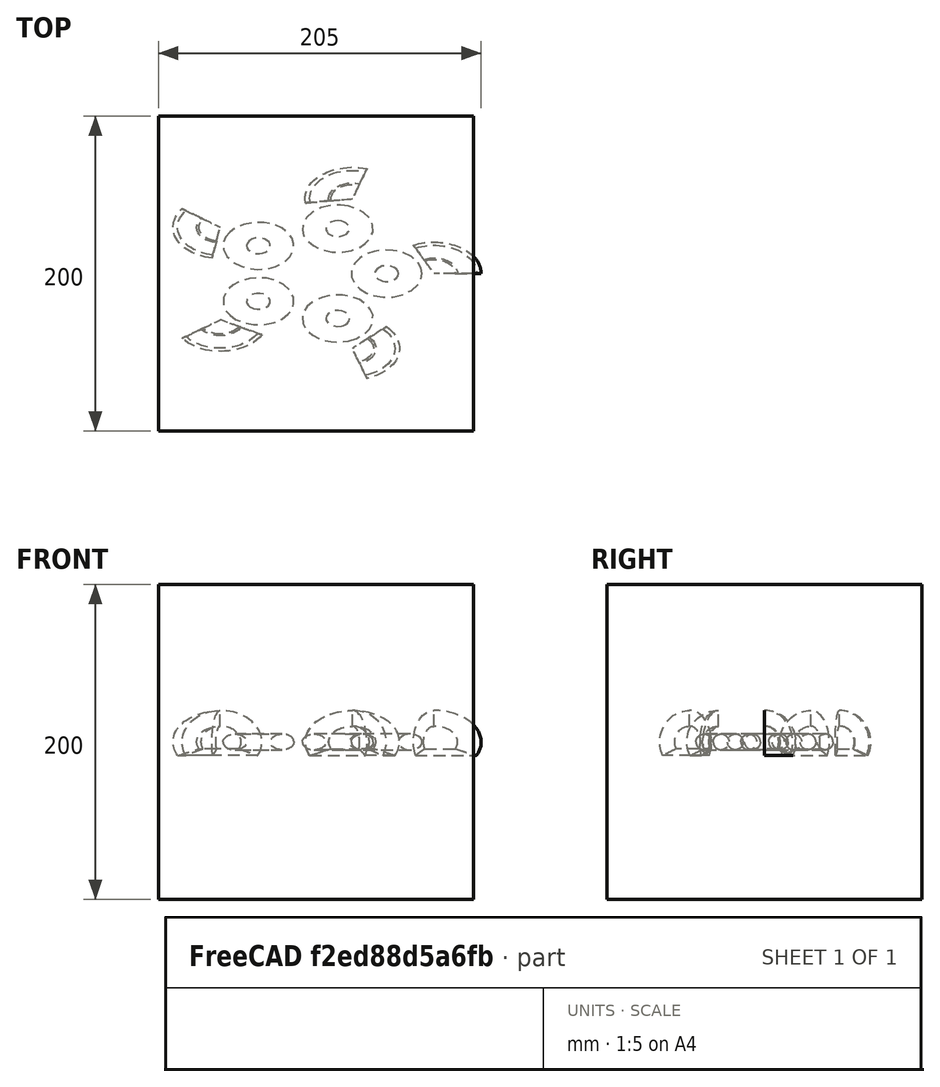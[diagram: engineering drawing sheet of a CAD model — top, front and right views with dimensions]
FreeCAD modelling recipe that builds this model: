
FCSTD DOCUMENT  (FreeCAD 0.19RUnknown)
Label: arrayTest-7_scaled
License: All rights reserved
LicenseURL: http://en.wikipedia.org/wiki/All_rights_reserved
objects: App::DocumentObjectGroupPython×1248, Part::FeaturePython×5, App::Part×2, Part::MultiFuse×1
note: 6 computed .brp shape members not serialized (recipe doc carries the construction recipe); baked Part::Feature solids carry a one-line shape summary decoded from their .brp

FEATURE [App::DocumentObjectGroupPython] HALFPI  # scripted group (container) (typed FeaturePython)
  name = HALFPI
  value = pi/2.
FEATURE [App::DocumentObjectGroupPython] PI  # scripted group (container) (typed FeaturePython)
  name = PI
  value = 1.*pi
FEATURE [App::DocumentObjectGroupPython] TWOPI  # scripted group (container) (typed FeaturePython)
  name = TWOPI
  value = 2.*pi
FEATURE [App::DocumentObjectGroupPython] Constants  # scripted group (container) (typed FeaturePython)
  Group = -> [HALFPI,PI,TWOPI]
FEATURE [App::DocumentObjectGroupPython] Variables  # scripted group (container) (typed FeaturePython)
FEATURE [App::DocumentObjectGroupPython] Quantities  # scripted group (container) (typed FeaturePython)
FEATURE [App::DocumentObjectGroupPython] Isotopes  # scripted group (container) (typed FeaturePython)
FEATURE [App::DocumentObjectGroupPython] Elements  # scripted group (container) (typed FeaturePython)
FEATURE [App::DocumentObjectGroupPython] G4Isotopes  # scripted group (container) (typed FeaturePython)
FEATURE [App::DocumentObjectGroupPython] H_element  # scripted group (container) (typed FeaturePython)
  Z = 1
  atom_value = 1.008
  formula = H
  name = H_element
FEATURE [App::DocumentObjectGroupPython] He_element  # scripted group (container) (typed FeaturePython)
  Z = 2
  atom_value = 4.0026
  formula = He
  name = He_element
FEATURE [App::DocumentObjectGroupPython] Li_element  # scripted group (container) (typed FeaturePython)
  Z = 3
  atom_value = 6.94
  formula = Li
  name = Li_element
FEATURE [App::DocumentObjectGroupPython] Be_element  # scripted group (container) (typed FeaturePython)
  Z = 4
  atom_value = 9.01218
  formula = Be
  name = Be_element
FEATURE [App::DocumentObjectGroupPython] B_element  # scripted group (container) (typed FeaturePython)
  Z = 5
  atom_value = 10.81
  formula = B
  name = B_element
FEATURE [App::DocumentObjectGroupPython] C_element  # scripted group (container) (typed FeaturePython)
  Z = 6
  atom_value = 12.011
  formula = C
  name = C_element
FEATURE [App::DocumentObjectGroupPython] N_element  # scripted group (container) (typed FeaturePython)
  Z = 7
  atom_value = 14.007
  formula = N
  name = N_element
FEATURE [App::DocumentObjectGroupPython] O_element  # scripted group (container) (typed FeaturePython)
  Z = 8
  atom_value = 15.999
  formula = O
  name = O_element
FEATURE [App::DocumentObjectGroupPython] F_element  # scripted group (container) (typed FeaturePython)
  Z = 9
  atom_value = 18.9984
  formula = F
  name = F_element
FEATURE [App::DocumentObjectGroupPython] Ne_element  # scripted group (container) (typed FeaturePython)
  Z = 10
  atom_value = 20.1797
  formula = Ne
  name = Ne_element
FEATURE [App::DocumentObjectGroupPython] Na_element  # scripted group (container) (typed FeaturePython)
  Z = 11
  atom_value = 22.9898
  formula = Na
  name = Na_element
FEATURE [App::DocumentObjectGroupPython] Mg_element  # scripted group (container) (typed FeaturePython)
  Z = 12
  atom_value = 24.305
  formula = Mg
  name = Mg_element
FEATURE [App::DocumentObjectGroupPython] Al_element  # scripted group (container) (typed FeaturePython)
  Z = 13
  atom_value = 26.9815
  formula = Al
  name = Al_element
FEATURE [App::DocumentObjectGroupPython] Si_element  # scripted group (container) (typed FeaturePython)
  Z = 14
  atom_value = 28.085
  formula = Si
  name = Si_element
FEATURE [App::DocumentObjectGroupPython] P_element  # scripted group (container) (typed FeaturePython)
  Z = 15
  atom_value = 30.9738
  formula = P
  name = P_element
FEATURE [App::DocumentObjectGroupPython] S_element  # scripted group (container) (typed FeaturePython)
  Z = 16
  atom_value = 32.06
  formula = S
  name = S_element
FEATURE [App::DocumentObjectGroupPython] Cl_element  # scripted group (container) (typed FeaturePython)
  Z = 17
  atom_value = 35.45
  formula = Cl
  name = Cl_element
FEATURE [App::DocumentObjectGroupPython] Ar_element  # scripted group (container) (typed FeaturePython)
  Z = 18
  atom_value = 39.95
  formula = Ar
  name = Ar_element
FEATURE [App::DocumentObjectGroupPython] K_element  # scripted group (container) (typed FeaturePython)
  Z = 19
  atom_value = 39.0983
  formula = K
  name = K_element
FEATURE [App::DocumentObjectGroupPython] Ca_element  # scripted group (container) (typed FeaturePython)
  Z = 20
  atom_value = 40.078
  formula = Ca
  name = Ca_element
FEATURE [App::DocumentObjectGroupPython] Sc_element  # scripted group (container) (typed FeaturePython)
  Z = 21
  atom_value = 44.9559
  formula = Sc
  name = Sc_element
FEATURE [App::DocumentObjectGroupPython] Ti_element  # scripted group (container) (typed FeaturePython)
  Z = 22
  atom_value = 47.867
  formula = Ti
  name = Ti_element
FEATURE [App::DocumentObjectGroupPython] V_element  # scripted group (container) (typed FeaturePython)
  Z = 23
  atom_value = 50.9415
  formula = V
  name = V_element
FEATURE [App::DocumentObjectGroupPython] Cr_element  # scripted group (container) (typed FeaturePython)
  Z = 24
  atom_value = 51.9961
  formula = Cr
  name = Cr_element
FEATURE [App::DocumentObjectGroupPython] Mn_element  # scripted group (container) (typed FeaturePython)
  Z = 25
  atom_value = 54.938
  formula = Mn
  name = Mn_element
FEATURE [App::DocumentObjectGroupPython] Fe_element  # scripted group (container) (typed FeaturePython)
  Z = 26
  atom_value = 55.845
  formula = Fe
  name = Fe_element
FEATURE [App::DocumentObjectGroupPython] Co_element  # scripted group (container) (typed FeaturePython)
  Z = 27
  atom_value = 58.9332
  formula = Co
  name = Co_element
FEATURE [App::DocumentObjectGroupPython] Ni_element  # scripted group (container) (typed FeaturePython)
  Z = 28
  atom_value = 58.6934
  formula = Ni
  name = Ni_element
FEATURE [App::DocumentObjectGroupPython] Cu_element  # scripted group (container) (typed FeaturePython)
  Z = 29
  atom_value = 63.546
  formula = Cu
  name = Cu_element
FEATURE [App::DocumentObjectGroupPython] Zn_element  # scripted group (container) (typed FeaturePython)
  Z = 30
  atom_value = 65.38
  formula = Zn
  name = Zn_element
FEATURE [App::DocumentObjectGroupPython] Ga_element  # scripted group (container) (typed FeaturePython)
  Z = 31
  atom_value = 69.723
  formula = Ga
  name = Ga_element
FEATURE [App::DocumentObjectGroupPython] Ge_element  # scripted group (container) (typed FeaturePython)
  Z = 32
  atom_value = 72.63
  formula = Ge
  name = Ge_element
FEATURE [App::DocumentObjectGroupPython] As_element  # scripted group (container) (typed FeaturePython)
  Z = 33
  atom_value = 74.9216
  formula = As
  name = As_element
FEATURE [App::DocumentObjectGroupPython] Se_element  # scripted group (container) (typed FeaturePython)
  Z = 34
  atom_value = 78.971
  formula = Se
  name = Se_element
FEATURE [App::DocumentObjectGroupPython] Br_element  # scripted group (container) (typed FeaturePython)
  Z = 35
  atom_value = 79.904
  formula = Br
  name = Br_element
FEATURE [App::DocumentObjectGroupPython] Kr_element  # scripted group (container) (typed FeaturePython)
  Z = 36
  atom_value = 83.798
  formula = Kr
  name = Kr_element
FEATURE [App::DocumentObjectGroupPython] Rb_element  # scripted group (container) (typed FeaturePython)
  Z = 37
  atom_value = 85.4678
  formula = Rb
  name = Rb_element
FEATURE [App::DocumentObjectGroupPython] Sr_element  # scripted group (container) (typed FeaturePython)
  Z = 38
  atom_value = 87.62
  formula = Sr
  name = Sr_element
FEATURE [App::DocumentObjectGroupPython] Y_element  # scripted group (container) (typed FeaturePython)
  Z = 39
  atom_value = 88.9058
  formula = Y
  name = Y_element
FEATURE [App::DocumentObjectGroupPython] Zr_element  # scripted group (container) (typed FeaturePython)
  Z = 40
  atom_value = 91.224
  formula = Zr
  name = Zr_element
FEATURE [App::DocumentObjectGroupPython] Nb_element  # scripted group (container) (typed FeaturePython)
  Z = 41
  atom_value = 92.9064
  formula = Nb
  name = Nb_element
FEATURE [App::DocumentObjectGroupPython] Mo_element  # scripted group (container) (typed FeaturePython)
  Z = 42
  atom_value = 95.95
  formula = Mo
  name = Mo_element
FEATURE [App::DocumentObjectGroupPython] Tc_element  # scripted group (container) (typed FeaturePython)
  Z = 43
  atom_value = 97
  formula = Tc
  name = Tc_element
FEATURE [App::DocumentObjectGroupPython] Ru_element  # scripted group (container) (typed FeaturePython)
  Z = 44
  atom_value = 101.07
  formula = Ru
  name = Ru_element
FEATURE [App::DocumentObjectGroupPython] Rh_element  # scripted group (container) (typed FeaturePython)
  Z = 45
  atom_value = 102.905
  formula = Rh
  name = Rh_element
FEATURE [App::DocumentObjectGroupPython] Pd_element  # scripted group (container) (typed FeaturePython)
  Z = 46
  atom_value = 106.42
  formula = Pd
  name = Pd_element
FEATURE [App::DocumentObjectGroupPython] Ag_element  # scripted group (container) (typed FeaturePython)
  Z = 47
  atom_value = 107.868
  formula = Ag
  name = Ag_element
FEATURE [App::DocumentObjectGroupPython] Cd_element  # scripted group (container) (typed FeaturePython)
  Z = 48
  atom_value = 112.414
  formula = Cd
  name = Cd_element
FEATURE [App::DocumentObjectGroupPython] In_element  # scripted group (container) (typed FeaturePython)
  Z = 49
  atom_value = 114.818
  formula = In
  name = In_element
FEATURE [App::DocumentObjectGroupPython] Sn_element  # scripted group (container) (typed FeaturePython)
  Z = 50
  atom_value = 118.71
  formula = Sn
  name = Sn_element
FEATURE [App::DocumentObjectGroupPython] Sb_element  # scripted group (container) (typed FeaturePython)
  Z = 51
  atom_value = 121.76
  formula = Sb
  name = Sb_element
FEATURE [App::DocumentObjectGroupPython] Te_element  # scripted group (container) (typed FeaturePython)
  Z = 52
  atom_value = 127.6
  formula = Te
  name = Te_element
FEATURE [App::DocumentObjectGroupPython] I_element  # scripted group (container) (typed FeaturePython)
  Z = 53
  atom_value = 126.904
  formula = I
  name = I_element
FEATURE [App::DocumentObjectGroupPython] Xe_element  # scripted group (container) (typed FeaturePython)
  Z = 54
  atom_value = 131.293
  formula = Xe
  name = Xe_element
FEATURE [App::DocumentObjectGroupPython] Cs_element  # scripted group (container) (typed FeaturePython)
  Z = 55
  atom_value = 132.905
  formula = Cs
  name = Cs_element
FEATURE [App::DocumentObjectGroupPython] Ba_element  # scripted group (container) (typed FeaturePython)
  Z = 56
  atom_value = 137.327
  formula = Ba
  name = Ba_element
FEATURE [App::DocumentObjectGroupPython] La_element  # scripted group (container) (typed FeaturePython)
  Z = 57
  atom_value = 138.905
  formula = La
  name = La_element
FEATURE [App::DocumentObjectGroupPython] Ce_element  # scripted group (container) (typed FeaturePython)
  Z = 58
  atom_value = 140.116
  formula = Ce
  name = Ce_element
FEATURE [App::DocumentObjectGroupPython] Pr_element  # scripted group (container) (typed FeaturePython)
  Z = 59
  atom_value = 140.908
  formula = Pr
  name = Pr_element
FEATURE [App::DocumentObjectGroupPython] Nd_element  # scripted group (container) (typed FeaturePython)
  Z = 60
  atom_value = 144.242
  formula = Nd
  name = Nd_element
FEATURE [App::DocumentObjectGroupPython] Pm_element  # scripted group (container) (typed FeaturePython)
  Z = 61
  atom_value = 145
  formula = Pm
  name = Pm_element
FEATURE [App::DocumentObjectGroupPython] Sm_element  # scripted group (container) (typed FeaturePython)
  Z = 62
  atom_value = 150.36
  formula = Sm
  name = Sm_element
FEATURE [App::DocumentObjectGroupPython] Eu_element  # scripted group (container) (typed FeaturePython)
  Z = 63
  atom_value = 151.964
  formula = Eu
  name = Eu_element
FEATURE [App::DocumentObjectGroupPython] Gd_element  # scripted group (container) (typed FeaturePython)
  Z = 64
  atom_value = 157.25
  formula = Gd
  name = Gd_element
FEATURE [App::DocumentObjectGroupPython] Tb_element  # scripted group (container) (typed FeaturePython)
  Z = 65
  atom_value = 158.925
  formula = Tb
  name = Tb_element
FEATURE [App::DocumentObjectGroupPython] Dy_element  # scripted group (container) (typed FeaturePython)
  Z = 66
  atom_value = 162.5
  formula = Dy
  name = Dy_element
FEATURE [App::DocumentObjectGroupPython] Ho_element  # scripted group (container) (typed FeaturePython)
  Z = 67
  atom_value = 164.93
  formula = Ho
  name = Ho_element
FEATURE [App::DocumentObjectGroupPython] Er_element  # scripted group (container) (typed FeaturePython)
  Z = 68
  atom_value = 167.259
  formula = Er
  name = Er_element
FEATURE [App::DocumentObjectGroupPython] Tm_element  # scripted group (container) (typed FeaturePython)
  Z = 69
  atom_value = 168.934
  formula = Tm
  name = Tm_element
FEATURE [App::DocumentObjectGroupPython] Yb_element  # scripted group (container) (typed FeaturePython)
  Z = 70
  atom_value = 173.045
  formula = Yb
  name = Yb_element
FEATURE [App::DocumentObjectGroupPython] Lu_element  # scripted group (container) (typed FeaturePython)
  Z = 71
  atom_value = 174.967
  formula = Lu
  name = Lu_element
FEATURE [App::DocumentObjectGroupPython] Hf_element  # scripted group (container) (typed FeaturePython)
  Z = 72
  atom_value = 178.49
  formula = Hf
  name = Hf_element
FEATURE [App::DocumentObjectGroupPython] Ta_element  # scripted group (container) (typed FeaturePython)
  Z = 73
  atom_value = 180.948
  formula = Ta
  name = Ta_element
FEATURE [App::DocumentObjectGroupPython] W_element  # scripted group (container) (typed FeaturePython)
  Z = 74
  atom_value = 183.84
  formula = W
  name = W_element
FEATURE [App::DocumentObjectGroupPython] Re_element  # scripted group (container) (typed FeaturePython)
  Z = 75
  atom_value = 186.207
  formula = Re
  name = Re_element
FEATURE [App::DocumentObjectGroupPython] Os_element  # scripted group (container) (typed FeaturePython)
  Z = 76
  atom_value = 190.23
  formula = Os
  name = Os_element
FEATURE [App::DocumentObjectGroupPython] Ir_element  # scripted group (container) (typed FeaturePython)
  Z = 77
  atom_value = 192.217
  formula = Ir
  name = Ir_element
FEATURE [App::DocumentObjectGroupPython] Pt_element  # scripted group (container) (typed FeaturePython)
  Z = 78
  atom_value = 195.084
  formula = Pt
  name = Pt_element
FEATURE [App::DocumentObjectGroupPython] Au_element  # scripted group (container) (typed FeaturePython)
  Z = 79
  atom_value = 196.967
  formula = Au
  name = Au_element
FEATURE [App::DocumentObjectGroupPython] Hg_element  # scripted group (container) (typed FeaturePython)
  Z = 80
  atom_value = 200.592
  formula = Hg
  name = Hg_element
FEATURE [App::DocumentObjectGroupPython] Tl_element  # scripted group (container) (typed FeaturePython)
  Z = 81
  atom_value = 204.38
  formula = Tl
  name = Tl_element
FEATURE [App::DocumentObjectGroupPython] Pb_element  # scripted group (container) (typed FeaturePython)
  Z = 82
  atom_value = 207.2
  formula = Pb
  name = Pb_element
FEATURE [App::DocumentObjectGroupPython] Bi_element  # scripted group (container) (typed FeaturePython)
  Z = 83
  atom_value = 208.98
  formula = Bi
  name = Bi_element
FEATURE [App::DocumentObjectGroupPython] Po_element  # scripted group (container) (typed FeaturePython)
  Z = 84
  atom_value = 209
  formula = Po
  name = Po_element
FEATURE [App::DocumentObjectGroupPython] At_element  # scripted group (container) (typed FeaturePython)
  Z = 85
  atom_value = 210
  formula = At
  name = At_element
FEATURE [App::DocumentObjectGroupPython] Rn_element  # scripted group (container) (typed FeaturePython)
  Z = 86
  atom_value = 222
  formula = Rn
  name = Rn_element
FEATURE [App::DocumentObjectGroupPython] Fr_element  # scripted group (container) (typed FeaturePython)
  Z = 87
  atom_value = 223
  formula = Fr
  name = Fr_element
FEATURE [App::DocumentObjectGroupPython] Ra_element  # scripted group (container) (typed FeaturePython)
  Z = 88
  atom_value = 226
  formula = Ra
  name = Ra_element
FEATURE [App::DocumentObjectGroupPython] Ac_element  # scripted group (container) (typed FeaturePython)
  Z = 89
  atom_value = 227
  formula = Ac
  name = Ac_element
FEATURE [App::DocumentObjectGroupPython] Th_element  # scripted group (container) (typed FeaturePython)
  Z = 90
  atom_value = 232.038
  formula = Th
  name = Th_element
FEATURE [App::DocumentObjectGroupPython] Pa_element  # scripted group (container) (typed FeaturePython)
  Z = 91
  atom_value = 231.036
  formula = Pa
  name = Pa_element
FEATURE [App::DocumentObjectGroupPython] U_element  # scripted group (container) (typed FeaturePython)
  Z = 92
  atom_value = 238.029
  formula = U
  name = U_element
FEATURE [App::DocumentObjectGroupPython] Np_element  # scripted group (container) (typed FeaturePython)
  Z = 93
  atom_value = 237
  formula = Np
  name = Np_element
FEATURE [App::DocumentObjectGroupPython] Pu_element  # scripted group (container) (typed FeaturePython)
  Z = 94
  atom_value = 244
  formula = Pu
  name = Pu_element
FEATURE [App::DocumentObjectGroupPython] Am_element  # scripted group (container) (typed FeaturePython)
  Z = 95
  atom_value = 243
  formula = Am
  name = Am_element
FEATURE [App::DocumentObjectGroupPython] Cm_element  # scripted group (container) (typed FeaturePython)
  Z = 96
  atom_value = 247
  formula = Cm
  name = Cm_element
FEATURE [App::DocumentObjectGroupPython] Bk_element  # scripted group (container) (typed FeaturePython)
  Z = 97
  atom_value = 247
  formula = Bk
  name = Bk_element
FEATURE [App::DocumentObjectGroupPython] Cf_element  # scripted group (container) (typed FeaturePython)
  Z = 98
  atom_value = 251
  formula = Cf
  name = Cf_element
FEATURE [App::DocumentObjectGroupPython] G4Elements  # scripted group (container) (typed FeaturePython)
  Group = -> [H_element,He_element,Li_element,Be_element,B_element,C_element,N_element,O_element,F_element,Ne_element,Na_element,Mg_element,Al_element,Si_element,P_element,S_element,Cl_element,Ar_element,K_element,Ca_element,Sc_element,Ti_element,V_element,Cr_element,Mn_element,Fe_element,Co_element,Ni_element,Cu_element,Zn_element,Ga_element,Ge_element,As_element,Se_element,Br_element,Kr_element,Rb_element,+61 more]
FEATURE [App::DocumentObjectGroupPython] H_element001  label="H_element : 0.101"  # scripted group (container) (typed FeaturePython)
  n = 0.101327
FEATURE [App::DocumentObjectGroupPython] C_element001  label="C_element : 0.775"  # scripted group (container) (typed FeaturePython)
  n = 0.7755
FEATURE [App::DocumentObjectGroupPython] N_element001  label="N_element : 0.035"  # scripted group (container) (typed FeaturePython)
  n = 0.035057
FEATURE [App::DocumentObjectGroupPython] O_element001  label="O_element : 0.052"  # scripted group (container) (typed FeaturePython)
  n = 0.0523159
FEATURE [App::DocumentObjectGroupPython] F_element001  label="F_element : 0.017"  # scripted group (container) (typed FeaturePython)
  n = 0.017422
FEATURE [App::DocumentObjectGroupPython] Ca_element001  label="Ca_element : 0.018"  # scripted group (container) (typed FeaturePython)
  n = 0.018378
FEATURE [App::DocumentObjectGroupPython] G4_A_150_TISSUE  label="G4_A-150_TISSUE"  # scripted group (container) (typed FeaturePython)
  Dunit = g/cm3
  Dvalue = 1.127
  Group = -> [H_element001,C_element001,N_element001,O_element001,F_element001,Ca_element001]
  conduct = 2
  density = 1
  expand = 3
  formula = G4_A-150_TISSUE
  name = G4_A-150_TISSUE
  specific = 4
FEATURE [App::DocumentObjectGroupPython] C_element002  label="C_element : 3"  # scripted group (container) (typed FeaturePython)
  n = 3
  ref = C_element
FEATURE [App::DocumentObjectGroupPython] H_element002  label="H_element : 6"  # scripted group (container) (typed FeaturePython)
  n = 6
  ref = H_element
FEATURE [App::DocumentObjectGroupPython] O_element002  label="O_element : 1"  # scripted group (container) (typed FeaturePython)
  n = 1
  ref = O_element
FEATURE [App::DocumentObjectGroupPython] G4_ACETONE  # scripted group (container) (typed FeaturePython)
  Dunit = g/cm3
  Dvalue = 0.7899
  Group = -> [C_element002,H_element002,O_element002]
  conduct = 2
  density = 1
  expand = 3
  formula = G4_ACETONE
  name = G4_ACETONE
  specific = 4
FEATURE [App::DocumentObjectGroupPython] C_element003  label="C_element : 2"  # scripted group (container) (typed FeaturePython)
  n = 2
  ref = C_element
FEATURE [App::DocumentObjectGroupPython] H_element003  label="H_element : 2"  # scripted group (container) (typed FeaturePython)
  n = 2
  ref = H_element
FEATURE [App::DocumentObjectGroupPython] G4_ACETYLENE  # scripted group (container) (typed FeaturePython)
  Dunit = g/cm3
  Dvalue = 0.0010967
  Group = -> [C_element003,H_element003]
  conduct = 2
  density = 1
  expand = 3
  formula = G4_ACETYLENE
  name = G4_ACETYLENE
  specific = 4
FEATURE [App::DocumentObjectGroupPython] C_element004  label="C_element : 5"  # scripted group (container) (typed FeaturePython)
  n = 5
  ref = C_element
FEATURE [App::DocumentObjectGroupPython] H_element004  label="H_element : 5"  # scripted group (container) (typed FeaturePython)
  n = 5
  ref = H_element
FEATURE [App::DocumentObjectGroupPython] N_element002  label="N_element : 5"  # scripted group (container) (typed FeaturePython)
  n = 5
  ref = N_element
FEATURE [App::DocumentObjectGroupPython] G4_ADENINE  # scripted group (container) (typed FeaturePython)
  Dunit = g/cm3
  Dvalue = 1.6
  Group = -> [C_element004,H_element004,N_element002]
  conduct = 2
  density = 1
  expand = 3
  formula = G4_ADENINE
  name = G4_ADENINE
  specific = 4
FEATURE [App::DocumentObjectGroupPython] H_element005  label="H_element : 0.114"  # scripted group (container) (typed FeaturePython)
  n = 0.114
FEATURE [App::DocumentObjectGroupPython] C_element005  label="C_element : 0.598"  # scripted group (container) (typed FeaturePython)
  n = 0.598
FEATURE [App::DocumentObjectGroupPython] N_element003  label="N_element : 0.007"  # scripted group (container) (typed FeaturePython)
  n = 0.007
FEATURE [App::DocumentObjectGroupPython] O_element003  label="O_element : 0.278"  # scripted group (container) (typed FeaturePython)
  n = 0.278
FEATURE [App::DocumentObjectGroupPython] Na_element001  label="Na_element : 0.001"  # scripted group (container) (typed FeaturePython)
  n = 0.001
FEATURE [App::DocumentObjectGroupPython] S_element001  label="S_element : 0.001"  # scripted group (container) (typed FeaturePython)
  n = 0.001
FEATURE [App::DocumentObjectGroupPython] Cl_element001  label="Cl_element : 0.001"  # scripted group (container) (typed FeaturePython)
  n = 0.001
FEATURE [App::DocumentObjectGroupPython] G4_ADIPOSE_TISSUE_ICRP  # scripted group (container) (typed FeaturePython)
  Dunit = g/cm3
  Dvalue = 0.95
  Group = -> [H_element005,C_element005,N_element003,O_element003,Na_element001,S_element001,Cl_element001]
  conduct = 2
  density = 1
  expand = 3
  formula = G4_ADIPOSE_TISSUE_ICRP
  name = G4_ADIPOSE_TISSUE_ICRP
  specific = 4
FEATURE [App::DocumentObjectGroupPython] C_element006  label="C_element : 0.000"  # scripted group (container) (typed FeaturePython)
  n = 0.000124
FEATURE [App::DocumentObjectGroupPython] N_element004  label="N_element : 0.755"  # scripted group (container) (typed FeaturePython)
  n = 0.755268
FEATURE [App::DocumentObjectGroupPython] O_element004  label="O_element : 0.232"  # scripted group (container) (typed FeaturePython)
  n = 0.231781
FEATURE [App::DocumentObjectGroupPython] Ar_element001  label="Ar_element : 0.013"  # scripted group (container) (typed FeaturePython)
  n = 0.012827
FEATURE [App::DocumentObjectGroupPython] G4_AIR  # scripted group (container) (typed FeaturePython)
  Dunit = g/cm3
  Dvalue = 0.00120479
  Group = -> [C_element006,N_element004,O_element004,Ar_element001]
  conduct = 2
  density = 1
  expand = 3
  formula = G4_AIR
  name = G4_AIR
  specific = 4
FEATURE [App::DocumentObjectGroupPython] C_element007  label="C_element : 006"  # scripted group (container) (typed FeaturePython)
  n = 3
  ref = C_element
FEATURE [App::DocumentObjectGroupPython] H_element006  label="H_element : 7"  # scripted group (container) (typed FeaturePython)
  n = 7
  ref = H_element
FEATURE [App::DocumentObjectGroupPython] N_element005  label="N_element : 1"  # scripted group (container) (typed FeaturePython)
  n = 1
  ref = N_element
FEATURE [App::DocumentObjectGroupPython] O_element005  label="O_element : 2"  # scripted group (container) (typed FeaturePython)
  n = 2
  ref = O_element
FEATURE [App::DocumentObjectGroupPython] G4_ALANINE  # scripted group (container) (typed FeaturePython)
  Dunit = g/cm3
  Dvalue = 1.42
  Group = -> [C_element007,H_element006,N_element005,O_element005]
  conduct = 2
  density = 1
  expand = 3
  formula = G4_ALANINE
  name = G4_ALANINE
  specific = 4
FEATURE [App::DocumentObjectGroupPython] Al_element001  label="Al_element : 2"  # scripted group (container) (typed FeaturePython)
  n = 2
  ref = Al_element
FEATURE [App::DocumentObjectGroupPython] O_element006  label="O_element : 3"  # scripted group (container) (typed FeaturePython)
  n = 3
  ref = O_element
FEATURE [App::DocumentObjectGroupPython] G4_ALUMINUM_OXIDE  # scripted group (container) (typed FeaturePython)
  Dunit = g/cm3
  Dvalue = 3.97
  Group = -> [Al_element001,O_element006]
  conduct = 2
  density = 1
  expand = 3
  formula = G4_ALUMINUM_OXIDE
  name = G4_ALUMINUM_OXIDE
  specific = 4
FEATURE [App::DocumentObjectGroupPython] H_element007  label="H_element : 0.106"  # scripted group (container) (typed FeaturePython)
  n = 0.10593
FEATURE [App::DocumentObjectGroupPython] C_element008  label="C_element : 0.789"  # scripted group (container) (typed FeaturePython)
  n = 0.788974
FEATURE [App::DocumentObjectGroupPython] O_element007  label="O_element : 0.105"  # scripted group (container) (typed FeaturePython)
  n = 0.105096
FEATURE [App::DocumentObjectGroupPython] G4_AMBER  # scripted group (container) (typed FeaturePython)
  Dunit = g/cm3
  Dvalue = 1.1
  Group = -> [H_element007,C_element008,O_element007]
  conduct = 2
  density = 1
  expand = 3
  formula = G4_AMBER
  name = G4_AMBER
  specific = 4
FEATURE [App::DocumentObjectGroupPython] N_element006  label="N_element : 006"  # scripted group (container) (typed FeaturePython)
  n = 1
  ref = N_element
FEATURE [App::DocumentObjectGroupPython] H_element008  label="H_element : 3"  # scripted group (container) (typed FeaturePython)
  n = 3
  ref = H_element
FEATURE [App::DocumentObjectGroupPython] G4_AMMONIA  # scripted group (container) (typed FeaturePython)
  Dunit = g/cm3
  Dvalue = 0.000826019
  Group = -> [N_element006,H_element008]
  conduct = 2
  density = 1
  expand = 3
  formula = G4_AMMONIA
  name = G4_AMMONIA
  specific = 4
FEATURE [App::DocumentObjectGroupPython] C_element009  label="C_element : 6"  # scripted group (container) (typed FeaturePython)
  n = 6
  ref = C_element
FEATURE [App::DocumentObjectGroupPython] H_element009  label="H_element : 008"  # scripted group (container) (typed FeaturePython)
  n = 7
  ref = H_element
FEATURE [App::DocumentObjectGroupPython] N_element007  label="N_element : 007"  # scripted group (container) (typed FeaturePython)
  n = 1
  ref = N_element
FEATURE [App::DocumentObjectGroupPython] G4_ANILINE  # scripted group (container) (typed FeaturePython)
  Dunit = g/cm3
  Dvalue = 1.0235
  Group = -> [C_element009,H_element009,N_element007]
  conduct = 2
  density = 1
  expand = 3
  formula = G4_ANILINE
  name = G4_ANILINE
  specific = 4
FEATURE [App::DocumentObjectGroupPython] C_element010  label="C_element : 14"  # scripted group (container) (typed FeaturePython)
  n = 14
  ref = C_element
FEATURE [App::DocumentObjectGroupPython] H_element010  label="H_element : 10"  # scripted group (container) (typed FeaturePython)
  n = 10
  ref = H_element
FEATURE [App::DocumentObjectGroupPython] G4_ANTHRACENE  # scripted group (container) (typed FeaturePython)
  Dunit = g/cm3
  Dvalue = 1.283
  Group = -> [C_element010,H_element010]
  conduct = 2
  density = 1
  expand = 3
  formula = G4_ANTHRACENE
  name = G4_ANTHRACENE
  specific = 4
FEATURE [App::DocumentObjectGroupPython] H_element011  label="H_element : 0.065"  # scripted group (container) (typed FeaturePython)
  n = 0.0654709
FEATURE [App::DocumentObjectGroupPython] C_element011  label="C_element : 0.537"  # scripted group (container) (typed FeaturePython)
  n = 0.536944
FEATURE [App::DocumentObjectGroupPython] N_element008  label="N_element : 0.021"  # scripted group (container) (typed FeaturePython)
  n = 0.0215
FEATURE [App::DocumentObjectGroupPython] O_element008  label="O_element : 0.032"  # scripted group (container) (typed FeaturePython)
  n = 0.032085
FEATURE [App::DocumentObjectGroupPython] F_element002  label="F_element : 0.167"  # scripted group (container) (typed FeaturePython)
  n = 0.167411
FEATURE [App::DocumentObjectGroupPython] Ca_element002  label="Ca_element : 0.177"  # scripted group (container) (typed FeaturePython)
  n = 0.176589
FEATURE [App::DocumentObjectGroupPython] G4_B_100_BONE  label="G4_B-100_BONE"  # scripted group (container) (typed FeaturePython)
  Dunit = g/cm3
  Dvalue = 1.45
  Group = -> [H_element011,C_element011,N_element008,O_element008,F_element002,Ca_element002]
  conduct = 2
  density = 1
  expand = 3
  formula = G4_B-100_BONE
  name = G4_B-100_BONE
  specific = 4
FEATURE [App::DocumentObjectGroupPython] H_element012  label="H_element : 0.057"  # scripted group (container) (typed FeaturePython)
  n = 0.057441
FEATURE [App::DocumentObjectGroupPython] C_element012  label="C_element : 0.790"  # scripted group (container) (typed FeaturePython)
  n = 0.774591
FEATURE [App::DocumentObjectGroupPython] O_element009  label="O_element : 0.168"  # scripted group (container) (typed FeaturePython)
  n = 0.167968
FEATURE [App::DocumentObjectGroupPython] G4_BAKELITE  # scripted group (container) (typed FeaturePython)
  Dunit = g/cm3
  Dvalue = 1.25
  Group = -> [H_element012,C_element012,O_element009]
  conduct = 2
  density = 1
  expand = 3
  formula = G4_BAKELITE
  name = G4_BAKELITE
  specific = 4
FEATURE [App::DocumentObjectGroupPython] Ba_element001  label="Ba_element : 1"  # scripted group (container) (typed FeaturePython)
  n = 1
  ref = Ba_element
FEATURE [App::DocumentObjectGroupPython] F_element003  label="F_element : 2"  # scripted group (container) (typed FeaturePython)
  n = 2
  ref = F_element
FEATURE [App::DocumentObjectGroupPython] G4_BARIUM_FLUORIDE  # scripted group (container) (typed FeaturePython)
  Dunit = g/cm3
  Dvalue = 4.89
  Group = -> [Ba_element001,F_element003]
  conduct = 2
  density = 1
  expand = 3
  formula = G4_BARIUM_FLUORIDE
  name = G4_BARIUM_FLUORIDE
  specific = 4
FEATURE [App::DocumentObjectGroupPython] Ba_element002  label="Ba_element : 002"  # scripted group (container) (typed FeaturePython)
  n = 1
  ref = Ba_element
FEATURE [App::DocumentObjectGroupPython] S_element002  label="S_element : 1"  # scripted group (container) (typed FeaturePython)
  n = 1
  ref = S_element
FEATURE [App::DocumentObjectGroupPython] O_element010  label="O_element : 4"  # scripted group (container) (typed FeaturePython)
  n = 4
  ref = O_element
FEATURE [App::DocumentObjectGroupPython] G4_BARIUM_SULFATE  # scripted group (container) (typed FeaturePython)
  Dunit = g/cm3
  Dvalue = 4.5
  Group = -> [Ba_element002,S_element002,O_element010]
  conduct = 2
  density = 1
  expand = 3
  formula = G4_BARIUM_SULFATE
  name = G4_BARIUM_SULFATE
  specific = 4
FEATURE [App::DocumentObjectGroupPython] C_element013  label="C_element : 007"  # scripted group (container) (typed FeaturePython)
  n = 6
  ref = C_element
FEATURE [App::DocumentObjectGroupPython] H_element013  label="H_element : 009"  # scripted group (container) (typed FeaturePython)
  n = 6
  ref = H_element
FEATURE [App::DocumentObjectGroupPython] G4_BENZENE  # scripted group (container) (typed FeaturePython)
  Dunit = g/cm3
  Dvalue = 0.87865
  Group = -> [C_element013,H_element013]
  conduct = 2
  density = 1
  expand = 3
  formula = G4_BENZENE
  name = G4_BENZENE
  specific = 4
FEATURE [App::DocumentObjectGroupPython] Be_element001  label="Be_element : 1"  # scripted group (container) (typed FeaturePython)
  n = 1
  ref = Be_element
FEATURE [App::DocumentObjectGroupPython] O_element011  label="O_element : 005"  # scripted group (container) (typed FeaturePython)
  n = 1
  ref = O_element
FEATURE [App::DocumentObjectGroupPython] G4_BERYLLIUM_OXIDE  # scripted group (container) (typed FeaturePython)
  Dunit = g/cm3
  Dvalue = 3.01
  Group = -> [Be_element001,O_element011]
  conduct = 2
  density = 1
  expand = 3
  formula = G4_BERYLLIUM_OXIDE
  name = G4_BERYLLIUM_OXIDE
  specific = 4
FEATURE [App::DocumentObjectGroupPython] Bi_element001  label="Bi_element : 4"  # scripted group (container) (typed FeaturePython)
  n = 4
  ref = Bi_element
FEATURE [App::DocumentObjectGroupPython] Ge_element001  label="Ge_element : 3"  # scripted group (container) (typed FeaturePython)
  n = 3
  ref = Ge_element
FEATURE [App::DocumentObjectGroupPython] O_element012  label="O_element : 12"  # scripted group (container) (typed FeaturePython)
  n = 12
  ref = O_element
FEATURE [App::DocumentObjectGroupPython] G4_BGO  # scripted group (container) (typed FeaturePython)
  Dunit = g/cm3
  Dvalue = 7.13
  Group = -> [Bi_element001,Ge_element001,O_element012]
  conduct = 2
  density = 1
  expand = 3
  formula = G4_BGO
  name = G4_BGO
  specific = 4
FEATURE [App::DocumentObjectGroupPython] H_element014  label="H_element : 0.102"  # scripted group (container) (typed FeaturePython)
  n = 0.102
FEATURE [App::DocumentObjectGroupPython] C_element014  label="C_element : 0.110"  # scripted group (container) (typed FeaturePython)
  n = 0.11
FEATURE [App::DocumentObjectGroupPython] N_element009  label="N_element : 0.033"  # scripted group (container) (typed FeaturePython)
  n = 0.033
FEATURE [App::DocumentObjectGroupPython] O_element013  label="O_element : 0.745"  # scripted group (container) (typed FeaturePython)
  n = 0.745
FEATURE [App::DocumentObjectGroupPython] Na_element002  label="Na_element : 0.002"  # scripted group (container) (typed FeaturePython)
  n = 0.001
FEATURE [App::DocumentObjectGroupPython] P_element001  label="P_element : 0.001"  # scripted group (container) (typed FeaturePython)
  n = 0.001
FEATURE [App::DocumentObjectGroupPython] S_element003  label="S_element : 0.002"  # scripted group (container) (typed FeaturePython)
  n = 0.002
FEATURE [App::DocumentObjectGroupPython] Cl_element002  label="Cl_element : 0.003"  # scripted group (container) (typed FeaturePython)
  n = 0.003
FEATURE [App::DocumentObjectGroupPython] K_element001  label="K_element : 0.002"  # scripted group (container) (typed FeaturePython)
  n = 0.002
FEATURE [App::DocumentObjectGroupPython] Fe_element001  label="Fe_element : 0.001"  # scripted group (container) (typed FeaturePython)
  n = 0.001
FEATURE [App::DocumentObjectGroupPython] G4_BLOOD_ICRP  # scripted group (container) (typed FeaturePython)
  Dunit = g/cm3
  Dvalue = 1.06
  Group = -> [H_element014,C_element014,N_element009,O_element013,Na_element002,P_element001,S_element003,Cl_element002,K_element001,Fe_element001]
  conduct = 2
  density = 1
  expand = 3
  formula = G4_BLOOD_ICRP
  name = G4_BLOOD_ICRP
  specific = 4
FEATURE [App::DocumentObjectGroupPython] H_element015  label="H_element : 0.064"  # scripted group (container) (typed FeaturePython)
  n = 0.064
FEATURE [App::DocumentObjectGroupPython] C_element015  label="C_element : 0.278"  # scripted group (container) (typed FeaturePython)
  n = 0.278
FEATURE [App::DocumentObjectGroupPython] N_element010  label="N_element : 0.027"  # scripted group (container) (typed FeaturePython)
  n = 0.027
FEATURE [App::DocumentObjectGroupPython] O_element014  label="O_element : 0.410"  # scripted group (container) (typed FeaturePython)
  n = 0.41
FEATURE [App::DocumentObjectGroupPython] Mg_element001  label="Mg_element : 0.002"  # scripted group (container) (typed FeaturePython)
  n = 0.002
FEATURE [App::DocumentObjectGroupPython] P_element002  label="P_element : 0.070"  # scripted group (container) (typed FeaturePython)
  n = 0.07
FEATURE [App::DocumentObjectGroupPython] S_element004  label="S_element : 0.003"  # scripted group (container) (typed FeaturePython)
  n = 0.002
FEATURE [App::DocumentObjectGroupPython] Ca_element003  label="Ca_element : 0.147"  # scripted group (container) (typed FeaturePython)
  n = 0.147
FEATURE [App::DocumentObjectGroupPython] G4_BONE_COMPACT_ICRU  # scripted group (container) (typed FeaturePython)
  Dunit = g/cm3
  Dvalue = 1.85
  Group = -> [H_element015,C_element015,N_element010,O_element014,Mg_element001,P_element002,S_element004,Ca_element003]
  conduct = 2
  density = 1
  expand = 3
  formula = G4_BONE_COMPACT_ICRU
  name = G4_BONE_COMPACT_ICRU
  specific = 4
FEATURE [App::DocumentObjectGroupPython] H_element016  label="H_element : 0.034"  # scripted group (container) (typed FeaturePython)
  n = 0.034
FEATURE [App::DocumentObjectGroupPython] C_element016  label="C_element : 0.155"  # scripted group (container) (typed FeaturePython)
  n = 0.155
FEATURE [App::DocumentObjectGroupPython] N_element011  label="N_element : 0.042"  # scripted group (container) (typed FeaturePython)
  n = 0.042
FEATURE [App::DocumentObjectGroupPython] O_element015  label="O_element : 0.435"  # scripted group (container) (typed FeaturePython)
  n = 0.435
FEATURE [App::DocumentObjectGroupPython] Na_element003  label="Na_element : 0.003"  # scripted group (container) (typed FeaturePython)
  n = 0.001
FEATURE [App::DocumentObjectGroupPython] Mg_element002  label="Mg_element : 0.003"  # scripted group (container) (typed FeaturePython)
  n = 0.002
FEATURE [App::DocumentObjectGroupPython] P_element003  label="P_element : 0.103"  # scripted group (container) (typed FeaturePython)
  n = 0.103
FEATURE [App::DocumentObjectGroupPython] S_element005  label="S_element : 0.004"  # scripted group (container) (typed FeaturePython)
  n = 0.003
FEATURE [App::DocumentObjectGroupPython] Ca_element004  label="Ca_element : 0.225"  # scripted group (container) (typed FeaturePython)
  n = 0.225
FEATURE [App::DocumentObjectGroupPython] G4_BONE_CORTICAL_ICRP  # scripted group (container) (typed FeaturePython)
  Dunit = g/cm3
  Dvalue = 1.92
  Group = -> [H_element016,C_element016,N_element011,O_element015,Na_element003,Mg_element002,P_element003,S_element005,Ca_element004]
  conduct = 2
  density = 1
  expand = 3
  formula = G4_BONE_CORTICAL_ICRP
  name = G4_BONE_CORTICAL_ICRP
  specific = 4
FEATURE [App::DocumentObjectGroupPython] B_element001  label="B_element : 4"  # scripted group (container) (typed FeaturePython)
  n = 4
  ref = B_element
FEATURE [App::DocumentObjectGroupPython] C_element017  label="C_element : 1"  # scripted group (container) (typed FeaturePython)
  n = 1
  ref = C_element
FEATURE [App::DocumentObjectGroupPython] G4_BORON_CARBIDE  # scripted group (container) (typed FeaturePython)
  Dunit = g/cm3
  Dvalue = 2.52
  Group = -> [B_element001,C_element017]
  conduct = 2
  density = 1
  expand = 3
  formula = G4_BORON_CARBIDE
  name = G4_BORON_CARBIDE
  specific = 4
FEATURE [App::DocumentObjectGroupPython] B_element002  label="B_element : 2"  # scripted group (container) (typed FeaturePython)
  n = 2
  ref = B_element
FEATURE [App::DocumentObjectGroupPython] O_element016  label="O_element : 006"  # scripted group (container) (typed FeaturePython)
  n = 3
  ref = O_element
FEATURE [App::DocumentObjectGroupPython] G4_BORON_OXIDE  # scripted group (container) (typed FeaturePython)
  Dunit = g/cm3
  Dvalue = 1.812
  Group = -> [B_element002,O_element016]
  conduct = 2
  density = 1
  expand = 3
  formula = G4_BORON_OXIDE
  name = G4_BORON_OXIDE
  specific = 4
FEATURE [App::DocumentObjectGroupPython] H_element017  label="H_element : 0.107"  # scripted group (container) (typed FeaturePython)
  n = 0.107
FEATURE [App::DocumentObjectGroupPython] C_element018  label="C_element : 0.145"  # scripted group (container) (typed FeaturePython)
  n = 0.145
FEATURE [App::DocumentObjectGroupPython] N_element012  label="N_element : 0.022"  # scripted group (container) (typed FeaturePython)
  n = 0.022
FEATURE [App::DocumentObjectGroupPython] O_element017  label="O_element : 0.712"  # scripted group (container) (typed FeaturePython)
  n = 0.712
FEATURE [App::DocumentObjectGroupPython] Na_element004  label="Na_element : 0.004"  # scripted group (container) (typed FeaturePython)
  n = 0.002
FEATURE [App::DocumentObjectGroupPython] P_element004  label="P_element : 0.004"  # scripted group (container) (typed FeaturePython)
  n = 0.004
FEATURE [App::DocumentObjectGroupPython] S_element006  label="S_element : 0.005"  # scripted group (container) (typed FeaturePython)
  n = 0.002
FEATURE [App::DocumentObjectGroupPython] Cl_element003  label="Cl_element : 0.004"  # scripted group (container) (typed FeaturePython)
  n = 0.003
FEATURE [App::DocumentObjectGroupPython] K_element002  label="K_element : 0.003"  # scripted group (container) (typed FeaturePython)
  n = 0.003
FEATURE [App::DocumentObjectGroupPython] G4_BRAIN_ICRP  # scripted group (container) (typed FeaturePython)
  Dunit = g/cm3
  Dvalue = 1.04
  Group = -> [H_element017,C_element018,N_element012,O_element017,Na_element004,P_element004,S_element006,Cl_element003,K_element002]
  conduct = 2
  density = 1
  expand = 3
  formula = G4_BRAIN_ICRP
  name = G4_BRAIN_ICRP
  specific = 4
FEATURE [App::DocumentObjectGroupPython] C_element019  label="C_element : 4"  # scripted group (container) (typed FeaturePython)
  n = 4
  ref = C_element
FEATURE [App::DocumentObjectGroupPython] H_element018  label="H_element : 010"  # scripted group (container) (typed FeaturePython)
  n = 10
  ref = H_element
FEATURE [App::DocumentObjectGroupPython] G4_BUTANE  # scripted group (container) (typed FeaturePython)
  Dunit = g/cm3
  Dvalue = 0.00249343
  Group = -> [C_element019,H_element018]
  conduct = 2
  density = 1
  expand = 3
  formula = G4_BUTANE
  name = G4_BUTANE
  specific = 4
FEATURE [App::DocumentObjectGroupPython] C_element020  label="C_element : 008"  # scripted group (container) (typed FeaturePython)
  n = 4
  ref = C_element
FEATURE [App::DocumentObjectGroupPython] H_element019  label="H_element : 011"  # scripted group (container) (typed FeaturePython)
  n = 10
  ref = H_element
FEATURE [App::DocumentObjectGroupPython] O_element018  label="O_element : 007"  # scripted group (container) (typed FeaturePython)
  n = 1
  ref = O_element
FEATURE [App::DocumentObjectGroupPython] G4_N_BUTYL_ALCOHOL  label="G4_N-BUTYL_ALCOHOL"  # scripted group (container) (typed FeaturePython)
  Dunit = g/cm3
  Dvalue = 0.8098
  Group = -> [C_element020,H_element019,O_element018]
  conduct = 2
  density = 1
  expand = 3
  formula = G4_N-BUTYL_ALCOHOL
  name = G4_N-BUTYL_ALCOHOL
  specific = 4
FEATURE [App::DocumentObjectGroupPython] H_element020  label="H_element : 0.025"  # scripted group (container) (typed FeaturePython)
  n = 0.02468
FEATURE [App::DocumentObjectGroupPython] C_element021  label="C_element : 0.502"  # scripted group (container) (typed FeaturePython)
  n = 0.501611
FEATURE [App::DocumentObjectGroupPython] O_element019  label="O_element : 0.005"  # scripted group (container) (typed FeaturePython)
  n = 0.004527
FEATURE [App::DocumentObjectGroupPython] F_element004  label="F_element : 0.465"  # scripted group (container) (typed FeaturePython)
  n = 0.465209
FEATURE [App::DocumentObjectGroupPython] Si_element001  label="Si_element : 0.004"  # scripted group (container) (typed FeaturePython)
  n = 0.003973
FEATURE [App::DocumentObjectGroupPython] G4_C_552  label="G4_C-552"  # scripted group (container) (typed FeaturePython)
  Dunit = g/cm3
  Dvalue = 1.76
  Group = -> [H_element020,C_element021,O_element019,F_element004,Si_element001]
  conduct = 2
  density = 1
  expand = 3
  formula = G4_C-552
  name = G4_C-552
  specific = 4
FEATURE [App::DocumentObjectGroupPython] Cd_element001  label="Cd_element : 1"  # scripted group (container) (typed FeaturePython)
  n = 1
  ref = Cd_element
FEATURE [App::DocumentObjectGroupPython] Te_element001  label="Te_element : 1"  # scripted group (container) (typed FeaturePython)
  n = 1
  ref = Te_element
FEATURE [App::DocumentObjectGroupPython] G4_CADMIUM_TELLURIDE  # scripted group (container) (typed FeaturePython)
  Dunit = g/cm3
  Dvalue = 6.2
  Group = -> [Cd_element001,Te_element001]
  conduct = 2
  density = 1
  expand = 3
  formula = G4_CADMIUM_TELLURIDE
  name = G4_CADMIUM_TELLURIDE
  specific = 4
FEATURE [App::DocumentObjectGroupPython] Cd_element002  label="Cd_element : 002"  # scripted group (container) (typed FeaturePython)
  n = 1
  ref = Cd_element
FEATURE [App::DocumentObjectGroupPython] W_element001  label="W_element : 1"  # scripted group (container) (typed FeaturePython)
  n = 1
  ref = W_element
FEATURE [App::DocumentObjectGroupPython] O_element020  label="O_element : 008"  # scripted group (container) (typed FeaturePython)
  n = 4
  ref = O_element
FEATURE [App::DocumentObjectGroupPython] G4_CADMIUM_TUNGSTATE  # scripted group (container) (typed FeaturePython)
  Dunit = g/cm3
  Dvalue = 7.9
  Group = -> [Cd_element002,W_element001,O_element020]
  conduct = 2
  density = 1
  expand = 3
  formula = G4_CADMIUM_TUNGSTATE
  name = G4_CADMIUM_TUNGSTATE
  specific = 4
FEATURE [App::DocumentObjectGroupPython] Ca_element005  label="Ca_element : 1"  # scripted group (container) (typed FeaturePython)
  n = 1
  ref = Ca_element
FEATURE [App::DocumentObjectGroupPython] C_element022  label="C_element : 009"  # scripted group (container) (typed FeaturePython)
  n = 1
  ref = C_element
FEATURE [App::DocumentObjectGroupPython] O_element021  label="O_element : 009"  # scripted group (container) (typed FeaturePython)
  n = 3
  ref = O_element
FEATURE [App::DocumentObjectGroupPython] G4_CALCIUM_CARBONATE  # scripted group (container) (typed FeaturePython)
  Dunit = g/cm3
  Dvalue = 2.8
  Group = -> [Ca_element005,C_element022,O_element021]
  conduct = 2
  density = 1
  expand = 3
  formula = G4_CALCIUM_CARBONATE
  name = G4_CALCIUM_CARBONATE
  specific = 4
FEATURE [App::DocumentObjectGroupPython] Ca_element006  label="Ca_element : 002"  # scripted group (container) (typed FeaturePython)
  n = 1
  ref = Ca_element
FEATURE [App::DocumentObjectGroupPython] F_element005  label="F_element : 003"  # scripted group (container) (typed FeaturePython)
  n = 2
  ref = F_element
FEATURE [App::DocumentObjectGroupPython] G4_CALCIUM_FLUORIDE  # scripted group (container) (typed FeaturePython)
  Dunit = g/cm3
  Dvalue = 3.18
  Group = -> [Ca_element006,F_element005]
  conduct = 2
  density = 1
  expand = 3
  formula = G4_CALCIUM_FLUORIDE
  name = G4_CALCIUM_FLUORIDE
  specific = 4
FEATURE [App::DocumentObjectGroupPython] Ca_element007  label="Ca_element : 003"  # scripted group (container) (typed FeaturePython)
  n = 1
  ref = Ca_element
FEATURE [App::DocumentObjectGroupPython] O_element022  label="O_element : 010"  # scripted group (container) (typed FeaturePython)
  n = 1
  ref = O_element
FEATURE [App::DocumentObjectGroupPython] G4_CALCIUM_OXIDE  # scripted group (container) (typed FeaturePython)
  Dunit = g/cm3
  Dvalue = 3.3
  Group = -> [Ca_element007,O_element022]
  conduct = 2
  density = 1
  expand = 3
  formula = G4_CALCIUM_OXIDE
  name = G4_CALCIUM_OXIDE
  specific = 4
FEATURE [App::DocumentObjectGroupPython] Ca_element008  label="Ca_element : 004"  # scripted group (container) (typed FeaturePython)
  n = 1
  ref = Ca_element
FEATURE [App::DocumentObjectGroupPython] S_element007  label="S_element : 002"  # scripted group (container) (typed FeaturePython)
  n = 1
  ref = S_element
FEATURE [App::DocumentObjectGroupPython] O_element023  label="O_element : 011"  # scripted group (container) (typed FeaturePython)
  n = 4
  ref = O_element
FEATURE [App::DocumentObjectGroupPython] G4_CALCIUM_SULFATE  # scripted group (container) (typed FeaturePython)
  Dunit = g/cm3
  Dvalue = 2.96
  Group = -> [Ca_element008,S_element007,O_element023]
  conduct = 2
  density = 1
  expand = 3
  formula = G4_CALCIUM_SULFATE
  name = G4_CALCIUM_SULFATE
  specific = 4
FEATURE [App::DocumentObjectGroupPython] Ca_element009  label="Ca_element : 005"  # scripted group (container) (typed FeaturePython)
  n = 1
  ref = Ca_element
FEATURE [App::DocumentObjectGroupPython] W_element002  label="W_element : 002"  # scripted group (container) (typed FeaturePython)
  n = 1
  ref = W_element
FEATURE [App::DocumentObjectGroupPython] O_element024  label="O_element : 012"  # scripted group (container) (typed FeaturePython)
  n = 4
  ref = O_element
FEATURE [App::DocumentObjectGroupPython] G4_CALCIUM_TUNGSTATE  # scripted group (container) (typed FeaturePython)
  Dunit = g/cm3
  Dvalue = 6.062
  Group = -> [Ca_element009,W_element002,O_element024]
  conduct = 2
  density = 1
  expand = 3
  formula = G4_CALCIUM_TUNGSTATE
  name = G4_CALCIUM_TUNGSTATE
  specific = 4
FEATURE [App::DocumentObjectGroupPython] C_element023  label="C_element : 010"  # scripted group (container) (typed FeaturePython)
  n = 1
  ref = C_element
FEATURE [App::DocumentObjectGroupPython] O_element025  label="O_element : 013"  # scripted group (container) (typed FeaturePython)
  n = 2
  ref = O_element
FEATURE [App::DocumentObjectGroupPython] G4_CARBON_DIOXIDE  # scripted group (container) (typed FeaturePython)
  Dunit = g/cm3
  Dvalue = 0.00184212
  Group = -> [C_element023,O_element025]
  conduct = 2
  density = 1
  expand = 3
  formula = G4_CARBON_DIOXIDE
  name = G4_CARBON_DIOXIDE
  specific = 4
FEATURE [App::DocumentObjectGroupPython] C_element024  label="C_element : 011"  # scripted group (container) (typed FeaturePython)
  n = 1
  ref = C_element
FEATURE [App::DocumentObjectGroupPython] Cl_element004  label="Cl_element : 4"  # scripted group (container) (typed FeaturePython)
  n = 4
  ref = Cl_element
FEATURE [App::DocumentObjectGroupPython] G4_CARBON_TETRACHLORIDE  # scripted group (container) (typed FeaturePython)
  Dunit = g/cm3
  Dvalue = 1.594
  Group = -> [C_element024,Cl_element004]
  conduct = 2
  density = 1
  expand = 3
  formula = G4_CARBON_TETRACHLORIDE
  name = G4_CARBON_TETRACHLORIDE
  specific = 4
FEATURE [App::DocumentObjectGroupPython] C_element025  label="C_element : 012"  # scripted group (container) (typed FeaturePython)
  n = 6
  ref = C_element
FEATURE [App::DocumentObjectGroupPython] H_element021  label="H_element : 012"  # scripted group (container) (typed FeaturePython)
  n = 10
  ref = H_element
FEATURE [App::DocumentObjectGroupPython] O_element026  label="O_element : 5"  # scripted group (container) (typed FeaturePython)
  n = 5
  ref = O_element
FEATURE [App::DocumentObjectGroupPython] G4_CELLULOSE_CELLOPHANE  # scripted group (container) (typed FeaturePython)
  Dunit = g/cm3
  Dvalue = 1.42
  Group = -> [C_element025,H_element021,O_element026]
  conduct = 2
  density = 1
  expand = 3
  formula = G4_CELLULOSE_CELLOPHANE
  name = G4_CELLULOSE_CELLOPHANE
  specific = 4
FEATURE [App::DocumentObjectGroupPython] H_element022  label="H_element : 0.067"  # scripted group (container) (typed FeaturePython)
  n = 0.067125
FEATURE [App::DocumentObjectGroupPython] C_element026  label="C_element : 0.545"  # scripted group (container) (typed FeaturePython)
  n = 0.545403
FEATURE [App::DocumentObjectGroupPython] O_element027  label="O_element : 0.387"  # scripted group (container) (typed FeaturePython)
  n = 0.387472
FEATURE [App::DocumentObjectGroupPython] G4_CELLULOSE_BUTYRATE  # scripted group (container) (typed FeaturePython)
  Dunit = g/cm3
  Dvalue = 1.2
  Group = -> [H_element022,C_element026,O_element027]
  conduct = 2
  density = 1
  expand = 3
  formula = G4_CELLULOSE_BUTYRATE
  name = G4_CELLULOSE_BUTYRATE
  specific = 4
FEATURE [App::DocumentObjectGroupPython] H_element023  label="H_element : 0.029"  # scripted group (container) (typed FeaturePython)
  n = 0.029216
FEATURE [App::DocumentObjectGroupPython] C_element027  label="C_element : 0.271"  # scripted group (container) (typed FeaturePython)
  n = 0.271296
FEATURE [App::DocumentObjectGroupPython] N_element013  label="N_element : 0.121"  # scripted group (container) (typed FeaturePython)
  n = 0.121276
FEATURE [App::DocumentObjectGroupPython] O_element028  label="O_element : 0.578"  # scripted group (container) (typed FeaturePython)
  n = 0.578212
FEATURE [App::DocumentObjectGroupPython] G4_CELLULOSE_NITRATE  # scripted group (container) (typed FeaturePython)
  Dunit = g/cm3
  Dvalue = 1.49
  Group = -> [H_element023,C_element027,N_element013,O_element028]
  conduct = 2
  density = 1
  expand = 3
  formula = G4_CELLULOSE_NITRATE
  name = G4_CELLULOSE_NITRATE
  specific = 4
FEATURE [App::DocumentObjectGroupPython] H_element024  label="H_element : 0.108"  # scripted group (container) (typed FeaturePython)
  n = 0.107596
FEATURE [App::DocumentObjectGroupPython] N_element014  label="N_element : 0.001"  # scripted group (container) (typed FeaturePython)
  n = 0.0008
FEATURE [App::DocumentObjectGroupPython] O_element029  label="O_element : 0.875"  # scripted group (container) (typed FeaturePython)
  n = 0.874976
FEATURE [App::DocumentObjectGroupPython] S_element008  label="S_element : 0.015"  # scripted group (container) (typed FeaturePython)
  n = 0.014627
FEATURE [App::DocumentObjectGroupPython] Ce_element001  label="Ce_element : 0.002"  # scripted group (container) (typed FeaturePython)
  n = 0.002001
FEATURE [App::DocumentObjectGroupPython] G4_CERIC_SULFATE  # scripted group (container) (typed FeaturePython)
  Dunit = g/cm3
  Dvalue = 1.03
  Group = -> [H_element024,N_element014,O_element029,S_element008,Ce_element001]
  conduct = 2
  density = 1
  expand = 3
  formula = G4_CERIC_SULFATE
  name = G4_CERIC_SULFATE
  specific = 4
FEATURE [App::DocumentObjectGroupPython] Cs_element001  label="Cs_element : 1"  # scripted group (container) (typed FeaturePython)
  n = 1
  ref = Cs_element
FEATURE [App::DocumentObjectGroupPython] F_element006  label="F_element : 1"  # scripted group (container) (typed FeaturePython)
  n = 1
  ref = F_element
FEATURE [App::DocumentObjectGroupPython] G4_CESIUM_FLUORIDE  # scripted group (container) (typed FeaturePython)
  Dunit = g/cm3
  Dvalue = 4.115
  Group = -> [Cs_element001,F_element006]
  conduct = 2
  density = 1
  expand = 3
  formula = G4_CESIUM_FLUORIDE
  name = G4_CESIUM_FLUORIDE
  specific = 4
FEATURE [App::DocumentObjectGroupPython] Cs_element002  label="Cs_element : 002"  # scripted group (container) (typed FeaturePython)
  n = 1
  ref = Cs_element
FEATURE [App::DocumentObjectGroupPython] I_element001  label="I_element : 1"  # scripted group (container) (typed FeaturePython)
  n = 1
  ref = I_element
FEATURE [App::DocumentObjectGroupPython] G4_CESIUM_IODIDE  # scripted group (container) (typed FeaturePython)
  Dunit = g/cm3
  Dvalue = 4.51
  Group = -> [Cs_element002,I_element001]
  conduct = 2
  density = 1
  expand = 3
  formula = G4_CESIUM_IODIDE
  name = G4_CESIUM_IODIDE
  specific = 4
FEATURE [App::DocumentObjectGroupPython] C_element028  label="C_element : 013"  # scripted group (container) (typed FeaturePython)
  n = 6
  ref = C_element
FEATURE [App::DocumentObjectGroupPython] H_element025  label="H_element : 013"  # scripted group (container) (typed FeaturePython)
  n = 5
  ref = H_element
FEATURE [App::DocumentObjectGroupPython] Cl_element005  label="Cl_element : 1"  # scripted group (container) (typed FeaturePython)
  n = 1
  ref = Cl_element
FEATURE [App::DocumentObjectGroupPython] G4_CHLOROBENZENE  # scripted group (container) (typed FeaturePython)
  Dunit = g/cm3
  Dvalue = 1.1058
  Group = -> [C_element028,H_element025,Cl_element005]
  conduct = 2
  density = 1
  expand = 3
  formula = G4_CHLOROBENZENE
  name = G4_CHLOROBENZENE
  specific = 4
FEATURE [App::DocumentObjectGroupPython] C_element029  label="C_element : 014"  # scripted group (container) (typed FeaturePython)
  n = 1
  ref = C_element
FEATURE [App::DocumentObjectGroupPython] H_element026  label="H_element : 1"  # scripted group (container) (typed FeaturePython)
  n = 1
  ref = H_element
FEATURE [App::DocumentObjectGroupPython] Cl_element006  label="Cl_element : 3"  # scripted group (container) (typed FeaturePython)
  n = 3
  ref = Cl_element
FEATURE [App::DocumentObjectGroupPython] G4_CHLOROFORM  # scripted group (container) (typed FeaturePython)
  Dunit = g/cm3
  Dvalue = 1.4832
  Group = -> [C_element029,H_element026,Cl_element006]
  conduct = 2
  density = 1
  expand = 3
  formula = G4_CHLOROFORM
  name = G4_CHLOROFORM
  specific = 4
FEATURE [App::DocumentObjectGroupPython] H_element027  label="H_element : 0.010"  # scripted group (container) (typed FeaturePython)
  n = 0.01
FEATURE [App::DocumentObjectGroupPython] C_element030  label="C_element : 0.001"  # scripted group (container) (typed FeaturePython)
  n = 0.001
FEATURE [App::DocumentObjectGroupPython] O_element030  label="O_element : 0.529"  # scripted group (container) (typed FeaturePython)
  n = 0.529107
FEATURE [App::DocumentObjectGroupPython] Na_element005  label="Na_element : 0.016"  # scripted group (container) (typed FeaturePython)
  n = 0.016
FEATURE [App::DocumentObjectGroupPython] Mg_element003  label="Mg_element : 0.004"  # scripted group (container) (typed FeaturePython)
  n = 0.002
FEATURE [App::DocumentObjectGroupPython] Al_element002  label="Al_element : 0.034"  # scripted group (container) (typed FeaturePython)
  n = 0.033872
FEATURE [App::DocumentObjectGroupPython] Si_element002  label="Si_element : 0.337"  # scripted group (container) (typed FeaturePython)
  n = 0.337021
FEATURE [App::DocumentObjectGroupPython] K_element003  label="K_element : 0.013"  # scripted group (container) (typed FeaturePython)
  n = 0.013
FEATURE [App::DocumentObjectGroupPython] Ca_element010  label="Ca_element : 0.044"  # scripted group (container) (typed FeaturePython)
  n = 0.044
FEATURE [App::DocumentObjectGroupPython] Fe_element002  label="Fe_element : 0.014"  # scripted group (container) (typed FeaturePython)
  n = 0.014
FEATURE [App::DocumentObjectGroupPython] G4_CONCRETE  # scripted group (container) (typed FeaturePython)
  Dunit = g/cm3
  Dvalue = 2.3
  Group = -> [H_element027,C_element030,O_element030,Na_element005,Mg_element003,Al_element002,Si_element002,K_element003,Ca_element010,Fe_element002]
  conduct = 2
  density = 1
  expand = 3
  formula = G4_CONCRETE
  name = G4_CONCRETE
  specific = 4
FEATURE [App::DocumentObjectGroupPython] C_element031  label="C_element : 015"  # scripted group (container) (typed FeaturePython)
  n = 6
  ref = C_element
FEATURE [App::DocumentObjectGroupPython] H_element028  label="H_element : 12"  # scripted group (container) (typed FeaturePython)
  n = 12
  ref = H_element
FEATURE [App::DocumentObjectGroupPython] G4_CYCLOHEXANE  # scripted group (container) (typed FeaturePython)
  Dunit = g/cm3
  Dvalue = 0.779
  Group = -> [C_element031,H_element028]
  conduct = 2
  density = 1
  expand = 3
  formula = G4_CYCLOHEXANE
  name = G4_CYCLOHEXANE
  specific = 4
FEATURE [App::DocumentObjectGroupPython] C_element032  label="C_element : 016"  # scripted group (container) (typed FeaturePython)
  n = 6
  ref = C_element
FEATURE [App::DocumentObjectGroupPython] H_element029  label="H_element : 4"  # scripted group (container) (typed FeaturePython)
  n = 4
  ref = H_element
FEATURE [App::DocumentObjectGroupPython] Cl_element007  label="Cl_element : 2"  # scripted group (container) (typed FeaturePython)
  n = 2
  ref = Cl_element
FEATURE [App::DocumentObjectGroupPython] G4_1_2_DICHLOROBENZENE  label="G4_1.2-DICHLOROBENZENE"  # scripted group (container) (typed FeaturePython)
  Dunit = g/cm3
  Dvalue = 1.3048
  Group = -> [C_element032,H_element029,Cl_element007]
  conduct = 2
  density = 1
  expand = 3
  formula = G4_1.2-DICHLOROBENZENE
  name = G4_1.2-DICHLOROBENZENE
  specific = 4
FEATURE [App::DocumentObjectGroupPython] C_element033  label="C_element : 017"  # scripted group (container) (typed FeaturePython)
  n = 4
  ref = C_element
FEATURE [App::DocumentObjectGroupPython] H_element030  label="H_element : 8"  # scripted group (container) (typed FeaturePython)
  n = 8
  ref = H_element
FEATURE [App::DocumentObjectGroupPython] O_element031  label="O_element : 014"  # scripted group (container) (typed FeaturePython)
  n = 1
  ref = O_element
FEATURE [App::DocumentObjectGroupPython] Cl_element008  label="Cl_element : 005"  # scripted group (container) (typed FeaturePython)
  n = 2
  ref = Cl_element
FEATURE [App::DocumentObjectGroupPython] G4_DICHLORODIETHYL_ETHER  # scripted group (container) (typed FeaturePython)
  Dunit = g/cm3
  Dvalue = 1.2199
  Group = -> [C_element033,H_element030,O_element031,Cl_element008]
  conduct = 2
  density = 1
  expand = 3
  formula = G4_DICHLORODIETHYL_ETHER
  name = G4_DICHLORODIETHYL_ETHER
  specific = 4
FEATURE [App::DocumentObjectGroupPython] C_element034  label="C_element : 018"  # scripted group (container) (typed FeaturePython)
  n = 2
  ref = C_element
FEATURE [App::DocumentObjectGroupPython] H_element031  label="H_element : 014"  # scripted group (container) (typed FeaturePython)
  n = 4
  ref = H_element
FEATURE [App::DocumentObjectGroupPython] Cl_element009  label="Cl_element : 006"  # scripted group (container) (typed FeaturePython)
  n = 2
  ref = Cl_element
FEATURE [App::DocumentObjectGroupPython] G4_1_2_DICHLOROETHANE  label="G4_1.2-DICHLOROETHANE"  # scripted group (container) (typed FeaturePython)
  Dunit = g/cm3
  Dvalue = 1.2351
  Group = -> [C_element034,H_element031,Cl_element009]
  conduct = 2
  density = 1
  expand = 3
  formula = G4_1.2-DICHLOROETHANE
  name = G4_1.2-DICHLOROETHANE
  specific = 4
FEATURE [App::DocumentObjectGroupPython] C_element035  label="C_element : 019"  # scripted group (container) (typed FeaturePython)
  n = 4
  ref = C_element
FEATURE [App::DocumentObjectGroupPython] H_element032  label="H_element : 015"  # scripted group (container) (typed FeaturePython)
  n = 10
  ref = H_element
FEATURE [App::DocumentObjectGroupPython] O_element032  label="O_element : 015"  # scripted group (container) (typed FeaturePython)
  n = 1
  ref = O_element
FEATURE [App::DocumentObjectGroupPython] G4_DIETHYL_ETHER  # scripted group (container) (typed FeaturePython)
  Dunit = g/cm3
  Dvalue = 0.71378
  Group = -> [C_element035,H_element032,O_element032]
  conduct = 2
  density = 1
  expand = 3
  formula = G4_DIETHYL_ETHER
  name = G4_DIETHYL_ETHER
  specific = 4
FEATURE [App::DocumentObjectGroupPython] C_element036  label="C_element : 020"  # scripted group (container) (typed FeaturePython)
  n = 3
  ref = C_element
FEATURE [App::DocumentObjectGroupPython] H_element033  label="H_element : 016"  # scripted group (container) (typed FeaturePython)
  n = 7
  ref = H_element
FEATURE [App::DocumentObjectGroupPython] N_element015  label="N_element : 008"  # scripted group (container) (typed FeaturePython)
  n = 1
  ref = N_element
FEATURE [App::DocumentObjectGroupPython] O_element033  label="O_element : 016"  # scripted group (container) (typed FeaturePython)
  n = 1
  ref = O_element
FEATURE [App::DocumentObjectGroupPython] G4_N_N_DIMETHYL_FORMAMIDE  label="G4_N.N-DIMETHYL_FORMAMIDE"  # scripted group (container) (typed FeaturePython)
  Dunit = g/cm3
  Dvalue = 0.9487
  Group = -> [C_element036,H_element033,N_element015,O_element033]
  conduct = 2
  density = 1
  expand = 3
  formula = G4_N.N-DIMETHYL_FORMAMIDE
  name = G4_N.N-DIMETHYL_FORMAMIDE
  specific = 4
FEATURE [App::DocumentObjectGroupPython] C_element037  label="C_element : 021"  # scripted group (container) (typed FeaturePython)
  n = 2
  ref = C_element
FEATURE [App::DocumentObjectGroupPython] H_element034  label="H_element : 017"  # scripted group (container) (typed FeaturePython)
  n = 6
  ref = H_element
FEATURE [App::DocumentObjectGroupPython] O_element034  label="O_element : 017"  # scripted group (container) (typed FeaturePython)
  n = 1
  ref = O_element
FEATURE [App::DocumentObjectGroupPython] S_element009  label="S_element : 003"  # scripted group (container) (typed FeaturePython)
  n = 1
  ref = S_element
FEATURE [App::DocumentObjectGroupPython] G4_DIMETHYL_SULFOXIDE  # scripted group (container) (typed FeaturePython)
  Dunit = g/cm3
  Dvalue = 1.1014
  Group = -> [C_element037,H_element034,O_element034,S_element009]
  conduct = 2
  density = 1
  expand = 3
  formula = G4_DIMETHYL_SULFOXIDE
  name = G4_DIMETHYL_SULFOXIDE
  specific = 4
FEATURE [App::DocumentObjectGroupPython] C_element038  label="C_element : 022"  # scripted group (container) (typed FeaturePython)
  n = 2
  ref = C_element
FEATURE [App::DocumentObjectGroupPython] H_element035  label="H_element : 018"  # scripted group (container) (typed FeaturePython)
  n = 6
  ref = H_element
FEATURE [App::DocumentObjectGroupPython] G4_ETHANE  # scripted group (container) (typed FeaturePython)
  Dunit = g/cm3
  Dvalue = 0.00125324
  Group = -> [C_element038,H_element035]
  conduct = 2
  density = 1
  expand = 3
  formula = G4_ETHANE
  name = G4_ETHANE
  specific = 4
FEATURE [App::DocumentObjectGroupPython] C_element039  label="C_element : 023"  # scripted group (container) (typed FeaturePython)
  n = 2
  ref = C_element
FEATURE [App::DocumentObjectGroupPython] H_element036  label="H_element : 019"  # scripted group (container) (typed FeaturePython)
  n = 6
  ref = H_element
FEATURE [App::DocumentObjectGroupPython] O_element035  label="O_element : 018"  # scripted group (container) (typed FeaturePython)
  n = 1
  ref = O_element
FEATURE [App::DocumentObjectGroupPython] G4_ETHYL_ALCOHOL  # scripted group (container) (typed FeaturePython)
  Dunit = g/cm3
  Dvalue = 0.7893
  Group = -> [C_element039,H_element036,O_element035]
  conduct = 2
  density = 1
  expand = 3
  formula = G4_ETHYL_ALCOHOL
  name = G4_ETHYL_ALCOHOL
  specific = 4
FEATURE [App::DocumentObjectGroupPython] H_element037  label="H_element : 0.090"  # scripted group (container) (typed FeaturePython)
  n = 0.090027
FEATURE [App::DocumentObjectGroupPython] C_element040  label="C_element : 0.585"  # scripted group (container) (typed FeaturePython)
  n = 0.585182
FEATURE [App::DocumentObjectGroupPython] O_element036  label="O_element : 0.325"  # scripted group (container) (typed FeaturePython)
  n = 0.324791
FEATURE [App::DocumentObjectGroupPython] G4_ETHYL_CELLULOSE  # scripted group (container) (typed FeaturePython)
  Dunit = g/cm3
  Dvalue = 1.13
  Group = -> [H_element037,C_element040,O_element036]
  conduct = 2
  density = 1
  expand = 3
  formula = G4_ETHYL_CELLULOSE
  name = G4_ETHYL_CELLULOSE
  specific = 4
FEATURE [App::DocumentObjectGroupPython] C_element041  label="C_element : 024"  # scripted group (container) (typed FeaturePython)
  n = 2
  ref = C_element
FEATURE [App::DocumentObjectGroupPython] H_element038  label="H_element : 020"  # scripted group (container) (typed FeaturePython)
  n = 4
  ref = H_element
FEATURE [App::DocumentObjectGroupPython] G4_ETHYLENE  # scripted group (container) (typed FeaturePython)
  Dunit = g/cm3
  Dvalue = 0.00117497
  Group = -> [C_element041,H_element038]
  conduct = 2
  density = 1
  expand = 3
  formula = G4_ETHYLENE
  name = G4_ETHYLENE
  specific = 4
FEATURE [App::DocumentObjectGroupPython] H_element039  label="H_element : 0.096"  # scripted group (container) (typed FeaturePython)
  n = 0.096
FEATURE [App::DocumentObjectGroupPython] C_element042  label="C_element : 0.195"  # scripted group (container) (typed FeaturePython)
  n = 0.195
FEATURE [App::DocumentObjectGroupPython] N_element016  label="N_element : 0.057"  # scripted group (container) (typed FeaturePython)
  n = 0.057
FEATURE [App::DocumentObjectGroupPython] O_element037  label="O_element : 0.646"  # scripted group (container) (typed FeaturePython)
  n = 0.646
FEATURE [App::DocumentObjectGroupPython] Na_element006  label="Na_element : 0.017"  # scripted group (container) (typed FeaturePython)
  n = 0.001
FEATURE [App::DocumentObjectGroupPython] P_element005  label="P_element : 0.104"  # scripted group (container) (typed FeaturePython)
  n = 0.001
FEATURE [App::DocumentObjectGroupPython] S_element010  label="S_element : 0.016"  # scripted group (container) (typed FeaturePython)
  n = 0.003
FEATURE [App::DocumentObjectGroupPython] Cl_element010  label="Cl_element : 0.005"  # scripted group (container) (typed FeaturePython)
  n = 0.001
FEATURE [App::DocumentObjectGroupPython] G4_EYE_LENS_ICRP  # scripted group (container) (typed FeaturePython)
  Dunit = g/cm3
  Dvalue = 1.07
  Group = -> [H_element039,C_element042,N_element016,O_element037,Na_element006,P_element005,S_element010,Cl_element010]
  conduct = 2
  density = 1
  expand = 3
  formula = G4_EYE_LENS_ICRP
  name = G4_EYE_LENS_ICRP
  specific = 4
FEATURE [App::DocumentObjectGroupPython] Fe_element003  label="Fe_element : 2"  # scripted group (container) (typed FeaturePython)
  n = 2
  ref = Fe_element
FEATURE [App::DocumentObjectGroupPython] O_element038  label="O_element : 019"  # scripted group (container) (typed FeaturePython)
  n = 3
  ref = O_element
FEATURE [App::DocumentObjectGroupPython] G4_FERRIC_OXIDE  # scripted group (container) (typed FeaturePython)
  Dunit = g/cm3
  Dvalue = 5.2
  Group = -> [Fe_element003,O_element038]
  conduct = 2
  density = 1
  expand = 3
  formula = G4_FERRIC_OXIDE
  name = G4_FERRIC_OXIDE
  specific = 4
FEATURE [App::DocumentObjectGroupPython] Fe_element004  label="Fe_element : 1"  # scripted group (container) (typed FeaturePython)
  n = 1
  ref = Fe_element
FEATURE [App::DocumentObjectGroupPython] B_element003  label="B_element : 1"  # scripted group (container) (typed FeaturePython)
  n = 1
  ref = B_element
FEATURE [App::DocumentObjectGroupPython] G4_FERROBORIDE  # scripted group (container) (typed FeaturePython)
  Dunit = g/cm3
  Dvalue = 7.15
  Group = -> [Fe_element004,B_element003]
  conduct = 2
  density = 1
  expand = 3
  formula = G4_FERROBORIDE
  name = G4_FERROBORIDE
  specific = 4
FEATURE [App::DocumentObjectGroupPython] Fe_element005  label="Fe_element : 003"  # scripted group (container) (typed FeaturePython)
  n = 1
  ref = Fe_element
FEATURE [App::DocumentObjectGroupPython] O_element039  label="O_element : 020"  # scripted group (container) (typed FeaturePython)
  n = 1
  ref = O_element
FEATURE [App::DocumentObjectGroupPython] G4_FERROUS_OXIDE  # scripted group (container) (typed FeaturePython)
  Dunit = g/cm3
  Dvalue = 5.7
  Group = -> [Fe_element005,O_element039]
  conduct = 2
  density = 1
  expand = 3
  formula = G4_FERROUS_OXIDE
  name = G4_FERROUS_OXIDE
  specific = 4
FEATURE [App::DocumentObjectGroupPython] H_element040  label="H_element : 0.115"  # scripted group (container) (typed FeaturePython)
  n = 0.108259
FEATURE [App::DocumentObjectGroupPython] N_element017  label="N_element : 0.000"  # scripted group (container) (typed FeaturePython)
  n = 2.7e-05
FEATURE [App::DocumentObjectGroupPython] O_element040  label="O_element : 0.879"  # scripted group (container) (typed FeaturePython)
  n = 0.878636
FEATURE [App::DocumentObjectGroupPython] Na_element007  label="Na_element : 0.000"  # scripted group (container) (typed FeaturePython)
  n = 2.2e-05
FEATURE [App::DocumentObjectGroupPython] S_element011  label="S_element : 0.013"  # scripted group (container) (typed FeaturePython)
  n = 0.012968
FEATURE [App::DocumentObjectGroupPython] Cl_element011  label="Cl_element : 0.000"  # scripted group (container) (typed FeaturePython)
  n = 3.4e-05
FEATURE [App::DocumentObjectGroupPython] Fe_element006  label="Fe_element : 0.000"  # scripted group (container) (typed FeaturePython)
  n = 5.4e-05
FEATURE [App::DocumentObjectGroupPython] G4_FERROUS_SULFATE  # scripted group (container) (typed FeaturePython)
  Dunit = g/cm3
  Dvalue = 1.024
  Group = -> [H_element040,N_element017,O_element040,Na_element007,S_element011,Cl_element011,Fe_element006]
  conduct = 2
  density = 1
  expand = 3
  formula = G4_FERROUS_SULFATE
  name = G4_FERROUS_SULFATE
  specific = 4
FEATURE [App::DocumentObjectGroupPython] C_element043  label="C_element : 0.099"  # scripted group (container) (typed FeaturePython)
  n = 0.099335
FEATURE [App::DocumentObjectGroupPython] F_element007  label="F_element : 0.314"  # scripted group (container) (typed FeaturePython)
  n = 0.314247
FEATURE [App::DocumentObjectGroupPython] Cl_element012  label="Cl_element : 0.586"  # scripted group (container) (typed FeaturePython)
  n = 0.586418
FEATURE [App::DocumentObjectGroupPython] G4_FREON_12  label="G4_FREON-12"  # scripted group (container) (typed FeaturePython)
  Dunit = g/cm3
  Dvalue = 1.12
  Group = -> [C_element043,F_element007,Cl_element012]
  conduct = 2
  density = 1
  expand = 3
  formula = G4_FREON-12
  name = G4_FREON-12
  specific = 4
FEATURE [App::DocumentObjectGroupPython] C_element044  label="C_element : 0.057"  # scripted group (container) (typed FeaturePython)
  n = 0.057245
FEATURE [App::DocumentObjectGroupPython] F_element008  label="F_element : 0.181"  # scripted group (container) (typed FeaturePython)
  n = 0.181096
FEATURE [App::DocumentObjectGroupPython] Br_element001  label="Br_element : 0.762"  # scripted group (container) (typed FeaturePython)
  n = 0.761659
FEATURE [App::DocumentObjectGroupPython] G4_FREON_12B2  label="G4_FREON-12B2"  # scripted group (container) (typed FeaturePython)
  Dunit = g/cm3
  Dvalue = 1.8
  Group = -> [C_element044,F_element008,Br_element001]
  conduct = 2
  density = 1
  expand = 3
  formula = G4_FREON-12B2
  name = G4_FREON-12B2
  specific = 4
FEATURE [App::DocumentObjectGroupPython] C_element045  label="C_element : 0.115"  # scripted group (container) (typed FeaturePython)
  n = 0.114983
FEATURE [App::DocumentObjectGroupPython] F_element009  label="F_element : 0.546"  # scripted group (container) (typed FeaturePython)
  n = 0.545621
FEATURE [App::DocumentObjectGroupPython] Cl_element013  label="Cl_element : 0.339"  # scripted group (container) (typed FeaturePython)
  n = 0.339396
FEATURE [App::DocumentObjectGroupPython] G4_FREON_13  label="G4_FREON-13"  # scripted group (container) (typed FeaturePython)
  Dunit = g/cm3
  Dvalue = 0.95
  Group = -> [C_element045,F_element009,Cl_element013]
  conduct = 2
  density = 1
  expand = 3
  formula = G4_FREON-13
  name = G4_FREON-13
  specific = 4
FEATURE [App::DocumentObjectGroupPython] C_element046  label="C_element : 025"  # scripted group (container) (typed FeaturePython)
  n = 1
  ref = C_element
FEATURE [App::DocumentObjectGroupPython] F_element010  label="F_element : 3"  # scripted group (container) (typed FeaturePython)
  n = 3
  ref = F_element
FEATURE [App::DocumentObjectGroupPython] Br_element002  label="Br_element : 1"  # scripted group (container) (typed FeaturePython)
  n = 1
  ref = Br_element
FEATURE [App::DocumentObjectGroupPython] G4_FREON_13B1  label="G4_FREON-13B1"  # scripted group (container) (typed FeaturePython)
  Dunit = g/cm3
  Dvalue = 1.5
  Group = -> [C_element046,F_element010,Br_element002]
  conduct = 2
  density = 1
  expand = 3
  formula = G4_FREON-13B1
  name = G4_FREON-13B1
  specific = 4
FEATURE [App::DocumentObjectGroupPython] C_element047  label="C_element : 0.061"  # scripted group (container) (typed FeaturePython)
  n = 0.061309
FEATURE [App::DocumentObjectGroupPython] F_element011  label="F_element : 0.291"  # scripted group (container) (typed FeaturePython)
  n = 0.290924
FEATURE [App::DocumentObjectGroupPython] I_element002  label="I_element : 0.648"  # scripted group (container) (typed FeaturePython)
  n = 0.647767
FEATURE [App::DocumentObjectGroupPython] G4_FREON_13I1  label="G4_FREON-13I1"  # scripted group (container) (typed FeaturePython)
  Dunit = g/cm3
  Dvalue = 1.8
  Group = -> [C_element047,F_element011,I_element002]
  conduct = 2
  density = 1
  expand = 3
  formula = G4_FREON-13I1
  name = G4_FREON-13I1
  specific = 4
FEATURE [App::DocumentObjectGroupPython] Gd_element001  label="Gd_element : 2"  # scripted group (container) (typed FeaturePython)
  n = 2
  ref = Gd_element
FEATURE [App::DocumentObjectGroupPython] O_element041  label="O_element : 021"  # scripted group (container) (typed FeaturePython)
  n = 2
  ref = O_element
FEATURE [App::DocumentObjectGroupPython] S_element012  label="S_element : 004"  # scripted group (container) (typed FeaturePython)
  n = 1
  ref = S_element
FEATURE [App::DocumentObjectGroupPython] G4_GADOLINIUM_OXYSULFIDE  # scripted group (container) (typed FeaturePython)
  Dunit = g/cm3
  Dvalue = 7.44
  Group = -> [Gd_element001,O_element041,S_element012]
  conduct = 2
  density = 1
  expand = 3
  formula = G4_GADOLINIUM_OXYSULFIDE
  name = G4_GADOLINIUM_OXYSULFIDE
  specific = 4
FEATURE [App::DocumentObjectGroupPython] Ga_element001  label="Ga_element : 1"  # scripted group (container) (typed FeaturePython)
  n = 1
  ref = Ga_element
FEATURE [App::DocumentObjectGroupPython] As_element001  label="As_element : 1"  # scripted group (container) (typed FeaturePython)
  n = 1
  ref = As_element
FEATURE [App::DocumentObjectGroupPython] G4_GALLIUM_ARSENIDE  # scripted group (container) (typed FeaturePython)
  Dunit = g/cm3
  Dvalue = 5.31
  Group = -> [Ga_element001,As_element001]
  conduct = 2
  density = 1
  expand = 3
  formula = G4_GALLIUM_ARSENIDE
  name = G4_GALLIUM_ARSENIDE
  specific = 4
FEATURE [App::DocumentObjectGroupPython] H_element041  label="H_element : 0.081"  # scripted group (container) (typed FeaturePython)
  n = 0.08118
FEATURE [App::DocumentObjectGroupPython] C_element048  label="C_element : 0.416"  # scripted group (container) (typed FeaturePython)
  n = 0.41606
FEATURE [App::DocumentObjectGroupPython] N_element018  label="N_element : 0.111"  # scripted group (container) (typed FeaturePython)
  n = 0.11124
FEATURE [App::DocumentObjectGroupPython] O_element042  label="O_element : 0.381"  # scripted group (container) (typed FeaturePython)
  n = 0.38064
FEATURE [App::DocumentObjectGroupPython] S_element013  label="S_element : 0.011"  # scripted group (container) (typed FeaturePython)
  n = 0.01088
FEATURE [App::DocumentObjectGroupPython] G4_GEL_PHOTO_EMULSION  # scripted group (container) (typed FeaturePython)
  Dunit = g/cm3
  Dvalue = 1.2914
  Group = -> [H_element041,C_element048,N_element018,O_element042,S_element013]
  conduct = 2
  density = 1
  expand = 3
  formula = G4_GEL_PHOTO_EMULSION
  name = G4_GEL_PHOTO_EMULSION
  specific = 4
FEATURE [App::DocumentObjectGroupPython] B_element004  label="B_element : 0.040"  # scripted group (container) (typed FeaturePython)
  n = 0.0400639
FEATURE [App::DocumentObjectGroupPython] O_element043  label="O_element : 0.540"  # scripted group (container) (typed FeaturePython)
  n = 0.539561
FEATURE [App::DocumentObjectGroupPython] Na_element008  label="Na_element : 0.028"  # scripted group (container) (typed FeaturePython)
  n = 0.0281909
FEATURE [App::DocumentObjectGroupPython] Al_element003  label="Al_element : 0.012"  # scripted group (container) (typed FeaturePython)
  n = 0.011644
FEATURE [App::DocumentObjectGroupPython] Si_element003  label="Si_element : 0.377"  # scripted group (container) (typed FeaturePython)
  n = 0.377219
FEATURE [App::DocumentObjectGroupPython] K_element004  label="K_element : 0.014"  # scripted group (container) (typed FeaturePython)
  n = 0.00332099
FEATURE [App::DocumentObjectGroupPython] G4_Pyrex_Glass  # scripted group (container) (typed FeaturePython)
  Dunit = g/cm3
  Dvalue = 2.23
  Group = -> [B_element004,O_element043,Na_element008,Al_element003,Si_element003,K_element004]
  conduct = 2
  density = 1
  expand = 3
  formula = G4_Pyrex_Glass
  name = G4_Pyrex_Glass
  specific = 4
FEATURE [App::DocumentObjectGroupPython] O_element044  label="O_element : 0.156"  # scripted group (container) (typed FeaturePython)
  n = 0.156453
FEATURE [App::DocumentObjectGroupPython] Si_element004  label="Si_element : 0.081"  # scripted group (container) (typed FeaturePython)
  n = 0.080866
FEATURE [App::DocumentObjectGroupPython] Ti_element001  label="Ti_element : 0.008"  # scripted group (container) (typed FeaturePython)
  n = 0.008092
FEATURE [App::DocumentObjectGroupPython] As_element002  label="As_element : 0.003"  # scripted group (container) (typed FeaturePython)
  n = 0.002651
FEATURE [App::DocumentObjectGroupPython] Pb_element001  label="Pb_element : 0.752"  # scripted group (container) (typed FeaturePython)
  n = 0.751938
FEATURE [App::DocumentObjectGroupPython] G4_GLASS_LEAD  # scripted group (container) (typed FeaturePython)
  Dunit = g/cm3
  Dvalue = 6.22
  Group = -> [O_element044,Si_element004,Ti_element001,As_element002,Pb_element001]
  conduct = 2
  density = 1
  expand = 3
  formula = G4_GLASS_LEAD
  name = G4_GLASS_LEAD
  specific = 4
FEATURE [App::DocumentObjectGroupPython] O_element045  label="O_element : 0.460"  # scripted group (container) (typed FeaturePython)
  n = 0.4598
FEATURE [App::DocumentObjectGroupPython] Na_element009  label="Na_element : 0.096"  # scripted group (container) (typed FeaturePython)
  n = 0.0964411
FEATURE [App::DocumentObjectGroupPython] Si_element005  label="Si_element : 0.378"  # scripted group (container) (typed FeaturePython)
  n = 0.336553
FEATURE [App::DocumentObjectGroupPython] Ca_element011  label="Ca_element : 0.107"  # scripted group (container) (typed FeaturePython)
  n = 0.107205
FEATURE [App::DocumentObjectGroupPython] G4_GLASS_PLATE  # scripted group (container) (typed FeaturePython)
  Dunit = g/cm3
  Dvalue = 2.4
  Group = -> [O_element045,Na_element009,Si_element005,Ca_element011]
  conduct = 2
  density = 1
  expand = 3
  formula = G4_GLASS_PLATE
  name = G4_GLASS_PLATE
  specific = 4
FEATURE [App::DocumentObjectGroupPython] C_element049  label="C_element : 026"  # scripted group (container) (typed FeaturePython)
  n = 5
  ref = C_element
FEATURE [App::DocumentObjectGroupPython] H_element042  label="H_element : 021"  # scripted group (container) (typed FeaturePython)
  n = 10
  ref = H_element
FEATURE [App::DocumentObjectGroupPython] N_element019  label="N_element : 2"  # scripted group (container) (typed FeaturePython)
  n = 2
  ref = N_element
FEATURE [App::DocumentObjectGroupPython] O_element046  label="O_element : 022"  # scripted group (container) (typed FeaturePython)
  n = 3
  ref = O_element
FEATURE [App::DocumentObjectGroupPython] G4_GLUTAMINE  # scripted group (container) (typed FeaturePython)
  Dunit = g/cm3
  Dvalue = 1.46
  Group = -> [C_element049,H_element042,N_element019,O_element046]
  conduct = 2
  density = 1
  expand = 3
  formula = G4_GLUTAMINE
  name = G4_GLUTAMINE
  specific = 4
FEATURE [App::DocumentObjectGroupPython] C_element050  label="C_element : 027"  # scripted group (container) (typed FeaturePython)
  n = 3
  ref = C_element
FEATURE [App::DocumentObjectGroupPython] H_element043  label="H_element : 022"  # scripted group (container) (typed FeaturePython)
  n = 8
  ref = H_element
FEATURE [App::DocumentObjectGroupPython] O_element047  label="O_element : 023"  # scripted group (container) (typed FeaturePython)
  n = 3
  ref = O_element
FEATURE [App::DocumentObjectGroupPython] G4_GLYCEROL  # scripted group (container) (typed FeaturePython)
  Dunit = g/cm3
  Dvalue = 1.2613
  Group = -> [C_element050,H_element043,O_element047]
  conduct = 2
  density = 1
  expand = 3
  formula = G4_GLYCEROL
  name = G4_GLYCEROL
  specific = 4
FEATURE [App::DocumentObjectGroupPython] C_element051  label="C_element : 028"  # scripted group (container) (typed FeaturePython)
  n = 5
  ref = C_element
FEATURE [App::DocumentObjectGroupPython] H_element044  label="H_element : 023"  # scripted group (container) (typed FeaturePython)
  n = 5
  ref = H_element
FEATURE [App::DocumentObjectGroupPython] N_element020  label="N_element : 009"  # scripted group (container) (typed FeaturePython)
  n = 5
  ref = N_element
FEATURE [App::DocumentObjectGroupPython] O_element048  label="O_element : 024"  # scripted group (container) (typed FeaturePython)
  n = 1
  ref = O_element
FEATURE [App::DocumentObjectGroupPython] G4_GUANINE  # scripted group (container) (typed FeaturePython)
  Dunit = g/cm3
  Dvalue = 2.2
  Group = -> [C_element051,H_element044,N_element020,O_element048]
  conduct = 2
  density = 1
  expand = 3
  formula = G4_GUANINE
  name = G4_GUANINE
  specific = 4
FEATURE [App::DocumentObjectGroupPython] Ca_element012  label="Ca_element : 006"  # scripted group (container) (typed FeaturePython)
  n = 1
  ref = Ca_element
FEATURE [App::DocumentObjectGroupPython] S_element014  label="S_element : 005"  # scripted group (container) (typed FeaturePython)
  n = 1
  ref = S_element
FEATURE [App::DocumentObjectGroupPython] O_element049  label="O_element : 6"  # scripted group (container) (typed FeaturePython)
  n = 6
  ref = O_element
FEATURE [App::DocumentObjectGroupPython] H_element045  label="H_element : 024"  # scripted group (container) (typed FeaturePython)
  n = 4
  ref = H_element
FEATURE [App::DocumentObjectGroupPython] G4_GYPSUM  # scripted group (container) (typed FeaturePython)
  Dunit = g/cm3
  Dvalue = 2.32
  Group = -> [Ca_element012,S_element014,O_element049,H_element045]
  conduct = 2
  density = 1
  expand = 3
  formula = G4_GYPSUM
  name = G4_GYPSUM
  specific = 4
FEATURE [App::DocumentObjectGroupPython] C_element052  label="C_element : 7"  # scripted group (container) (typed FeaturePython)
  n = 7
  ref = C_element
FEATURE [App::DocumentObjectGroupPython] H_element046  label="H_element : 16"  # scripted group (container) (typed FeaturePython)
  n = 16
  ref = H_element
FEATURE [App::DocumentObjectGroupPython] G4_N_HEPTANE  label="G4_N-HEPTANE"  # scripted group (container) (typed FeaturePython)
  Dunit = g/cm3
  Dvalue = 0.68376
  Group = -> [C_element052,H_element046]
  conduct = 2
  density = 1
  expand = 3
  formula = G4_N-HEPTANE
  name = G4_N-HEPTANE
  specific = 4
FEATURE [App::DocumentObjectGroupPython] C_element053  label="C_element : 029"  # scripted group (container) (typed FeaturePython)
  n = 6
  ref = C_element
FEATURE [App::DocumentObjectGroupPython] H_element047  label="H_element : 14"  # scripted group (container) (typed FeaturePython)
  n = 14
  ref = H_element
FEATURE [App::DocumentObjectGroupPython] G4_N_HEXANE  label="G4_N-HEXANE"  # scripted group (container) (typed FeaturePython)
  Dunit = g/cm3
  Dvalue = 0.6603
  Group = -> [C_element053,H_element047]
  conduct = 2
  density = 1
  expand = 3
  formula = G4_N-HEXANE
  name = G4_N-HEXANE
  specific = 4
FEATURE [App::DocumentObjectGroupPython] C_element054  label="C_element : 22"  # scripted group (container) (typed FeaturePython)
  n = 22
  ref = C_element
FEATURE [App::DocumentObjectGroupPython] H_element048  label="H_element : 025"  # scripted group (container) (typed FeaturePython)
  n = 10
  ref = H_element
FEATURE [App::DocumentObjectGroupPython] N_element021  label="N_element : 010"  # scripted group (container) (typed FeaturePython)
  n = 2
  ref = N_element
FEATURE [App::DocumentObjectGroupPython] O_element050  label="O_element : 025"  # scripted group (container) (typed FeaturePython)
  n = 5
  ref = O_element
FEATURE [App::DocumentObjectGroupPython] G4_KAPTON  # scripted group (container) (typed FeaturePython)
  Dunit = g/cm3
  Dvalue = 1.42
  Group = -> [C_element054,H_element048,N_element021,O_element050]
  conduct = 2
  density = 1
  expand = 3
  formula = G4_KAPTON
  name = G4_KAPTON
  specific = 4
FEATURE [App::DocumentObjectGroupPython] La_element001  label="La_element : 1"  # scripted group (container) (typed FeaturePython)
  n = 1
  ref = La_element
FEATURE [App::DocumentObjectGroupPython] Br_element003  label="Br_element : 002"  # scripted group (container) (typed FeaturePython)
  n = 1
  ref = Br_element
FEATURE [App::DocumentObjectGroupPython] O_element051  label="O_element : 026"  # scripted group (container) (typed FeaturePython)
  n = 1
  ref = O_element
FEATURE [App::DocumentObjectGroupPython] G4_LANTHANUM_OXYBROMIDE  # scripted group (container) (typed FeaturePython)
  Dunit = g/cm3
  Dvalue = 6.28
  Group = -> [La_element001,Br_element003,O_element051]
  conduct = 2
  density = 1
  expand = 3
  formula = G4_LANTHANUM_OXYBROMIDE
  name = G4_LANTHANUM_OXYBROMIDE
  specific = 4
FEATURE [App::DocumentObjectGroupPython] La_element002  label="La_element : 2"  # scripted group (container) (typed FeaturePython)
  n = 2
  ref = La_element
FEATURE [App::DocumentObjectGroupPython] O_element052  label="O_element : 027"  # scripted group (container) (typed FeaturePython)
  n = 2
  ref = O_element
FEATURE [App::DocumentObjectGroupPython] S_element015  label="S_element : 006"  # scripted group (container) (typed FeaturePython)
  n = 1
  ref = S_element
FEATURE [App::DocumentObjectGroupPython] G4_LANTHANUM_OXYSULFIDE  # scripted group (container) (typed FeaturePython)
  Dunit = g/cm3
  Dvalue = 5.86
  Group = -> [La_element002,O_element052,S_element015]
  conduct = 2
  density = 1
  expand = 3
  formula = G4_LANTHANUM_OXYSULFIDE
  name = G4_LANTHANUM_OXYSULFIDE
  specific = 4
FEATURE [App::DocumentObjectGroupPython] O_element053  label="O_element : 0.072"  # scripted group (container) (typed FeaturePython)
  n = 0.071682
FEATURE [App::DocumentObjectGroupPython] Pb_element002  label="Pb_element : 0.928"  # scripted group (container) (typed FeaturePython)
  n = 0.928318
FEATURE [App::DocumentObjectGroupPython] G4_LEAD_OXIDE  # scripted group (container) (typed FeaturePython)
  Dunit = g/cm3
  Dvalue = 9.53
  Group = -> [O_element053,Pb_element002]
  conduct = 2
  density = 1
  expand = 3
  formula = G4_LEAD_OXIDE
  name = G4_LEAD_OXIDE
  specific = 4
FEATURE [App::DocumentObjectGroupPython] Li_element001  label="Li_element : 1"  # scripted group (container) (typed FeaturePython)
  n = 1
  ref = Li_element
FEATURE [App::DocumentObjectGroupPython] N_element022  label="N_element : 011"  # scripted group (container) (typed FeaturePython)
  n = 1
  ref = N_element
FEATURE [App::DocumentObjectGroupPython] H_element049  label="H_element : 026"  # scripted group (container) (typed FeaturePython)
  n = 2
  ref = H_element
FEATURE [App::DocumentObjectGroupPython] G4_LITHIUM_AMIDE  # scripted group (container) (typed FeaturePython)
  Dunit = g/cm3
  Dvalue = 1.178
  Group = -> [Li_element001,N_element022,H_element049]
  conduct = 2
  density = 1
  expand = 3
  formula = G4_LITHIUM_AMIDE
  name = G4_LITHIUM_AMIDE
  specific = 4
FEATURE [App::DocumentObjectGroupPython] Li_element002  label="Li_element : 2"  # scripted group (container) (typed FeaturePython)
  n = 2
  ref = Li_element
FEATURE [App::DocumentObjectGroupPython] C_element055  label="C_element : 030"  # scripted group (container) (typed FeaturePython)
  n = 1
  ref = C_element
FEATURE [App::DocumentObjectGroupPython] O_element054  label="O_element : 028"  # scripted group (container) (typed FeaturePython)
  n = 3
  ref = O_element
FEATURE [App::DocumentObjectGroupPython] G4_LITHIUM_CARBONATE  # scripted group (container) (typed FeaturePython)
  Dunit = g/cm3
  Dvalue = 2.11
  Group = -> [Li_element002,C_element055,O_element054]
  conduct = 2
  density = 1
  expand = 3
  formula = G4_LITHIUM_CARBONATE
  name = G4_LITHIUM_CARBONATE
  specific = 4
FEATURE [App::DocumentObjectGroupPython] Li_element003  label="Li_element : 003"  # scripted group (container) (typed FeaturePython)
  n = 1
  ref = Li_element
FEATURE [App::DocumentObjectGroupPython] F_element012  label="F_element : 004"  # scripted group (container) (typed FeaturePython)
  n = 1
  ref = F_element
FEATURE [App::DocumentObjectGroupPython] G4_LITHIUM_FLUORIDE  # scripted group (container) (typed FeaturePython)
  Dunit = g/cm3
  Dvalue = 2.635
  Group = -> [Li_element003,F_element012]
  conduct = 2
  density = 1
  expand = 3
  formula = G4_LITHIUM_FLUORIDE
  name = G4_LITHIUM_FLUORIDE
  specific = 4
FEATURE [App::DocumentObjectGroupPython] Li_element004  label="Li_element : 004"  # scripted group (container) (typed FeaturePython)
  n = 1
  ref = Li_element
FEATURE [App::DocumentObjectGroupPython] H_element050  label="H_element : 027"  # scripted group (container) (typed FeaturePython)
  n = 1
  ref = H_element
FEATURE [App::DocumentObjectGroupPython] G4_LITHIUM_HYDRIDE  # scripted group (container) (typed FeaturePython)
  Dunit = g/cm3
  Dvalue = 0.82
  Group = -> [Li_element004,H_element050]
  conduct = 2
  density = 1
  expand = 3
  formula = G4_LITHIUM_HYDRIDE
  name = G4_LITHIUM_HYDRIDE
  specific = 4
FEATURE [App::DocumentObjectGroupPython] Li_element005  label="Li_element : 005"  # scripted group (container) (typed FeaturePython)
  n = 1
  ref = Li_element
FEATURE [App::DocumentObjectGroupPython] I_element003  label="I_element : 002"  # scripted group (container) (typed FeaturePython)
  n = 1
  ref = I_element
FEATURE [App::DocumentObjectGroupPython] G4_LITHIUM_IODIDE  # scripted group (container) (typed FeaturePython)
  Dunit = g/cm3
  Dvalue = 3.494
  Group = -> [Li_element005,I_element003]
  conduct = 2
  density = 1
  expand = 3
  formula = G4_LITHIUM_IODIDE
  name = G4_LITHIUM_IODIDE
  specific = 4
FEATURE [App::DocumentObjectGroupPython] Li_element006  label="Li_element : 006"  # scripted group (container) (typed FeaturePython)
  n = 2
  ref = Li_element
FEATURE [App::DocumentObjectGroupPython] O_element055  label="O_element : 029"  # scripted group (container) (typed FeaturePython)
  n = 1
  ref = O_element
FEATURE [App::DocumentObjectGroupPython] G4_LITHIUM_OXIDE  # scripted group (container) (typed FeaturePython)
  Dunit = g/cm3
  Dvalue = 2.013
  Group = -> [Li_element006,O_element055]
  conduct = 2
  density = 1
  expand = 3
  formula = G4_LITHIUM_OXIDE
  name = G4_LITHIUM_OXIDE
  specific = 4
FEATURE [App::DocumentObjectGroupPython] Li_element007  label="Li_element : 007"  # scripted group (container) (typed FeaturePython)
  n = 2
  ref = Li_element
FEATURE [App::DocumentObjectGroupPython] B_element005  label="B_element : 005"  # scripted group (container) (typed FeaturePython)
  n = 4
  ref = B_element
FEATURE [App::DocumentObjectGroupPython] O_element056  label="O_element : 7"  # scripted group (container) (typed FeaturePython)
  n = 7
  ref = O_element
FEATURE [App::DocumentObjectGroupPython] G4_LITHIUM_TETRABORATE  # scripted group (container) (typed FeaturePython)
  Dunit = g/cm3
  Dvalue = 2.44
  Group = -> [Li_element007,B_element005,O_element056]
  conduct = 2
  density = 1
  expand = 3
  formula = G4_LITHIUM_TETRABORATE
  name = G4_LITHIUM_TETRABORATE
  specific = 4
FEATURE [App::DocumentObjectGroupPython] H_element051  label="H_element : 0.105"  # scripted group (container) (typed FeaturePython)
  n = 0.105
FEATURE [App::DocumentObjectGroupPython] C_element056  label="C_element : 0.083"  # scripted group (container) (typed FeaturePython)
  n = 0.083
FEATURE [App::DocumentObjectGroupPython] N_element023  label="N_element : 0.023"  # scripted group (container) (typed FeaturePython)
  n = 0.023
FEATURE [App::DocumentObjectGroupPython] O_element057  label="O_element : 0.779"  # scripted group (container) (typed FeaturePython)
  n = 0.779
FEATURE [App::DocumentObjectGroupPython] Na_element010  label="Na_element : 0.097"  # scripted group (container) (typed FeaturePython)
  n = 0.002
FEATURE [App::DocumentObjectGroupPython] P_element006  label="P_element : 0.105"  # scripted group (container) (typed FeaturePython)
  n = 0.001
FEATURE [App::DocumentObjectGroupPython] S_element016  label="S_element : 0.017"  # scripted group (container) (typed FeaturePython)
  n = 0.002
FEATURE [App::DocumentObjectGroupPython] Cl_element014  label="Cl_element : 0.587"  # scripted group (container) (typed FeaturePython)
  n = 0.003
FEATURE [App::DocumentObjectGroupPython] K_element005  label="K_element : 0.015"  # scripted group (container) (typed FeaturePython)
  n = 0.002
FEATURE [App::DocumentObjectGroupPython] G4_LUNG_ICRP  # scripted group (container) (typed FeaturePython)
  Dunit = g/cm3
  Dvalue = 1.04
  Group = -> [H_element051,C_element056,N_element023,O_element057,Na_element010,P_element006,S_element016,Cl_element014,K_element005]
  conduct = 2
  density = 1
  expand = 3
  formula = G4_LUNG_ICRP
  name = G4_LUNG_ICRP
  specific = 4
FEATURE [App::DocumentObjectGroupPython] H_element052  label="H_element : 0.116"  # scripted group (container) (typed FeaturePython)
  n = 0.114318
FEATURE [App::DocumentObjectGroupPython] C_element057  label="C_element : 0.656"  # scripted group (container) (typed FeaturePython)
  n = 0.655824
FEATURE [App::DocumentObjectGroupPython] O_element058  label="O_element : 0.092"  # scripted group (container) (typed FeaturePython)
  n = 0.0921831
FEATURE [App::DocumentObjectGroupPython] Mg_element004  label="Mg_element : 0.135"  # scripted group (container) (typed FeaturePython)
  n = 0.134792
FEATURE [App::DocumentObjectGroupPython] Ca_element013  label="Ca_element : 0.003"  # scripted group (container) (typed FeaturePython)
  n = 0.002883
FEATURE [App::DocumentObjectGroupPython] G4_M3_WAX  # scripted group (container) (typed FeaturePython)
  Dunit = g/cm3
  Dvalue = 1.05
  Group = -> [H_element052,C_element057,O_element058,Mg_element004,Ca_element013]
  conduct = 2
  density = 1
  expand = 3
  formula = G4_M3_WAX
  name = G4_M3_WAX
  specific = 4
FEATURE [App::DocumentObjectGroupPython] Mg_element005  label="Mg_element : 1"  # scripted group (container) (typed FeaturePython)
  n = 1
  ref = Mg_element
FEATURE [App::DocumentObjectGroupPython] C_element058  label="C_element : 031"  # scripted group (container) (typed FeaturePython)
  n = 1
  ref = C_element
FEATURE [App::DocumentObjectGroupPython] O_element059  label="O_element : 030"  # scripted group (container) (typed FeaturePython)
  n = 3
  ref = O_element
FEATURE [App::DocumentObjectGroupPython] G4_MAGNESIUM_CARBONATE  # scripted group (container) (typed FeaturePython)
  Dunit = g/cm3
  Dvalue = 2.958
  Group = -> [Mg_element005,C_element058,O_element059]
  conduct = 2
  density = 1
  expand = 3
  formula = G4_MAGNESIUM_CARBONATE
  name = G4_MAGNESIUM_CARBONATE
  specific = 4
FEATURE [App::DocumentObjectGroupPython] Mg_element006  label="Mg_element : 002"  # scripted group (container) (typed FeaturePython)
  n = 1
  ref = Mg_element
FEATURE [App::DocumentObjectGroupPython] F_element013  label="F_element : 005"  # scripted group (container) (typed FeaturePython)
  n = 2
  ref = F_element
FEATURE [App::DocumentObjectGroupPython] G4_MAGNESIUM_FLUORIDE  # scripted group (container) (typed FeaturePython)
  Dunit = g/cm3
  Dvalue = 3
  Group = -> [Mg_element006,F_element013]
  conduct = 2
  density = 1
  expand = 3
  formula = G4_MAGNESIUM_FLUORIDE
  name = G4_MAGNESIUM_FLUORIDE
  specific = 4
FEATURE [App::DocumentObjectGroupPython] Mg_element007  label="Mg_element : 003"  # scripted group (container) (typed FeaturePython)
  n = 1
  ref = Mg_element
FEATURE [App::DocumentObjectGroupPython] O_element060  label="O_element : 031"  # scripted group (container) (typed FeaturePython)
  n = 1
  ref = O_element
FEATURE [App::DocumentObjectGroupPython] G4_MAGNESIUM_OXIDE  # scripted group (container) (typed FeaturePython)
  Dunit = g/cm3
  Dvalue = 3.58
  Group = -> [Mg_element007,O_element060]
  conduct = 2
  density = 1
  expand = 3
  formula = G4_MAGNESIUM_OXIDE
  name = G4_MAGNESIUM_OXIDE
  specific = 4
FEATURE [App::DocumentObjectGroupPython] Mg_element008  label="Mg_element : 004"  # scripted group (container) (typed FeaturePython)
  n = 1
  ref = Mg_element
FEATURE [App::DocumentObjectGroupPython] B_element006  label="B_element : 006"  # scripted group (container) (typed FeaturePython)
  n = 4
  ref = B_element
FEATURE [App::DocumentObjectGroupPython] O_element061  label="O_element : 032"  # scripted group (container) (typed FeaturePython)
  n = 7
  ref = O_element
FEATURE [App::DocumentObjectGroupPython] G4_MAGNESIUM_TETRABORATE  # scripted group (container) (typed FeaturePython)
  Dunit = g/cm3
  Dvalue = 2.53
  Group = -> [Mg_element008,B_element006,O_element061]
  conduct = 2
  density = 1
  expand = 3
  formula = G4_MAGNESIUM_TETRABORATE
  name = G4_MAGNESIUM_TETRABORATE
  specific = 4
FEATURE [App::DocumentObjectGroupPython] Hg_element001  label="Hg_element : 1"  # scripted group (container) (typed FeaturePython)
  n = 1
  ref = Hg_element
FEATURE [App::DocumentObjectGroupPython] I_element004  label="I_element : 2"  # scripted group (container) (typed FeaturePython)
  n = 2
  ref = I_element
FEATURE [App::DocumentObjectGroupPython] G4_MERCURIC_IODIDE  # scripted group (container) (typed FeaturePython)
  Dunit = g/cm3
  Dvalue = 6.36
  Group = -> [Hg_element001,I_element004]
  conduct = 2
  density = 1
  expand = 3
  formula = G4_MERCURIC_IODIDE
  name = G4_MERCURIC_IODIDE
  specific = 4
FEATURE [App::DocumentObjectGroupPython] C_element059  label="C_element : 032"  # scripted group (container) (typed FeaturePython)
  n = 1
  ref = C_element
FEATURE [App::DocumentObjectGroupPython] H_element053  label="H_element : 028"  # scripted group (container) (typed FeaturePython)
  n = 4
  ref = H_element
FEATURE [App::DocumentObjectGroupPython] G4_METHANE  # scripted group (container) (typed FeaturePython)
  Dunit = g/cm3
  Dvalue = 0.000667151
  Group = -> [C_element059,H_element053]
  conduct = 2
  density = 1
  expand = 3
  formula = G4_METHANE
  name = G4_METHANE
  specific = 4
FEATURE [App::DocumentObjectGroupPython] C_element060  label="C_element : 033"  # scripted group (container) (typed FeaturePython)
  n = 1
  ref = C_element
FEATURE [App::DocumentObjectGroupPython] H_element054  label="H_element : 029"  # scripted group (container) (typed FeaturePython)
  n = 4
  ref = H_element
FEATURE [App::DocumentObjectGroupPython] O_element062  label="O_element : 033"  # scripted group (container) (typed FeaturePython)
  n = 1
  ref = O_element
FEATURE [App::DocumentObjectGroupPython] G4_METHANOL  # scripted group (container) (typed FeaturePython)
  Dunit = g/cm3
  Dvalue = 0.7914
  Group = -> [C_element060,H_element054,O_element062]
  conduct = 2
  density = 1
  expand = 3
  formula = G4_METHANOL
  name = G4_METHANOL
  specific = 4
FEATURE [App::DocumentObjectGroupPython] H_element055  label="H_element : 0.134"  # scripted group (container) (typed FeaturePython)
  n = 0.13404
FEATURE [App::DocumentObjectGroupPython] C_element061  label="C_element : 0.778"  # scripted group (container) (typed FeaturePython)
  n = 0.77796
FEATURE [App::DocumentObjectGroupPython] O_element063  label="O_element : 0.035"  # scripted group (container) (typed FeaturePython)
  n = 0.03502
FEATURE [App::DocumentObjectGroupPython] Mg_element009  label="Mg_element : 0.039"  # scripted group (container) (typed FeaturePython)
  n = 0.038594
FEATURE [App::DocumentObjectGroupPython] Ti_element002  label="Ti_element : 0.014"  # scripted group (container) (typed FeaturePython)
  n = 0.014386
FEATURE [App::DocumentObjectGroupPython] G4_MIX_D_WAX  # scripted group (container) (typed FeaturePython)
  Dunit = g/cm3
  Dvalue = 0.99
  Group = -> [H_element055,C_element061,O_element063,Mg_element009,Ti_element002]
  conduct = 2
  density = 1
  expand = 3
  formula = G4_MIX_D_WAX
  name = G4_MIX_D_WAX
  specific = 4
FEATURE [App::DocumentObjectGroupPython] H_element056  label="H_element : 0.135"  # scripted group (container) (typed FeaturePython)
  n = 0.081192
FEATURE [App::DocumentObjectGroupPython] C_element062  label="C_element : 0.583"  # scripted group (container) (typed FeaturePython)
  n = 0.583442
FEATURE [App::DocumentObjectGroupPython] N_element024  label="N_element : 0.018"  # scripted group (container) (typed FeaturePython)
  n = 0.017798
FEATURE [App::DocumentObjectGroupPython] O_element064  label="O_element : 0.186"  # scripted group (container) (typed FeaturePython)
  n = 0.186381
FEATURE [App::DocumentObjectGroupPython] Mg_element010  label="Mg_element : 0.130"  # scripted group (container) (typed FeaturePython)
  n = 0.130287
FEATURE [App::DocumentObjectGroupPython] Cl_element015  label="Cl_element : 0.588"  # scripted group (container) (typed FeaturePython)
  n = 0.0009
FEATURE [App::DocumentObjectGroupPython] G4_MS20_TISSUE  # scripted group (container) (typed FeaturePython)
  Dunit = g/cm3
  Dvalue = 1
  Group = -> [H_element056,C_element062,N_element024,O_element064,Mg_element010,Cl_element015]
  conduct = 2
  density = 1
  expand = 3
  formula = G4_MS20_TISSUE
  name = G4_MS20_TISSUE
  specific = 4
FEATURE [App::DocumentObjectGroupPython] H_element057  label="H_element : 0.136"  # scripted group (container) (typed FeaturePython)
  n = 0.102
FEATURE [App::DocumentObjectGroupPython] C_element063  label="C_element : 0.143"  # scripted group (container) (typed FeaturePython)
  n = 0.143
FEATURE [App::DocumentObjectGroupPython] N_element025  label="N_element : 0.034"  # scripted group (container) (typed FeaturePython)
  n = 0.034
FEATURE [App::DocumentObjectGroupPython] O_element065  label="O_element : 0.710"  # scripted group (container) (typed FeaturePython)
  n = 0.71
FEATURE [App::DocumentObjectGroupPython] Na_element011  label="Na_element : 0.098"  # scripted group (container) (typed FeaturePython)
  n = 0.001
FEATURE [App::DocumentObjectGroupPython] P_element007  label="P_element : 0.002"  # scripted group (container) (typed FeaturePython)
  n = 0.002
FEATURE [App::DocumentObjectGroupPython] S_element017  label="S_element : 0.018"  # scripted group (container) (typed FeaturePython)
  n = 0.003
FEATURE [App::DocumentObjectGroupPython] Cl_element016  label="Cl_element : 0.589"  # scripted group (container) (typed FeaturePython)
  n = 0.001
FEATURE [App::DocumentObjectGroupPython] K_element006  label="K_element : 0.004"  # scripted group (container) (typed FeaturePython)
  n = 0.004
FEATURE [App::DocumentObjectGroupPython] G4_MUSCLE_SKELETAL_ICRP  # scripted group (container) (typed FeaturePython)
  Dunit = g/cm3
  Dvalue = 1.05
  Group = -> [H_element057,C_element063,N_element025,O_element065,Na_element011,P_element007,S_element017,Cl_element016,K_element006]
  conduct = 2
  density = 1
  expand = 3
  formula = G4_MUSCLE_SKELETAL_ICRP
  name = G4_MUSCLE_SKELETAL_ICRP
  specific = 4
FEATURE [App::DocumentObjectGroupPython] H_element058  label="H_element : 0.137"  # scripted group (container) (typed FeaturePython)
  n = 0.102102
FEATURE [App::DocumentObjectGroupPython] C_element064  label="C_element : 0.123"  # scripted group (container) (typed FeaturePython)
  n = 0.123123
FEATURE [App::DocumentObjectGroupPython] N_element026  label="N_element : 0.756"  # scripted group (container) (typed FeaturePython)
  n = 0.035035
FEATURE [App::DocumentObjectGroupPython] O_element066  label="O_element : 0.730"  # scripted group (container) (typed FeaturePython)
  n = 0.72973
FEATURE [App::DocumentObjectGroupPython] Na_element012  label="Na_element : 0.099"  # scripted group (container) (typed FeaturePython)
  n = 0.001001
FEATURE [App::DocumentObjectGroupPython] P_element008  label="P_element : 0.106"  # scripted group (container) (typed FeaturePython)
  n = 0.002002
FEATURE [App::DocumentObjectGroupPython] S_element018  label="S_element : 0.019"  # scripted group (container) (typed FeaturePython)
  n = 0.004004
FEATURE [App::DocumentObjectGroupPython] K_element007  label="K_element : 0.016"  # scripted group (container) (typed FeaturePython)
  n = 0.003003
FEATURE [App::DocumentObjectGroupPython] G4_MUSCLE_STRIATED_ICRU  # scripted group (container) (typed FeaturePython)
  Dunit = g/cm3
  Dvalue = 1.04
  Group = -> [H_element058,C_element064,N_element026,O_element066,Na_element012,P_element008,S_element018,K_element007]
  conduct = 2
  density = 1
  expand = 3
  formula = G4_MUSCLE_STRIATED_ICRU
  name = G4_MUSCLE_STRIATED_ICRU
  specific = 4
FEATURE [App::DocumentObjectGroupPython] H_element059  label="H_element : 0.098"  # scripted group (container) (typed FeaturePython)
  n = 0.0982341
FEATURE [App::DocumentObjectGroupPython] C_element065  label="C_element : 0.156"  # scripted group (container) (typed FeaturePython)
  n = 0.156214
FEATURE [App::DocumentObjectGroupPython] N_element027  label="N_element : 0.757"  # scripted group (container) (typed FeaturePython)
  n = 0.035451
FEATURE [App::DocumentObjectGroupPython] O_element067  label="O_element : 0.880"  # scripted group (container) (typed FeaturePython)
  n = 0.710101
FEATURE [App::DocumentObjectGroupPython] G4_MUSCLE_WITH_SUCROSE  # scripted group (container) (typed FeaturePython)
  Dunit = g/cm3
  Dvalue = 1.11
  Group = -> [H_element059,C_element065,N_element027,O_element067]
  conduct = 2
  density = 1
  expand = 3
  formula = G4_MUSCLE_WITH_SUCROSE
  name = G4_MUSCLE_WITH_SUCROSE
  specific = 4
FEATURE [App::DocumentObjectGroupPython] H_element060  label="H_element : 0.138"  # scripted group (container) (typed FeaturePython)
  n = 0.101969
FEATURE [App::DocumentObjectGroupPython] C_element066  label="C_element : 0.120"  # scripted group (container) (typed FeaturePython)
  n = 0.120058
FEATURE [App::DocumentObjectGroupPython] N_element028  label="N_element : 0.758"  # scripted group (container) (typed FeaturePython)
  n = 0.035451
FEATURE [App::DocumentObjectGroupPython] O_element068  label="O_element : 0.743"  # scripted group (container) (typed FeaturePython)
  n = 0.742522
FEATURE [App::DocumentObjectGroupPython] G4_MUSCLE_WITHOUT_SUCROSE  # scripted group (container) (typed FeaturePython)
  Dunit = g/cm3
  Dvalue = 1.07
  Group = -> [H_element060,C_element066,N_element028,O_element068]
  conduct = 2
  density = 1
  expand = 3
  formula = G4_MUSCLE_WITHOUT_SUCROSE
  name = G4_MUSCLE_WITHOUT_SUCROSE
  specific = 4
FEATURE [App::DocumentObjectGroupPython] C_element067  label="C_element : 10"  # scripted group (container) (typed FeaturePython)
  n = 10
  ref = C_element
FEATURE [App::DocumentObjectGroupPython] H_element061  label="H_element : 030"  # scripted group (container) (typed FeaturePython)
  n = 8
  ref = H_element
FEATURE [App::DocumentObjectGroupPython] G4_NAPHTHALENE  # scripted group (container) (typed FeaturePython)
  Dunit = g/cm3
  Dvalue = 1.145
  Group = -> [C_element067,H_element061]
  conduct = 2
  density = 1
  expand = 3
  formula = G4_NAPHTHALENE
  name = G4_NAPHTHALENE
  specific = 4
FEATURE [App::DocumentObjectGroupPython] C_element068  label="C_element : 034"  # scripted group (container) (typed FeaturePython)
  n = 6
  ref = C_element
FEATURE [App::DocumentObjectGroupPython] H_element062  label="H_element : 031"  # scripted group (container) (typed FeaturePython)
  n = 5
  ref = H_element
FEATURE [App::DocumentObjectGroupPython] N_element029  label="N_element : 012"  # scripted group (container) (typed FeaturePython)
  n = 1
  ref = N_element
FEATURE [App::DocumentObjectGroupPython] O_element069  label="O_element : 034"  # scripted group (container) (typed FeaturePython)
  n = 2
  ref = O_element
FEATURE [App::DocumentObjectGroupPython] G4_NITROBENZENE  # scripted group (container) (typed FeaturePython)
  Dunit = g/cm3
  Dvalue = 1.19867
  Group = -> [C_element068,H_element062,N_element029,O_element069]
  conduct = 2
  density = 1
  expand = 3
  formula = G4_NITROBENZENE
  name = G4_NITROBENZENE
  specific = 4
FEATURE [App::DocumentObjectGroupPython] N_element030  label="N_element : 013"  # scripted group (container) (typed FeaturePython)
  n = 2
  ref = N_element
FEATURE [App::DocumentObjectGroupPython] O_element070  label="O_element : 035"  # scripted group (container) (typed FeaturePython)
  n = 1
  ref = O_element
FEATURE [App::DocumentObjectGroupPython] G4_NITROUS_OXIDE  # scripted group (container) (typed FeaturePython)
  Dunit = g/cm3
  Dvalue = 0.00183094
  Group = -> [N_element030,O_element070]
  conduct = 2
  density = 1
  expand = 3
  formula = G4_NITROUS_OXIDE
  name = G4_NITROUS_OXIDE
  specific = 4
FEATURE [App::DocumentObjectGroupPython] H_element063  label="H_element : 0.104"  # scripted group (container) (typed FeaturePython)
  n = 0.103509
FEATURE [App::DocumentObjectGroupPython] C_element069  label="C_element : 0.648"  # scripted group (container) (typed FeaturePython)
  n = 0.648416
FEATURE [App::DocumentObjectGroupPython] N_element031  label="N_element : 0.100"  # scripted group (container) (typed FeaturePython)
  n = 0.0995361
FEATURE [App::DocumentObjectGroupPython] O_element071  label="O_element : 0.149"  # scripted group (container) (typed FeaturePython)
  n = 0.148539
FEATURE [App::DocumentObjectGroupPython] G4_NYLON_8062  label="G4_NYLON-8062"  # scripted group (container) (typed FeaturePython)
  Dunit = g/cm3
  Dvalue = 1.08
  Group = -> [H_element063,C_element069,N_element031,O_element071]
  conduct = 2
  density = 1
  expand = 3
  formula = G4_NYLON-8062
  name = G4_NYLON-8062
  specific = 4
FEATURE [App::DocumentObjectGroupPython] C_element070  label="C_element : 035"  # scripted group (container) (typed FeaturePython)
  n = 6
  ref = C_element
FEATURE [App::DocumentObjectGroupPython] H_element064  label="H_element : 11"  # scripted group (container) (typed FeaturePython)
  n = 11
  ref = H_element
FEATURE [App::DocumentObjectGroupPython] N_element032  label="N_element : 014"  # scripted group (container) (typed FeaturePython)
  n = 1
  ref = N_element
FEATURE [App::DocumentObjectGroupPython] O_element072  label="O_element : 036"  # scripted group (container) (typed FeaturePython)
  n = 1
  ref = O_element
FEATURE [App::DocumentObjectGroupPython] G4_NYLON_6_6  label="G4_NYLON-6-6"  # scripted group (container) (typed FeaturePython)
  Dunit = g/cm3
  Dvalue = 1.14
  Group = -> [C_element070,H_element064,N_element032,O_element072]
  conduct = 2
  density = 1
  expand = 3
  formula = G4_NYLON-6-6
  name = G4_NYLON-6-6
  specific = 4
FEATURE [App::DocumentObjectGroupPython] H_element065  label="H_element : 0.139"  # scripted group (container) (typed FeaturePython)
  n = 0.107062
FEATURE [App::DocumentObjectGroupPython] C_element071  label="C_element : 0.680"  # scripted group (container) (typed FeaturePython)
  n = 0.680449
FEATURE [App::DocumentObjectGroupPython] N_element033  label="N_element : 0.099"  # scripted group (container) (typed FeaturePython)
  n = 0.099189
FEATURE [App::DocumentObjectGroupPython] O_element073  label="O_element : 0.113"  # scripted group (container) (typed FeaturePython)
  n = 0.1133
FEATURE [App::DocumentObjectGroupPython] G4_NYLON_6_10  label="G4_NYLON-6-10"  # scripted group (container) (typed FeaturePython)
  Dunit = g/cm3
  Dvalue = 1.14
  Group = -> [H_element065,C_element071,N_element033,O_element073]
  conduct = 2
  density = 1
  expand = 3
  formula = G4_NYLON-6-10
  name = G4_NYLON-6-10
  specific = 4
FEATURE [App::DocumentObjectGroupPython] H_element066  label="H_element : 0.140"  # scripted group (container) (typed FeaturePython)
  n = 0.115476
FEATURE [App::DocumentObjectGroupPython] C_element072  label="C_element : 0.721"  # scripted group (container) (typed FeaturePython)
  n = 0.720818
FEATURE [App::DocumentObjectGroupPython] N_element034  label="N_element : 0.076"  # scripted group (container) (typed FeaturePython)
  n = 0.0764169
FEATURE [App::DocumentObjectGroupPython] O_element074  label="O_element : 0.087"  # scripted group (container) (typed FeaturePython)
  n = 0.0872889
FEATURE [App::DocumentObjectGroupPython] G4_NYLON_11_RILSAN  label="G4_NYLON-11_RILSAN"  # scripted group (container) (typed FeaturePython)
  Dunit = g/cm3
  Dvalue = 1.425
  Group = -> [H_element066,C_element072,N_element034,O_element074]
  conduct = 2
  density = 1
  expand = 3
  formula = G4_NYLON-11_RILSAN
  name = G4_NYLON-11_RILSAN
  specific = 4
FEATURE [App::DocumentObjectGroupPython] C_element073  label="C_element : 8"  # scripted group (container) (typed FeaturePython)
  n = 8
  ref = C_element
FEATURE [App::DocumentObjectGroupPython] H_element067  label="H_element : 18"  # scripted group (container) (typed FeaturePython)
  n = 18
  ref = H_element
FEATURE [App::DocumentObjectGroupPython] G4_OCTANE  # scripted group (container) (typed FeaturePython)
  Dunit = g/cm3
  Dvalue = 0.7026
  Group = -> [C_element073,H_element067]
  conduct = 2
  density = 1
  expand = 3
  formula = G4_OCTANE
  name = G4_OCTANE
  specific = 4
FEATURE [App::DocumentObjectGroupPython] C_element074  label="C_element : 25"  # scripted group (container) (typed FeaturePython)
  n = 25
  ref = C_element
FEATURE [App::DocumentObjectGroupPython] H_element068  label="H_element : 52"  # scripted group (container) (typed FeaturePython)
  n = 52
  ref = H_element
FEATURE [App::DocumentObjectGroupPython] G4_PARAFFIN  # scripted group (container) (typed FeaturePython)
  Dunit = g/cm3
  Dvalue = 0.93
  Group = -> [C_element074,H_element068]
  conduct = 2
  density = 1
  expand = 3
  formula = G4_PARAFFIN
  name = G4_PARAFFIN
  specific = 4
FEATURE [App::DocumentObjectGroupPython] C_element075  label="C_element : 036"  # scripted group (container) (typed FeaturePython)
  n = 5
  ref = C_element
FEATURE [App::DocumentObjectGroupPython] H_element069  label="H_element : 032"  # scripted group (container) (typed FeaturePython)
  n = 12
  ref = H_element
FEATURE [App::DocumentObjectGroupPython] G4_N_PENTANE  label="G4_N-PENTANE"  # scripted group (container) (typed FeaturePython)
  Dunit = g/cm3
  Dvalue = 0.6262
  Group = -> [C_element075,H_element069]
  conduct = 2
  density = 1
  expand = 3
  formula = G4_N-PENTANE
  name = G4_N-PENTANE
  specific = 4
FEATURE [App::DocumentObjectGroupPython] H_element070  label="H_element : 0.014"  # scripted group (container) (typed FeaturePython)
  n = 0.0141
FEATURE [App::DocumentObjectGroupPython] C_element076  label="C_element : 0.072"  # scripted group (container) (typed FeaturePython)
  n = 0.072261
FEATURE [App::DocumentObjectGroupPython] N_element035  label="N_element : 0.019"  # scripted group (container) (typed FeaturePython)
  n = 0.01932
FEATURE [App::DocumentObjectGroupPython] O_element075  label="O_element : 0.066"  # scripted group (container) (typed FeaturePython)
  n = 0.066101
FEATURE [App::DocumentObjectGroupPython] S_element019  label="S_element : 0.020"  # scripted group (container) (typed FeaturePython)
  n = 0.00189
FEATURE [App::DocumentObjectGroupPython] Br_element004  label="Br_element : 0.349"  # scripted group (container) (typed FeaturePython)
  n = 0.349103
FEATURE [App::DocumentObjectGroupPython] Ag_element001  label="Ag_element : 0.474"  # scripted group (container) (typed FeaturePython)
  n = 0.474105
FEATURE [App::DocumentObjectGroupPython] I_element005  label="I_element : 0.003"  # scripted group (container) (typed FeaturePython)
  n = 0.00312
FEATURE [App::DocumentObjectGroupPython] G4_PHOTO_EMULSION  # scripted group (container) (typed FeaturePython)
  Dunit = g/cm3
  Dvalue = 3.815
  Group = -> [H_element070,C_element076,N_element035,O_element075,S_element019,Br_element004,Ag_element001,I_element005]
  conduct = 2
  density = 1
  expand = 3
  formula = G4_PHOTO_EMULSION
  name = G4_PHOTO_EMULSION
  specific = 4
FEATURE [App::DocumentObjectGroupPython] C_element077  label="C_element : 9"  # scripted group (container) (typed FeaturePython)
  n = 9
  ref = C_element
FEATURE [App::DocumentObjectGroupPython] H_element071  label="H_element : 033"  # scripted group (container) (typed FeaturePython)
  n = 10
  ref = H_element
FEATURE [App::DocumentObjectGroupPython] G4_PLASTIC_SC_VINYLTOLUENE  # scripted group (container) (typed FeaturePython)
  Dunit = g/cm3
  Dvalue = 1.032
  Group = -> [C_element077,H_element071]
  conduct = 2
  density = 1
  expand = 3
  formula = G4_PLASTIC_SC_VINYLTOLUENE
  name = G4_PLASTIC_SC_VINYLTOLUENE
  specific = 4
FEATURE [App::DocumentObjectGroupPython] Pu_element001  label="Pu_element : 1"  # scripted group (container) (typed FeaturePython)
  n = 1
  ref = Pu_element
FEATURE [App::DocumentObjectGroupPython] O_element076  label="O_element : 037"  # scripted group (container) (typed FeaturePython)
  n = 2
  ref = O_element
FEATURE [App::DocumentObjectGroupPython] G4_PLUTONIUM_DIOXIDE  # scripted group (container) (typed FeaturePython)
  Dunit = g/cm3
  Dvalue = 11.46
  Group = -> [Pu_element001,O_element076]
  conduct = 2
  density = 1
  expand = 3
  formula = G4_PLUTONIUM_DIOXIDE
  name = G4_PLUTONIUM_DIOXIDE
  specific = 4
FEATURE [App::DocumentObjectGroupPython] C_element078  label="C_element : 037"  # scripted group (container) (typed FeaturePython)
  n = 3
  ref = C_element
FEATURE [App::DocumentObjectGroupPython] H_element072  label="H_element : 034"  # scripted group (container) (typed FeaturePython)
  n = 3
  ref = H_element
FEATURE [App::DocumentObjectGroupPython] N_element036  label="N_element : 015"  # scripted group (container) (typed FeaturePython)
  n = 1
  ref = N_element
FEATURE [App::DocumentObjectGroupPython] G4_POLYACRYLONITRILE  # scripted group (container) (typed FeaturePython)
  Dunit = g/cm3
  Dvalue = 1.17
  Group = -> [C_element078,H_element072,N_element036]
  conduct = 2
  density = 1
  expand = 3
  formula = G4_POLYACRYLONITRILE
  name = G4_POLYACRYLONITRILE
  specific = 4
FEATURE [App::DocumentObjectGroupPython] C_element079  label="C_element : 16"  # scripted group (container) (typed FeaturePython)
  n = 16
  ref = C_element
FEATURE [App::DocumentObjectGroupPython] H_element073  label="H_element : 035"  # scripted group (container) (typed FeaturePython)
  n = 14
  ref = H_element
FEATURE [App::DocumentObjectGroupPython] O_element077  label="O_element : 038"  # scripted group (container) (typed FeaturePython)
  n = 3
  ref = O_element
FEATURE [App::DocumentObjectGroupPython] G4_POLYCARBONATE  # scripted group (container) (typed FeaturePython)
  Dunit = g/cm3
  Dvalue = 1.2
  Group = -> [C_element079,H_element073,O_element077]
  conduct = 2
  density = 1
  expand = 3
  formula = G4_POLYCARBONATE
  name = G4_POLYCARBONATE
  specific = 4
FEATURE [App::DocumentObjectGroupPython] C_element080  label="C_element : 038"  # scripted group (container) (typed FeaturePython)
  n = 8
  ref = C_element
FEATURE [App::DocumentObjectGroupPython] H_element074  label="H_element : 036"  # scripted group (container) (typed FeaturePython)
  n = 7
  ref = H_element
FEATURE [App::DocumentObjectGroupPython] Cl_element017  label="Cl_element : 007"  # scripted group (container) (typed FeaturePython)
  n = 1
  ref = Cl_element
FEATURE [App::DocumentObjectGroupPython] G4_POLYCHLOROSTYRENE  # scripted group (container) (typed FeaturePython)
  Dunit = g/cm3
  Dvalue = 1.3
  Group = -> [C_element080,H_element074,Cl_element017]
  conduct = 2
  density = 1
  expand = 3
  formula = G4_POLYCHLOROSTYRENE
  name = G4_POLYCHLOROSTYRENE
  specific = 4
FEATURE [App::DocumentObjectGroupPython] C_element081  label="C_element : 039"  # scripted group (container) (typed FeaturePython)
  n = 1
  ref = C_element
FEATURE [App::DocumentObjectGroupPython] H_element075  label="H_element : 037"  # scripted group (container) (typed FeaturePython)
  n = 2
  ref = H_element
FEATURE [App::DocumentObjectGroupPython] G4_POLYETHYLENE  # scripted group (container) (typed FeaturePython)
  Dunit = g/cm3
  Dvalue = 0.94
  Group = -> [C_element081,H_element075]
  conduct = 2
  density = 1
  expand = 3
  formula = G4_POLYETHYLENE
  name = G4_POLYETHYLENE
  specific = 4
FEATURE [App::DocumentObjectGroupPython] C_element082  label="C_element : 040"  # scripted group (container) (typed FeaturePython)
  n = 10
  ref = C_element
FEATURE [App::DocumentObjectGroupPython] H_element076  label="H_element : 038"  # scripted group (container) (typed FeaturePython)
  n = 8
  ref = H_element
FEATURE [App::DocumentObjectGroupPython] O_element078  label="O_element : 039"  # scripted group (container) (typed FeaturePython)
  n = 4
  ref = O_element
FEATURE [App::DocumentObjectGroupPython] G4_MYLAR  # scripted group (container) (typed FeaturePython)
  Dunit = g/cm3
  Dvalue = 1.4
  Group = -> [C_element082,H_element076,O_element078]
  conduct = 2
  density = 1
  expand = 3
  formula = G4_MYLAR
  name = G4_MYLAR
  specific = 4
FEATURE [App::DocumentObjectGroupPython] C_element083  label="C_element : 041"  # scripted group (container) (typed FeaturePython)
  n = 5
  ref = C_element
FEATURE [App::DocumentObjectGroupPython] H_element077  label="H_element : 039"  # scripted group (container) (typed FeaturePython)
  n = 8
  ref = H_element
FEATURE [App::DocumentObjectGroupPython] O_element079  label="O_element : 040"  # scripted group (container) (typed FeaturePython)
  n = 2
  ref = O_element
FEATURE [App::DocumentObjectGroupPython] G4_PLEXIGLASS  # scripted group (container) (typed FeaturePython)
  Dunit = g/cm3
  Dvalue = 1.19
  Group = -> [C_element083,H_element077,O_element079]
  conduct = 2
  density = 1
  expand = 3
  formula = G4_PLEXIGLASS
  name = G4_PLEXIGLASS
  specific = 4
FEATURE [App::DocumentObjectGroupPython] C_element084  label="C_element : 042"  # scripted group (container) (typed FeaturePython)
  n = 1
  ref = C_element
FEATURE [App::DocumentObjectGroupPython] H_element078  label="H_element : 040"  # scripted group (container) (typed FeaturePython)
  n = 2
  ref = H_element
FEATURE [App::DocumentObjectGroupPython] O_element080  label="O_element : 041"  # scripted group (container) (typed FeaturePython)
  n = 1
  ref = O_element
FEATURE [App::DocumentObjectGroupPython] G4_POLYOXYMETHYLENE  # scripted group (container) (typed FeaturePython)
  Dunit = g/cm3
  Dvalue = 1.425
  Group = -> [C_element084,H_element078,O_element080]
  conduct = 2
  density = 1
  expand = 3
  formula = G4_POLYOXYMETHYLENE
  name = G4_POLYOXYMETHYLENE
  specific = 4
FEATURE [App::DocumentObjectGroupPython] C_element085  label="C_element : 043"  # scripted group (container) (typed FeaturePython)
  n = 2
  ref = C_element
FEATURE [App::DocumentObjectGroupPython] H_element079  label="H_element : 041"  # scripted group (container) (typed FeaturePython)
  n = 4
  ref = H_element
FEATURE [App::DocumentObjectGroupPython] G4_POLYPROPYLENE  # scripted group (container) (typed FeaturePython)
  Dunit = g/cm3
  Dvalue = 0.9
  Group = -> [C_element085,H_element079]
  conduct = 2
  density = 1
  expand = 3
  formula = G4_POLYPROPYLENE
  name = G4_POLYPROPYLENE
  specific = 4
FEATURE [App::DocumentObjectGroupPython] C_element086  label="C_element : 044"  # scripted group (container) (typed FeaturePython)
  n = 8
  ref = C_element
FEATURE [App::DocumentObjectGroupPython] H_element080  label="H_element : 042"  # scripted group (container) (typed FeaturePython)
  n = 8
  ref = H_element
FEATURE [App::DocumentObjectGroupPython] G4_POLYSTYRENE  # scripted group (container) (typed FeaturePython)
  Dunit = g/cm3
  Dvalue = 1.06
  Group = -> [C_element086,H_element080]
  conduct = 2
  density = 1
  expand = 3
  formula = G4_POLYSTYRENE
  name = G4_POLYSTYRENE
  specific = 4
FEATURE [App::DocumentObjectGroupPython] C_element087  label="C_element : 045"  # scripted group (container) (typed FeaturePython)
  n = 2
  ref = C_element
FEATURE [App::DocumentObjectGroupPython] F_element014  label="F_element : 4"  # scripted group (container) (typed FeaturePython)
  n = 4
  ref = F_element
FEATURE [App::DocumentObjectGroupPython] G4_TEFLON  # scripted group (container) (typed FeaturePython)
  Dunit = g/cm3
  Dvalue = 2.2
  Group = -> [C_element087,F_element014]
  conduct = 2
  density = 1
  expand = 3
  formula = G4_TEFLON
  name = G4_TEFLON
  specific = 4
FEATURE [App::DocumentObjectGroupPython] C_element088  label="C_element : 046"  # scripted group (container) (typed FeaturePython)
  n = 2
  ref = C_element
FEATURE [App::DocumentObjectGroupPython] F_element015  label="F_element : 006"  # scripted group (container) (typed FeaturePython)
  n = 3
  ref = F_element
FEATURE [App::DocumentObjectGroupPython] Cl_element018  label="Cl_element : 008"  # scripted group (container) (typed FeaturePython)
  n = 1
  ref = Cl_element
FEATURE [App::DocumentObjectGroupPython] G4_POLYTRIFLUOROCHLOROETHYLENE  # scripted group (container) (typed FeaturePython)
  Dunit = g/cm3
  Dvalue = 2.1
  Group = -> [C_element088,F_element015,Cl_element018]
  conduct = 2
  density = 1
  expand = 3
  formula = G4_POLYTRIFLUOROCHLOROETHYLENE
  name = G4_POLYTRIFLUOROCHLOROETHYLENE
  specific = 4
FEATURE [App::DocumentObjectGroupPython] C_element089  label="C_element : 047"  # scripted group (container) (typed FeaturePython)
  n = 4
  ref = C_element
FEATURE [App::DocumentObjectGroupPython] H_element081  label="H_element : 043"  # scripted group (container) (typed FeaturePython)
  n = 6
  ref = H_element
FEATURE [App::DocumentObjectGroupPython] O_element081  label="O_element : 042"  # scripted group (container) (typed FeaturePython)
  n = 2
  ref = O_element
FEATURE [App::DocumentObjectGroupPython] G4_POLYVINYL_ACETATE  # scripted group (container) (typed FeaturePython)
  Dunit = g/cm3
  Dvalue = 1.19
  Group = -> [C_element089,H_element081,O_element081]
  conduct = 2
  density = 1
  expand = 3
  formula = G4_POLYVINYL_ACETATE
  name = G4_POLYVINYL_ACETATE
  specific = 4
FEATURE [App::DocumentObjectGroupPython] C_element090  label="C_element : 048"  # scripted group (container) (typed FeaturePython)
  n = 2
  ref = C_element
FEATURE [App::DocumentObjectGroupPython] H_element082  label="H_element : 044"  # scripted group (container) (typed FeaturePython)
  n = 4
  ref = H_element
FEATURE [App::DocumentObjectGroupPython] O_element082  label="O_element : 043"  # scripted group (container) (typed FeaturePython)
  n = 1
  ref = O_element
FEATURE [App::DocumentObjectGroupPython] G4_POLYVINYL_ALCOHOL  # scripted group (container) (typed FeaturePython)
  Dunit = g/cm3
  Dvalue = 1.3
  Group = -> [C_element090,H_element082,O_element082]
  conduct = 2
  density = 1
  expand = 3
  formula = G4_POLYVINYL_ALCOHOL
  name = G4_POLYVINYL_ALCOHOL
  specific = 4
FEATURE [App::DocumentObjectGroupPython] C_element091  label="C_element : 049"  # scripted group (container) (typed FeaturePython)
  n = 8
  ref = C_element
FEATURE [App::DocumentObjectGroupPython] H_element083  label="H_element : 045"  # scripted group (container) (typed FeaturePython)
  n = 14
  ref = H_element
FEATURE [App::DocumentObjectGroupPython] O_element083  label="O_element : 044"  # scripted group (container) (typed FeaturePython)
  n = 2
  ref = O_element
FEATURE [App::DocumentObjectGroupPython] G4_POLYVINYL_BUTYRAL  # scripted group (container) (typed FeaturePython)
  Dunit = g/cm3
  Dvalue = 1.12
  Group = -> [C_element091,H_element083,O_element083]
  conduct = 2
  density = 1
  expand = 3
  formula = G4_POLYVINYL_BUTYRAL
  name = G4_POLYVINYL_BUTYRAL
  specific = 4
FEATURE [App::DocumentObjectGroupPython] C_element092  label="C_element : 050"  # scripted group (container) (typed FeaturePython)
  n = 2
  ref = C_element
FEATURE [App::DocumentObjectGroupPython] H_element084  label="H_element : 046"  # scripted group (container) (typed FeaturePython)
  n = 3
  ref = H_element
FEATURE [App::DocumentObjectGroupPython] Cl_element019  label="Cl_element : 009"  # scripted group (container) (typed FeaturePython)
  n = 1
  ref = Cl_element
FEATURE [App::DocumentObjectGroupPython] G4_POLYVINYL_CHLORIDE  # scripted group (container) (typed FeaturePython)
  Dunit = g/cm3
  Dvalue = 1.3
  Group = -> [C_element092,H_element084,Cl_element019]
  conduct = 2
  density = 1
  expand = 3
  formula = G4_POLYVINYL_CHLORIDE
  name = G4_POLYVINYL_CHLORIDE
  specific = 4
FEATURE [App::DocumentObjectGroupPython] C_element093  label="C_element : 051"  # scripted group (container) (typed FeaturePython)
  n = 2
  ref = C_element
FEATURE [App::DocumentObjectGroupPython] H_element085  label="H_element : 047"  # scripted group (container) (typed FeaturePython)
  n = 2
  ref = H_element
FEATURE [App::DocumentObjectGroupPython] Cl_element020  label="Cl_element : 010"  # scripted group (container) (typed FeaturePython)
  n = 2
  ref = Cl_element
FEATURE [App::DocumentObjectGroupPython] G4_POLYVINYLIDENE_CHLORIDE  # scripted group (container) (typed FeaturePython)
  Dunit = g/cm3
  Dvalue = 1.7
  Group = -> [C_element093,H_element085,Cl_element020]
  conduct = 2
  density = 1
  expand = 3
  formula = G4_POLYVINYLIDENE_CHLORIDE
  name = G4_POLYVINYLIDENE_CHLORIDE
  specific = 4
FEATURE [App::DocumentObjectGroupPython] C_element094  label="C_element : 052"  # scripted group (container) (typed FeaturePython)
  n = 2
  ref = C_element
FEATURE [App::DocumentObjectGroupPython] H_element086  label="H_element : 048"  # scripted group (container) (typed FeaturePython)
  n = 2
  ref = H_element
FEATURE [App::DocumentObjectGroupPython] F_element016  label="F_element : 007"  # scripted group (container) (typed FeaturePython)
  n = 2
  ref = F_element
FEATURE [App::DocumentObjectGroupPython] G4_POLYVINYLIDENE_FLUORIDE  # scripted group (container) (typed FeaturePython)
  Dunit = g/cm3
  Dvalue = 1.76
  Group = -> [C_element094,H_element086,F_element016]
  conduct = 2
  density = 1
  expand = 3
  formula = G4_POLYVINYLIDENE_FLUORIDE
  name = G4_POLYVINYLIDENE_FLUORIDE
  specific = 4
FEATURE [App::DocumentObjectGroupPython] C_element095  label="C_element : 053"  # scripted group (container) (typed FeaturePython)
  n = 6
  ref = C_element
FEATURE [App::DocumentObjectGroupPython] H_element087  label="H_element : 9"  # scripted group (container) (typed FeaturePython)
  n = 9
  ref = H_element
FEATURE [App::DocumentObjectGroupPython] N_element037  label="N_element : 016"  # scripted group (container) (typed FeaturePython)
  n = 1
  ref = N_element
FEATURE [App::DocumentObjectGroupPython] O_element084  label="O_element : 045"  # scripted group (container) (typed FeaturePython)
  n = 1
  ref = O_element
FEATURE [App::DocumentObjectGroupPython] G4_POLYVINYL_PYRROLIDONE  # scripted group (container) (typed FeaturePython)
  Dunit = g/cm3
  Dvalue = 1.25
  Group = -> [C_element095,H_element087,N_element037,O_element084]
  conduct = 2
  density = 1
  expand = 3
  formula = G4_POLYVINYL_PYRROLIDONE
  name = G4_POLYVINYL_PYRROLIDONE
  specific = 4
FEATURE [App::DocumentObjectGroupPython] K_element008  label="K_element : 1"  # scripted group (container) (typed FeaturePython)
  n = 1
  ref = K_element
FEATURE [App::DocumentObjectGroupPython] I_element006  label="I_element : 003"  # scripted group (container) (typed FeaturePython)
  n = 1
  ref = I_element
FEATURE [App::DocumentObjectGroupPython] G4_POTASSIUM_IODIDE  # scripted group (container) (typed FeaturePython)
  Dunit = g/cm3
  Dvalue = 3.13
  Group = -> [K_element008,I_element006]
  conduct = 2
  density = 1
  expand = 3
  formula = G4_POTASSIUM_IODIDE
  name = G4_POTASSIUM_IODIDE
  specific = 4
FEATURE [App::DocumentObjectGroupPython] K_element009  label="K_element : 2"  # scripted group (container) (typed FeaturePython)
  n = 2
  ref = K_element
FEATURE [App::DocumentObjectGroupPython] O_element085  label="O_element : 046"  # scripted group (container) (typed FeaturePython)
  n = 1
  ref = O_element
FEATURE [App::DocumentObjectGroupPython] G4_POTASSIUM_OXIDE  # scripted group (container) (typed FeaturePython)
  Dunit = g/cm3
  Dvalue = 2.32
  Group = -> [K_element009,O_element085]
  conduct = 2
  density = 1
  expand = 3
  formula = G4_POTASSIUM_OXIDE
  name = G4_POTASSIUM_OXIDE
  specific = 4
FEATURE [App::DocumentObjectGroupPython] C_element096  label="C_element : 054"  # scripted group (container) (typed FeaturePython)
  n = 3
  ref = C_element
FEATURE [App::DocumentObjectGroupPython] H_element088  label="H_element : 049"  # scripted group (container) (typed FeaturePython)
  n = 8
  ref = H_element
FEATURE [App::DocumentObjectGroupPython] G4_PROPANE  # scripted group (container) (typed FeaturePython)
  Dunit = g/cm3
  Dvalue = 0.00187939
  Group = -> [C_element096,H_element088]
  conduct = 2
  density = 1
  expand = 3
  formula = G4_PROPANE
  name = G4_PROPANE
  specific = 4
FEATURE [App::DocumentObjectGroupPython] C_element097  label="C_element : 055"  # scripted group (container) (typed FeaturePython)
  n = 3
  ref = C_element
FEATURE [App::DocumentObjectGroupPython] H_element089  label="H_element : 050"  # scripted group (container) (typed FeaturePython)
  n = 8
  ref = H_element
FEATURE [App::DocumentObjectGroupPython] G4_lPROPANE  # scripted group (container) (typed FeaturePython)
  Dunit = g/cm3
  Dvalue = 0.43
  Group = -> [C_element097,H_element089]
  conduct = 2
  density = 1
  expand = 3
  formula = G4_lPROPANE
  name = G4_lPROPANE
  specific = 4
FEATURE [App::DocumentObjectGroupPython] C_element098  label="C_element : 056"  # scripted group (container) (typed FeaturePython)
  n = 3
  ref = C_element
FEATURE [App::DocumentObjectGroupPython] H_element090  label="H_element : 051"  # scripted group (container) (typed FeaturePython)
  n = 8
  ref = H_element
FEATURE [App::DocumentObjectGroupPython] O_element086  label="O_element : 047"  # scripted group (container) (typed FeaturePython)
  n = 1
  ref = O_element
FEATURE [App::DocumentObjectGroupPython] G4_N_PROPYL_ALCOHOL  label="G4_N-PROPYL_ALCOHOL"  # scripted group (container) (typed FeaturePython)
  Dunit = g/cm3
  Dvalue = 0.8035
  Group = -> [C_element098,H_element090,O_element086]
  conduct = 2
  density = 1
  expand = 3
  formula = G4_N-PROPYL_ALCOHOL
  name = G4_N-PROPYL_ALCOHOL
  specific = 4
FEATURE [App::DocumentObjectGroupPython] C_element099  label="C_element : 057"  # scripted group (container) (typed FeaturePython)
  n = 5
  ref = C_element
FEATURE [App::DocumentObjectGroupPython] H_element091  label="H_element : 052"  # scripted group (container) (typed FeaturePython)
  n = 5
  ref = H_element
FEATURE [App::DocumentObjectGroupPython] N_element038  label="N_element : 017"  # scripted group (container) (typed FeaturePython)
  n = 1
  ref = N_element
FEATURE [App::DocumentObjectGroupPython] G4_PYRIDINE  # scripted group (container) (typed FeaturePython)
  Dunit = g/cm3
  Dvalue = 0.9819
  Group = -> [C_element099,H_element091,N_element038]
  conduct = 2
  density = 1
  expand = 3
  formula = G4_PYRIDINE
  name = G4_PYRIDINE
  specific = 4
FEATURE [App::DocumentObjectGroupPython] H_element092  label="H_element : 0.144"  # scripted group (container) (typed FeaturePython)
  n = 0.143711
FEATURE [App::DocumentObjectGroupPython] C_element100  label="C_element : 0.856"  # scripted group (container) (typed FeaturePython)
  n = 0.856289
FEATURE [App::DocumentObjectGroupPython] G4_RUBBER_BUTYL  # scripted group (container) (typed FeaturePython)
  Dunit = g/cm3
  Dvalue = 0.92
  Group = -> [H_element092,C_element100]
  conduct = 2
  density = 1
  expand = 3
  formula = G4_RUBBER_BUTYL
  name = G4_RUBBER_BUTYL
  specific = 4
FEATURE [App::DocumentObjectGroupPython] H_element093  label="H_element : 0.118"  # scripted group (container) (typed FeaturePython)
  n = 0.118371
FEATURE [App::DocumentObjectGroupPython] C_element101  label="C_element : 0.882"  # scripted group (container) (typed FeaturePython)
  n = 0.881629
FEATURE [App::DocumentObjectGroupPython] G4_RUBBER_NATURAL  # scripted group (container) (typed FeaturePython)
  Dunit = g/cm3
  Dvalue = 0.92
  Group = -> [H_element093,C_element101]
  conduct = 2
  density = 1
  expand = 3
  formula = G4_RUBBER_NATURAL
  name = G4_RUBBER_NATURAL
  specific = 4
FEATURE [App::DocumentObjectGroupPython] H_element094  label="H_element : 0.145"  # scripted group (container) (typed FeaturePython)
  n = 0.05692
FEATURE [App::DocumentObjectGroupPython] C_element102  label="C_element : 0.543"  # scripted group (container) (typed FeaturePython)
  n = 0.542646
FEATURE [App::DocumentObjectGroupPython] Cl_element021  label="Cl_element : 0.400"  # scripted group (container) (typed FeaturePython)
  n = 0.400434
FEATURE [App::DocumentObjectGroupPython] G4_RUBBER_NEOPRENE  # scripted group (container) (typed FeaturePython)
  Dunit = g/cm3
  Dvalue = 1.23
  Group = -> [H_element094,C_element102,Cl_element021]
  conduct = 2
  density = 1
  expand = 3
  formula = G4_RUBBER_NEOPRENE
  name = G4_RUBBER_NEOPRENE
  specific = 4
FEATURE [App::DocumentObjectGroupPython] Si_element006  label="Si_element : 1"  # scripted group (container) (typed FeaturePython)
  n = 1
  ref = Si_element
FEATURE [App::DocumentObjectGroupPython] O_element087  label="O_element : 048"  # scripted group (container) (typed FeaturePython)
  n = 2
  ref = O_element
FEATURE [App::DocumentObjectGroupPython] G4_SILICON_DIOXIDE  # scripted group (container) (typed FeaturePython)
  Dunit = g/cm3
  Dvalue = 2.32
  Group = -> [Si_element006,O_element087]
  conduct = 2
  density = 1
  expand = 3
  formula = G4_SILICON_DIOXIDE
  name = G4_SILICON_DIOXIDE
  specific = 4
FEATURE [App::DocumentObjectGroupPython] Ag_element002  label="Ag_element : 1"  # scripted group (container) (typed FeaturePython)
  n = 1
  ref = Ag_element
FEATURE [App::DocumentObjectGroupPython] Br_element005  label="Br_element : 003"  # scripted group (container) (typed FeaturePython)
  n = 1
  ref = Br_element
FEATURE [App::DocumentObjectGroupPython] G4_SILVER_BROMIDE  # scripted group (container) (typed FeaturePython)
  Dunit = g/cm3
  Dvalue = 6.473
  Group = -> [Ag_element002,Br_element005]
  conduct = 2
  density = 1
  expand = 3
  formula = G4_SILVER_BROMIDE
  name = G4_SILVER_BROMIDE
  specific = 4
FEATURE [App::DocumentObjectGroupPython] Ag_element003  label="Ag_element : 002"  # scripted group (container) (typed FeaturePython)
  n = 1
  ref = Ag_element
FEATURE [App::DocumentObjectGroupPython] Cl_element022  label="Cl_element : 011"  # scripted group (container) (typed FeaturePython)
  n = 1
  ref = Cl_element
FEATURE [App::DocumentObjectGroupPython] G4_SILVER_CHLORIDE  # scripted group (container) (typed FeaturePython)
  Dunit = g/cm3
  Dvalue = 5.56
  Group = -> [Ag_element003,Cl_element022]
  conduct = 2
  density = 1
  expand = 3
  formula = G4_SILVER_CHLORIDE
  name = G4_SILVER_CHLORIDE
  specific = 4
FEATURE [App::DocumentObjectGroupPython] Br_element006  label="Br_element : 0.423"  # scripted group (container) (typed FeaturePython)
  n = 0.422895
FEATURE [App::DocumentObjectGroupPython] Ag_element004  label="Ag_element : 0.574"  # scripted group (container) (typed FeaturePython)
  n = 0.573748
FEATURE [App::DocumentObjectGroupPython] I_element007  label="I_element : 0.649"  # scripted group (container) (typed FeaturePython)
  n = 0.003357
FEATURE [App::DocumentObjectGroupPython] G4_SILVER_HALIDES  # scripted group (container) (typed FeaturePython)
  Dunit = g/cm3
  Dvalue = 6.47
  Group = -> [Br_element006,Ag_element004,I_element007]
  conduct = 2
  density = 1
  expand = 3
  formula = G4_SILVER_HALIDES
  name = G4_SILVER_HALIDES
  specific = 4
FEATURE [App::DocumentObjectGroupPython] Ag_element005  label="Ag_element : 003"  # scripted group (container) (typed FeaturePython)
  n = 1
  ref = Ag_element
FEATURE [App::DocumentObjectGroupPython] I_element008  label="I_element : 004"  # scripted group (container) (typed FeaturePython)
  n = 1
  ref = I_element
FEATURE [App::DocumentObjectGroupPython] G4_SILVER_IODIDE  # scripted group (container) (typed FeaturePython)
  Dunit = g/cm3
  Dvalue = 6.01
  Group = -> [Ag_element005,I_element008]
  conduct = 2
  density = 1
  expand = 3
  formula = G4_SILVER_IODIDE
  name = G4_SILVER_IODIDE
  specific = 4
FEATURE [App::DocumentObjectGroupPython] H_element095  label="H_element : 0.100"  # scripted group (container) (typed FeaturePython)
  n = 0.1
FEATURE [App::DocumentObjectGroupPython] C_element103  label="C_element : 0.204"  # scripted group (container) (typed FeaturePython)
  n = 0.204
FEATURE [App::DocumentObjectGroupPython] N_element039  label="N_element : 0.759"  # scripted group (container) (typed FeaturePython)
  n = 0.042
FEATURE [App::DocumentObjectGroupPython] O_element088  label="O_element : 0.645"  # scripted group (container) (typed FeaturePython)
  n = 0.645
FEATURE [App::DocumentObjectGroupPython] Na_element013  label="Na_element : 0.100"  # scripted group (container) (typed FeaturePython)
  n = 0.002
FEATURE [App::DocumentObjectGroupPython] P_element009  label="P_element : 0.107"  # scripted group (container) (typed FeaturePython)
  n = 0.001
FEATURE [App::DocumentObjectGroupPython] S_element020  label="S_element : 0.021"  # scripted group (container) (typed FeaturePython)
  n = 0.002
FEATURE [App::DocumentObjectGroupPython] Cl_element023  label="Cl_element : 0.590"  # scripted group (container) (typed FeaturePython)
  n = 0.003
FEATURE [App::DocumentObjectGroupPython] K_element010  label="K_element : 0.001"  # scripted group (container) (typed FeaturePython)
  n = 0.001
FEATURE [App::DocumentObjectGroupPython] G4_SKIN_ICRP  # scripted group (container) (typed FeaturePython)
  Dunit = g/cm3
  Dvalue = 1.09
  Group = -> [H_element095,C_element103,N_element039,O_element088,Na_element013,P_element009,S_element020,Cl_element023,K_element010]
  conduct = 2
  density = 1
  expand = 3
  formula = G4_SKIN_ICRP
  name = G4_SKIN_ICRP
  specific = 4
FEATURE [App::DocumentObjectGroupPython] Na_element014  label="Na_element : 2"  # scripted group (container) (typed FeaturePython)
  n = 2
  ref = Na_element
FEATURE [App::DocumentObjectGroupPython] C_element104  label="C_element : 058"  # scripted group (container) (typed FeaturePython)
  n = 1
  ref = C_element
FEATURE [App::DocumentObjectGroupPython] O_element089  label="O_element : 049"  # scripted group (container) (typed FeaturePython)
  n = 3
  ref = O_element
FEATURE [App::DocumentObjectGroupPython] G4_SODIUM_CARBONATE  # scripted group (container) (typed FeaturePython)
  Dunit = g/cm3
  Dvalue = 2.532
  Group = -> [Na_element014,C_element104,O_element089]
  conduct = 2
  density = 1
  expand = 3
  formula = G4_SODIUM_CARBONATE
  name = G4_SODIUM_CARBONATE
  specific = 4
FEATURE [App::DocumentObjectGroupPython] Na_element015  label="Na_element : 1"  # scripted group (container) (typed FeaturePython)
  n = 1
  ref = Na_element
FEATURE [App::DocumentObjectGroupPython] I_element009  label="I_element : 005"  # scripted group (container) (typed FeaturePython)
  n = 1
  ref = I_element
FEATURE [App::DocumentObjectGroupPython] G4_SODIUM_IODIDE  # scripted group (container) (typed FeaturePython)
  Dunit = g/cm3
  Dvalue = 3.667
  Group = -> [Na_element015,I_element009]
  conduct = 2
  density = 1
  expand = 3
  formula = G4_SODIUM_IODIDE
  name = G4_SODIUM_IODIDE
  specific = 4
FEATURE [App::DocumentObjectGroupPython] Na_element016  label="Na_element : 003"  # scripted group (container) (typed FeaturePython)
  n = 2
  ref = Na_element
FEATURE [App::DocumentObjectGroupPython] O_element090  label="O_element : 050"  # scripted group (container) (typed FeaturePython)
  n = 1
  ref = O_element
FEATURE [App::DocumentObjectGroupPython] G4_SODIUM_MONOXIDE  # scripted group (container) (typed FeaturePython)
  Dunit = g/cm3
  Dvalue = 2.27
  Group = -> [Na_element016,O_element090]
  conduct = 2
  density = 1
  expand = 3
  formula = G4_SODIUM_MONOXIDE
  name = G4_SODIUM_MONOXIDE
  specific = 4
FEATURE [App::DocumentObjectGroupPython] Na_element017  label="Na_element : 004"  # scripted group (container) (typed FeaturePython)
  n = 1
  ref = Na_element
FEATURE [App::DocumentObjectGroupPython] N_element040  label="N_element : 018"  # scripted group (container) (typed FeaturePython)
  n = 1
  ref = N_element
FEATURE [App::DocumentObjectGroupPython] O_element091  label="O_element : 051"  # scripted group (container) (typed FeaturePython)
  n = 3
  ref = O_element
FEATURE [App::DocumentObjectGroupPython] G4_SODIUM_NITRATE  # scripted group (container) (typed FeaturePython)
  Dunit = g/cm3
  Dvalue = 2.261
  Group = -> [Na_element017,N_element040,O_element091]
  conduct = 2
  density = 1
  expand = 3
  formula = G4_SODIUM_NITRATE
  name = G4_SODIUM_NITRATE
  specific = 4
FEATURE [App::DocumentObjectGroupPython] C_element105  label="C_element : 059"  # scripted group (container) (typed FeaturePython)
  n = 14
  ref = C_element
FEATURE [App::DocumentObjectGroupPython] H_element096  label="H_element : 053"  # scripted group (container) (typed FeaturePython)
  n = 12
  ref = H_element
FEATURE [App::DocumentObjectGroupPython] G4_STILBENE  # scripted group (container) (typed FeaturePython)
  Dunit = g/cm3
  Dvalue = 0.9707
  Group = -> [C_element105,H_element096]
  conduct = 2
  density = 1
  expand = 3
  formula = G4_STILBENE
  name = G4_STILBENE
  specific = 4
FEATURE [App::DocumentObjectGroupPython] C_element106  label="C_element : 12"  # scripted group (container) (typed FeaturePython)
  n = 12
  ref = C_element
FEATURE [App::DocumentObjectGroupPython] H_element097  label="H_element : 22"  # scripted group (container) (typed FeaturePython)
  n = 22
  ref = H_element
FEATURE [App::DocumentObjectGroupPython] O_element092  label="O_element : 11"  # scripted group (container) (typed FeaturePython)
  n = 11
  ref = O_element
FEATURE [App::DocumentObjectGroupPython] G4_SUCROSE  # scripted group (container) (typed FeaturePython)
  Dunit = g/cm3
  Dvalue = 1.5805
  Group = -> [C_element106,H_element097,O_element092]
  conduct = 2
  density = 1
  expand = 3
  formula = G4_SUCROSE
  name = G4_SUCROSE
  specific = 4
FEATURE [App::DocumentObjectGroupPython] C_element107  label="C_element : 18"  # scripted group (container) (typed FeaturePython)
  n = 18
  ref = C_element
FEATURE [App::DocumentObjectGroupPython] H_element098  label="H_element : 054"  # scripted group (container) (typed FeaturePython)
  n = 14
  ref = H_element
FEATURE [App::DocumentObjectGroupPython] G4_TERPHENYL  # scripted group (container) (typed FeaturePython)
  Dunit = g/cm3
  Dvalue = 1.24
  Group = -> [C_element107,H_element098]
  conduct = 2
  density = 1
  expand = 3
  formula = G4_TERPHENYL
  name = G4_TERPHENYL
  specific = 4
FEATURE [App::DocumentObjectGroupPython] H_element099  label="H_element : 0.146"  # scripted group (container) (typed FeaturePython)
  n = 0.106
FEATURE [App::DocumentObjectGroupPython] C_element108  label="C_element : 0.883"  # scripted group (container) (typed FeaturePython)
  n = 0.099
FEATURE [App::DocumentObjectGroupPython] N_element041  label="N_element : 0.020"  # scripted group (container) (typed FeaturePython)
  n = 0.02
FEATURE [App::DocumentObjectGroupPython] O_element093  label="O_element : 0.766"  # scripted group (container) (typed FeaturePython)
  n = 0.766
FEATURE [App::DocumentObjectGroupPython] Na_element018  label="Na_element : 0.101"  # scripted group (container) (typed FeaturePython)
  n = 0.002
FEATURE [App::DocumentObjectGroupPython] P_element010  label="P_element : 0.108"  # scripted group (container) (typed FeaturePython)
  n = 0.001
FEATURE [App::DocumentObjectGroupPython] S_element021  label="S_element : 0.022"  # scripted group (container) (typed FeaturePython)
  n = 0.002
FEATURE [App::DocumentObjectGroupPython] Cl_element024  label="Cl_element : 0.002"  # scripted group (container) (typed FeaturePython)
  n = 0.002
FEATURE [App::DocumentObjectGroupPython] K_element011  label="K_element : 0.017"  # scripted group (container) (typed FeaturePython)
  n = 0.002
FEATURE [App::DocumentObjectGroupPython] G4_TESTIS_ICRP  # scripted group (container) (typed FeaturePython)
  Dunit = g/cm3
  Dvalue = 1.04
  Group = -> [H_element099,C_element108,N_element041,O_element093,Na_element018,P_element010,S_element021,Cl_element024,K_element011]
  conduct = 2
  density = 1
  expand = 3
  formula = G4_TESTIS_ICRP
  name = G4_TESTIS_ICRP
  specific = 4
FEATURE [App::DocumentObjectGroupPython] C_element109  label="C_element : 060"  # scripted group (container) (typed FeaturePython)
  n = 2
  ref = C_element
FEATURE [App::DocumentObjectGroupPython] Cl_element025  label="Cl_element : 012"  # scripted group (container) (typed FeaturePython)
  n = 4
  ref = Cl_element
FEATURE [App::DocumentObjectGroupPython] G4_TETRACHLOROETHYLENE  # scripted group (container) (typed FeaturePython)
  Dunit = g/cm3
  Dvalue = 1.625
  Group = -> [C_element109,Cl_element025]
  conduct = 2
  density = 1
  expand = 3
  formula = G4_TETRACHLOROETHYLENE
  name = G4_TETRACHLOROETHYLENE
  specific = 4
FEATURE [App::DocumentObjectGroupPython] Tl_element001  label="Tl_element : 1"  # scripted group (container) (typed FeaturePython)
  n = 1
  ref = Tl_element
FEATURE [App::DocumentObjectGroupPython] Cl_element026  label="Cl_element : 013"  # scripted group (container) (typed FeaturePython)
  n = 1
  ref = Cl_element
FEATURE [App::DocumentObjectGroupPython] G4_THALLIUM_CHLORIDE  # scripted group (container) (typed FeaturePython)
  Dunit = g/cm3
  Dvalue = 7.004
  Group = -> [Tl_element001,Cl_element026]
  conduct = 2
  density = 1
  expand = 3
  formula = G4_THALLIUM_CHLORIDE
  name = G4_THALLIUM_CHLORIDE
  specific = 4
FEATURE [App::DocumentObjectGroupPython] H_element100  label="H_element : 0.147"  # scripted group (container) (typed FeaturePython)
  n = 0.105
FEATURE [App::DocumentObjectGroupPython] C_element110  label="C_element : 0.256"  # scripted group (container) (typed FeaturePython)
  n = 0.256
FEATURE [App::DocumentObjectGroupPython] N_element042  label="N_element : 0.760"  # scripted group (container) (typed FeaturePython)
  n = 0.027
FEATURE [App::DocumentObjectGroupPython] O_element094  label="O_element : 0.602"  # scripted group (container) (typed FeaturePython)
  n = 0.602
FEATURE [App::DocumentObjectGroupPython] Na_element019  label="Na_element : 0.102"  # scripted group (container) (typed FeaturePython)
  n = 0.001
FEATURE [App::DocumentObjectGroupPython] P_element011  label="P_element : 0.109"  # scripted group (container) (typed FeaturePython)
  n = 0.002
FEATURE [App::DocumentObjectGroupPython] S_element022  label="S_element : 0.023"  # scripted group (container) (typed FeaturePython)
  n = 0.003
FEATURE [App::DocumentObjectGroupPython] Cl_element027  label="Cl_element : 0.591"  # scripted group (container) (typed FeaturePython)
  n = 0.002
FEATURE [App::DocumentObjectGroupPython] K_element012  label="K_element : 0.018"  # scripted group (container) (typed FeaturePython)
  n = 0.002
FEATURE [App::DocumentObjectGroupPython] G4_TISSUE_SOFT_ICRP  # scripted group (container) (typed FeaturePython)
  Dunit = g/cm3
  Dvalue = 1.03
  Group = -> [H_element100,C_element110,N_element042,O_element094,Na_element019,P_element011,S_element022,Cl_element027,K_element012]
  conduct = 2
  density = 1
  expand = 3
  formula = G4_TISSUE_SOFT_ICRP
  name = G4_TISSUE_SOFT_ICRP
  specific = 4
FEATURE [App::DocumentObjectGroupPython] H_element101  label="H_element : 0.148"  # scripted group (container) (typed FeaturePython)
  n = 0.101
FEATURE [App::DocumentObjectGroupPython] C_element111  label="C_element : 0.111"  # scripted group (container) (typed FeaturePython)
  n = 0.111
FEATURE [App::DocumentObjectGroupPython] N_element043  label="N_element : 0.026"  # scripted group (container) (typed FeaturePython)
  n = 0.026
FEATURE [App::DocumentObjectGroupPython] O_element095  label="O_element : 0.762"  # scripted group (container) (typed FeaturePython)
  n = 0.762
FEATURE [App::DocumentObjectGroupPython] G4_TISSUE_SOFT_ICRU_4  label="G4_TISSUE_SOFT_ICRU-4"  # scripted group (container) (typed FeaturePython)
  Dunit = g/cm3
  Dvalue = 1
  Group = -> [H_element101,C_element111,N_element043,O_element095]
  conduct = 2
  density = 1
  expand = 3
  formula = G4_TISSUE_SOFT_ICRU-4
  name = G4_TISSUE_SOFT_ICRU-4
  specific = 4
FEATURE [App::DocumentObjectGroupPython] H_element102  label="H_element : 0.149"  # scripted group (container) (typed FeaturePython)
  n = 0.101869
FEATURE [App::DocumentObjectGroupPython] C_element112  label="C_element : 0.456"  # scripted group (container) (typed FeaturePython)
  n = 0.456179
FEATURE [App::DocumentObjectGroupPython] N_element044  label="N_element : 0.761"  # scripted group (container) (typed FeaturePython)
  n = 0.035172
FEATURE [App::DocumentObjectGroupPython] O_element096  label="O_element : 0.407"  # scripted group (container) (typed FeaturePython)
  n = 0.40678
FEATURE [App::DocumentObjectGroupPython] G4_TISSUE_METHANE  label="G4_TISSUE-METHANE"  # scripted group (container) (typed FeaturePython)
  Dunit = g/cm3
  Dvalue = 0.00106409
  Group = -> [H_element102,C_element112,N_element044,O_element096]
  conduct = 2
  density = 1
  expand = 3
  formula = G4_TISSUE-METHANE
  name = G4_TISSUE-METHANE
  specific = 4
FEATURE [App::DocumentObjectGroupPython] H_element103  label="H_element : 0.103"  # scripted group (container) (typed FeaturePython)
  n = 0.102672
FEATURE [App::DocumentObjectGroupPython] C_element113  label="C_element : 0.569"  # scripted group (container) (typed FeaturePython)
  n = 0.56894
FEATURE [App::DocumentObjectGroupPython] N_element045  label="N_element : 0.762"  # scripted group (container) (typed FeaturePython)
  n = 0.035022
FEATURE [App::DocumentObjectGroupPython] O_element097  label="O_element : 0.293"  # scripted group (container) (typed FeaturePython)
  n = 0.293366
FEATURE [App::DocumentObjectGroupPython] G4_TISSUE_PROPANE  label="G4_TISSUE-PROPANE"  # scripted group (container) (typed FeaturePython)
  Dunit = g/cm3
  Dvalue = 0.00182628
  Group = -> [H_element103,C_element113,N_element045,O_element097]
  conduct = 2
  density = 1
  expand = 3
  formula = G4_TISSUE-PROPANE
  name = G4_TISSUE-PROPANE
  specific = 4
FEATURE [App::DocumentObjectGroupPython] Ti_element003  label="Ti_element : 1"  # scripted group (container) (typed FeaturePython)
  n = 1
  ref = Ti_element
FEATURE [App::DocumentObjectGroupPython] O_element098  label="O_element : 052"  # scripted group (container) (typed FeaturePython)
  n = 2
  ref = O_element
FEATURE [App::DocumentObjectGroupPython] G4_TITANIUM_DIOXIDE  # scripted group (container) (typed FeaturePython)
  Dunit = g/cm3
  Dvalue = 4.26
  Group = -> [Ti_element003,O_element098]
  conduct = 2
  density = 1
  expand = 3
  formula = G4_TITANIUM_DIOXIDE
  name = G4_TITANIUM_DIOXIDE
  specific = 4
FEATURE [App::DocumentObjectGroupPython] C_element114  label="C_element : 061"  # scripted group (container) (typed FeaturePython)
  n = 7
  ref = C_element
FEATURE [App::DocumentObjectGroupPython] H_element104  label="H_element : 055"  # scripted group (container) (typed FeaturePython)
  n = 8
  ref = H_element
FEATURE [App::DocumentObjectGroupPython] G4_TOLUENE  # scripted group (container) (typed FeaturePython)
  Dunit = g/cm3
  Dvalue = 0.8669
  Group = -> [C_element114,H_element104]
  conduct = 2
  density = 1
  expand = 3
  formula = G4_TOLUENE
  name = G4_TOLUENE
  specific = 4
FEATURE [App::DocumentObjectGroupPython] C_element115  label="C_element : 062"  # scripted group (container) (typed FeaturePython)
  n = 2
  ref = C_element
FEATURE [App::DocumentObjectGroupPython] H_element105  label="H_element : 056"  # scripted group (container) (typed FeaturePython)
  n = 1
  ref = H_element
FEATURE [App::DocumentObjectGroupPython] Cl_element028  label="Cl_element : 014"  # scripted group (container) (typed FeaturePython)
  n = 3
  ref = Cl_element
FEATURE [App::DocumentObjectGroupPython] G4_TRICHLOROETHYLENE  # scripted group (container) (typed FeaturePython)
  Dunit = g/cm3
  Dvalue = 1.46
  Group = -> [C_element115,H_element105,Cl_element028]
  conduct = 2
  density = 1
  expand = 3
  formula = G4_TRICHLOROETHYLENE
  name = G4_TRICHLOROETHYLENE
  specific = 4
FEATURE [App::DocumentObjectGroupPython] C_element116  label="C_element : 063"  # scripted group (container) (typed FeaturePython)
  n = 6
  ref = C_element
FEATURE [App::DocumentObjectGroupPython] H_element106  label="H_element : 15"  # scripted group (container) (typed FeaturePython)
  n = 15
  ref = H_element
FEATURE [App::DocumentObjectGroupPython] O_element099  label="O_element : 053"  # scripted group (container) (typed FeaturePython)
  n = 4
  ref = O_element
FEATURE [App::DocumentObjectGroupPython] P_element012  label="P_element : 1"  # scripted group (container) (typed FeaturePython)
  n = 1
  ref = P_element
FEATURE [App::DocumentObjectGroupPython] G4_TRIETHYL_PHOSPHATE  # scripted group (container) (typed FeaturePython)
  Dunit = g/cm3
  Dvalue = 1.07
  Group = -> [C_element116,H_element106,O_element099,P_element012]
  conduct = 2
  density = 1
  expand = 3
  formula = G4_TRIETHYL_PHOSPHATE
  name = G4_TRIETHYL_PHOSPHATE
  specific = 4
FEATURE [App::DocumentObjectGroupPython] W_element003  label="W_element : 003"  # scripted group (container) (typed FeaturePython)
  n = 1
  ref = W_element
FEATURE [App::DocumentObjectGroupPython] F_element017  label="F_element : 6"  # scripted group (container) (typed FeaturePython)
  n = 6
  ref = F_element
FEATURE [App::DocumentObjectGroupPython] G4_TUNGSTEN_HEXAFLUORIDE  # scripted group (container) (typed FeaturePython)
  Dunit = g/cm3
  Dvalue = 2.4
  Group = -> [W_element003,F_element017]
  conduct = 2
  density = 1
  expand = 3
  formula = G4_TUNGSTEN_HEXAFLUORIDE
  name = G4_TUNGSTEN_HEXAFLUORIDE
  specific = 4
FEATURE [App::DocumentObjectGroupPython] U_element001  label="U_element : 1"  # scripted group (container) (typed FeaturePython)
  n = 1
  ref = U_element
FEATURE [App::DocumentObjectGroupPython] C_element117  label="C_element : 064"  # scripted group (container) (typed FeaturePython)
  n = 2
  ref = C_element
FEATURE [App::DocumentObjectGroupPython] G4_URANIUM_DICARBIDE  # scripted group (container) (typed FeaturePython)
  Dunit = g/cm3
  Dvalue = 11.28
  Group = -> [U_element001,C_element117]
  conduct = 2
  density = 1
  expand = 3
  formula = G4_URANIUM_DICARBIDE
  name = G4_URANIUM_DICARBIDE
  specific = 4
FEATURE [App::DocumentObjectGroupPython] U_element002  label="U_element : 002"  # scripted group (container) (typed FeaturePython)
  n = 1
  ref = U_element
FEATURE [App::DocumentObjectGroupPython] C_element118  label="C_element : 065"  # scripted group (container) (typed FeaturePython)
  n = 1
  ref = C_element
FEATURE [App::DocumentObjectGroupPython] G4_URANIUM_MONOCARBIDE  # scripted group (container) (typed FeaturePython)
  Dunit = g/cm3
  Dvalue = 13.63
  Group = -> [U_element002,C_element118]
  conduct = 2
  density = 1
  expand = 3
  formula = G4_URANIUM_MONOCARBIDE
  name = G4_URANIUM_MONOCARBIDE
  specific = 4
FEATURE [App::DocumentObjectGroupPython] U_element003  label="U_element : 003"  # scripted group (container) (typed FeaturePython)
  n = 1
  ref = U_element
FEATURE [App::DocumentObjectGroupPython] O_element100  label="O_element : 054"  # scripted group (container) (typed FeaturePython)
  n = 2
  ref = O_element
FEATURE [App::DocumentObjectGroupPython] G4_URANIUM_OXIDE  # scripted group (container) (typed FeaturePython)
  Dunit = g/cm3
  Dvalue = 10.96
  Group = -> [U_element003,O_element100]
  conduct = 2
  density = 1
  expand = 3
  formula = G4_URANIUM_OXIDE
  name = G4_URANIUM_OXIDE
  specific = 4
FEATURE [App::DocumentObjectGroupPython] C_element119  label="C_element : 066"  # scripted group (container) (typed FeaturePython)
  n = 1
  ref = C_element
FEATURE [App::DocumentObjectGroupPython] H_element107  label="H_element : 057"  # scripted group (container) (typed FeaturePython)
  n = 4
  ref = H_element
FEATURE [App::DocumentObjectGroupPython] N_element046  label="N_element : 019"  # scripted group (container) (typed FeaturePython)
  n = 2
  ref = N_element
FEATURE [App::DocumentObjectGroupPython] O_element101  label="O_element : 055"  # scripted group (container) (typed FeaturePython)
  n = 1
  ref = O_element
FEATURE [App::DocumentObjectGroupPython] G4_UREA  # scripted group (container) (typed FeaturePython)
  Dunit = g/cm3
  Dvalue = 1.323
  Group = -> [C_element119,H_element107,N_element046,O_element101]
  conduct = 2
  density = 1
  expand = 3
  formula = G4_UREA
  name = G4_UREA
  specific = 4
FEATURE [App::DocumentObjectGroupPython] C_element120  label="C_element : 067"  # scripted group (container) (typed FeaturePython)
  n = 5
  ref = C_element
FEATURE [App::DocumentObjectGroupPython] H_element108  label="H_element : 058"  # scripted group (container) (typed FeaturePython)
  n = 11
  ref = H_element
FEATURE [App::DocumentObjectGroupPython] N_element047  label="N_element : 020"  # scripted group (container) (typed FeaturePython)
  n = 1
  ref = N_element
FEATURE [App::DocumentObjectGroupPython] O_element102  label="O_element : 056"  # scripted group (container) (typed FeaturePython)
  n = 2
  ref = O_element
FEATURE [App::DocumentObjectGroupPython] G4_VALINE  # scripted group (container) (typed FeaturePython)
  Dunit = g/cm3
  Dvalue = 1.23
  Group = -> [C_element120,H_element108,N_element047,O_element102]
  conduct = 2
  density = 1
  expand = 3
  formula = G4_VALINE
  name = G4_VALINE
  specific = 4
FEATURE [App::DocumentObjectGroupPython] H_element109  label="H_element : 0.009"  # scripted group (container) (typed FeaturePython)
  n = 0.009417
FEATURE [App::DocumentObjectGroupPython] C_element121  label="C_element : 0.281"  # scripted group (container) (typed FeaturePython)
  n = 0.280555
FEATURE [App::DocumentObjectGroupPython] F_element018  label="F_element : 0.710"  # scripted group (container) (typed FeaturePython)
  n = 0.710028
FEATURE [App::DocumentObjectGroupPython] G4_VITON  # scripted group (container) (typed FeaturePython)
  Dunit = g/cm3
  Dvalue = 1.8
  Group = -> [H_element109,C_element121,F_element018]
  conduct = 2
  density = 1
  expand = 3
  formula = G4_VITON
  name = G4_VITON
  specific = 4
FEATURE [App::DocumentObjectGroupPython] H_element110  label="H_element : 059"  # scripted group (container) (typed FeaturePython)
  n = 2
  ref = H_element
FEATURE [App::DocumentObjectGroupPython] O_element103  label="O_element : 057"  # scripted group (container) (typed FeaturePython)
  n = 1
  ref = O_element
FEATURE [App::DocumentObjectGroupPython] G4_WATER  # scripted group (container) (typed FeaturePython)
  Dunit = g/cm3
  Dvalue = 1
  Group = -> [H_element110,O_element103]
  conduct = 2
  density = 1
  expand = 3
  formula = G4_WATER
  name = G4_WATER
  specific = 4
FEATURE [App::DocumentObjectGroupPython] H_element111  label="H_element : 060"  # scripted group (container) (typed FeaturePython)
  n = 2
  ref = H_element
FEATURE [App::DocumentObjectGroupPython] O_element104  label="O_element : 058"  # scripted group (container) (typed FeaturePython)
  n = 1
  ref = O_element
FEATURE [App::DocumentObjectGroupPython] G4_WATER_VAPOR  # scripted group (container) (typed FeaturePython)
  Dunit = g/cm3
  Dvalue = 0.000756182
  Group = -> [H_element111,O_element104]
  conduct = 2
  density = 1
  expand = 3
  formula = G4_WATER_VAPOR
  name = G4_WATER_VAPOR
  specific = 4
FEATURE [App::DocumentObjectGroupPython] C_element122  label="C_element : 068"  # scripted group (container) (typed FeaturePython)
  n = 8
  ref = C_element
FEATURE [App::DocumentObjectGroupPython] H_element112  label="H_element : 061"  # scripted group (container) (typed FeaturePython)
  n = 10
  ref = H_element
FEATURE [App::DocumentObjectGroupPython] G4_XYLENE  # scripted group (container) (typed FeaturePython)
  Dunit = g/cm3
  Dvalue = 0.87
  Group = -> [C_element122,H_element112]
  conduct = 2
  density = 1
  expand = 3
  formula = G4_XYLENE
  name = G4_XYLENE
  specific = 4
FEATURE [App::DocumentObjectGroupPython] C_element123  label="C_element : 069"  # scripted group (container) (typed FeaturePython)
  n = 1
  ref = C_element
FEATURE [App::DocumentObjectGroupPython] G4_GRAPHITE  # scripted group (container) (typed FeaturePython)
  Dunit = g/cm3
  Dvalue = 2.21
  Group = -> [C_element123]
  conduct = 2
  density = 1
  expand = 3
  formula = G4_GRAPHITE
  name = G4_GRAPHITE
  specific = 4
FEATURE [App::DocumentObjectGroupPython] NIST  # scripted group (container) (typed FeaturePython)
  Group = -> [G4_A_150_TISSUE,G4_ACETONE,G4_ACETYLENE,G4_ADENINE,G4_ADIPOSE_TISSUE_ICRP,G4_AIR,G4_ALANINE,G4_ALUMINUM_OXIDE,G4_AMBER,G4_AMMONIA,G4_ANILINE,G4_ANTHRACENE,G4_B_100_BONE,G4_BAKELITE,G4_BARIUM_FLUORIDE,G4_BARIUM_SULFATE,G4_BENZENE,G4_BERYLLIUM_OXIDE,G4_BGO,G4_BLOOD_ICRP,G4_BONE_COMPACT_ICRU,G4_BONE_CORTICAL_ICRP,G4_BORON_CARBIDE,G4_BORON_OXIDE,G4_BRAIN_ICRP,G4_BUTANE,G4_N_BUTYL_ALCOHOL,G4_C_552,+152 more]
FEATURE [App::DocumentObjectGroupPython] H_element113  label="H_element : 062"  # scripted group (container) (typed FeaturePython)
  n = 1
  ref = H_element
FEATURE [App::DocumentObjectGroupPython] G4_H  # scripted group (container) (typed FeaturePython)
  Dunit = g/cm3
  Dvalue = 8.3748e-05
  Group = -> [H_element113]
  conduct = 2
  density = 1
  expand = 3
  formula = H
  name = G4_H
  specific = 4
FEATURE [App::DocumentObjectGroupPython] He_element001  label="He_element : 1"  # scripted group (container) (typed FeaturePython)
  n = 1
  ref = He_element
FEATURE [App::DocumentObjectGroupPython] G4_He  # scripted group (container) (typed FeaturePython)
  Dunit = g/cm3
  Dvalue = 0.000166322
  Group = -> [He_element001]
  conduct = 2
  density = 1
  expand = 3
  formula = He
  name = G4_He
  specific = 4
FEATURE [App::DocumentObjectGroupPython] Li_element008  label="Li_element : 008"  # scripted group (container) (typed FeaturePython)
  n = 1
  ref = Li_element
FEATURE [App::DocumentObjectGroupPython] G4_Li  # scripted group (container) (typed FeaturePython)
  Dunit = g/cm3
  Dvalue = 0.534
  Group = -> [Li_element008]
  conduct = 2
  density = 1
  expand = 3
  formula = Li
  name = G4_Li
  specific = 4
FEATURE [App::DocumentObjectGroupPython] Be_element002  label="Be_element : 002"  # scripted group (container) (typed FeaturePython)
  n = 1
  ref = Be_element
FEATURE [App::DocumentObjectGroupPython] G4_Be  # scripted group (container) (typed FeaturePython)
  Dunit = g/cm3
  Dvalue = 1.848
  Group = -> [Be_element002]
  conduct = 2
  density = 1
  expand = 3
  formula = Be
  name = G4_Be
  specific = 4
FEATURE [App::DocumentObjectGroupPython] B_element007  label="B_element : 007"  # scripted group (container) (typed FeaturePython)
  n = 1
  ref = B_element
FEATURE [App::DocumentObjectGroupPython] G4_B  # scripted group (container) (typed FeaturePython)
  Dunit = g/cm3
  Dvalue = 2.37
  Group = -> [B_element007]
  conduct = 2
  density = 1
  expand = 3
  formula = B
  name = G4_B
  specific = 4
FEATURE [App::DocumentObjectGroupPython] C_element124  label="C_element : 070"  # scripted group (container) (typed FeaturePython)
  n = 1
  ref = C_element
FEATURE [App::DocumentObjectGroupPython] G4_C  # scripted group (container) (typed FeaturePython)
  Dunit = g/cm3
  Dvalue = 2
  Group = -> [C_element124]
  conduct = 2
  density = 1
  expand = 3
  formula = C
  name = G4_C
  specific = 4
FEATURE [App::DocumentObjectGroupPython] N_element048  label="N_element : 021"  # scripted group (container) (typed FeaturePython)
  n = 1
  ref = N_element
FEATURE [App::DocumentObjectGroupPython] G4_N  # scripted group (container) (typed FeaturePython)
  Dunit = g/cm3
  Dvalue = 0.0011652
  Group = -> [N_element048]
  conduct = 2
  density = 1
  expand = 3
  formula = N
  name = G4_N
  specific = 4
FEATURE [App::DocumentObjectGroupPython] O_element105  label="O_element : 059"  # scripted group (container) (typed FeaturePython)
  n = 1
  ref = O_element
FEATURE [App::DocumentObjectGroupPython] G4_O  # scripted group (container) (typed FeaturePython)
  Dunit = g/cm3
  Dvalue = 0.00133151
  Group = -> [O_element105]
  conduct = 2
  density = 1
  expand = 3
  formula = O
  name = G4_O
  specific = 4
FEATURE [App::DocumentObjectGroupPython] F_element019  label="F_element : 008"  # scripted group (container) (typed FeaturePython)
  n = 1
  ref = F_element
FEATURE [App::DocumentObjectGroupPython] G4_F  # scripted group (container) (typed FeaturePython)
  Dunit = g/cm3
  Dvalue = 0.00158029
  Group = -> [F_element019]
  conduct = 2
  density = 1
  expand = 3
  formula = F
  name = G4_F
  specific = 4
FEATURE [App::DocumentObjectGroupPython] Ne_element001  label="Ne_element : 1"  # scripted group (container) (typed FeaturePython)
  n = 1
  ref = Ne_element
FEATURE [App::DocumentObjectGroupPython] G4_Ne  # scripted group (container) (typed FeaturePython)
  Dunit = g/cm3
  Dvalue = 0.000838505
  Group = -> [Ne_element001]
  conduct = 2
  density = 1
  expand = 3
  formula = Ne
  name = G4_Ne
  specific = 4
FEATURE [App::DocumentObjectGroupPython] Na_element020  label="Na_element : 005"  # scripted group (container) (typed FeaturePython)
  n = 1
  ref = Na_element
FEATURE [App::DocumentObjectGroupPython] G4_Na  # scripted group (container) (typed FeaturePython)
  Dunit = g/cm3
  Dvalue = 0.971
  Group = -> [Na_element020]
  conduct = 2
  density = 1
  expand = 3
  formula = Na
  name = G4_Na
  specific = 4
FEATURE [App::DocumentObjectGroupPython] Mg_element011  label="Mg_element : 005"  # scripted group (container) (typed FeaturePython)
  n = 1
  ref = Mg_element
FEATURE [App::DocumentObjectGroupPython] G4_Mg  # scripted group (container) (typed FeaturePython)
  Dunit = g/cm3
  Dvalue = 1.74
  Group = -> [Mg_element011]
  conduct = 2
  density = 1
  expand = 3
  formula = Mg
  name = G4_Mg
  specific = 4
FEATURE [App::DocumentObjectGroupPython] Al_element004  label="Al_element : 1"  # scripted group (container) (typed FeaturePython)
  n = 1
  ref = Al_element
FEATURE [App::DocumentObjectGroupPython] G4_Al  # scripted group (container) (typed FeaturePython)
  Dunit = g/cm3
  Dvalue = 2.699
  Group = -> [Al_element004]
  conduct = 2
  density = 1
  expand = 3
  formula = Al
  name = G4_Al
  specific = 4
FEATURE [App::DocumentObjectGroupPython] Si_element007  label="Si_element : 002"  # scripted group (container) (typed FeaturePython)
  n = 1
  ref = Si_element
FEATURE [App::DocumentObjectGroupPython] G4_Si  # scripted group (container) (typed FeaturePython)
  Dunit = g/cm3
  Dvalue = 2.33
  Group = -> [Si_element007]
  conduct = 2
  density = 1
  expand = 3
  formula = Si
  name = G4_Si
  specific = 4
FEATURE [App::DocumentObjectGroupPython] P_element013  label="P_element : 002"  # scripted group (container) (typed FeaturePython)
  n = 1
  ref = P_element
FEATURE [App::DocumentObjectGroupPython] G4_P  # scripted group (container) (typed FeaturePython)
  Dunit = g/cm3
  Dvalue = 2.2
  Group = -> [P_element013]
  conduct = 2
  density = 1
  expand = 3
  formula = P
  name = G4_P
  specific = 4
FEATURE [App::DocumentObjectGroupPython] S_element023  label="S_element : 007"  # scripted group (container) (typed FeaturePython)
  n = 1
  ref = S_element
FEATURE [App::DocumentObjectGroupPython] G4_S  # scripted group (container) (typed FeaturePython)
  Dunit = g/cm3
  Dvalue = 2
  Group = -> [S_element023]
  conduct = 2
  density = 1
  expand = 3
  formula = S
  name = G4_S
  specific = 4
FEATURE [App::DocumentObjectGroupPython] Cl_element029  label="Cl_element : 015"  # scripted group (container) (typed FeaturePython)
  n = 1
  ref = Cl_element
FEATURE [App::DocumentObjectGroupPython] G4_Cl  # scripted group (container) (typed FeaturePython)
  Dunit = g/cm3
  Dvalue = 0.00299473
  Group = -> [Cl_element029]
  conduct = 2
  density = 1
  expand = 3
  formula = Cl
  name = G4_Cl
  specific = 4
FEATURE [App::DocumentObjectGroupPython] Ar_element002  label="Ar_element : 1"  # scripted group (container) (typed FeaturePython)
  n = 1
  ref = Ar_element
FEATURE [App::DocumentObjectGroupPython] G4_Ar  # scripted group (container) (typed FeaturePython)
  Dunit = g/cm3
  Dvalue = 0.00166201
  Group = -> [Ar_element002]
  conduct = 2
  density = 1
  expand = 3
  formula = Ar
  name = G4_Ar
  specific = 4
FEATURE [App::DocumentObjectGroupPython] K_element013  label="K_element : 003"  # scripted group (container) (typed FeaturePython)
  n = 1
  ref = K_element
FEATURE [App::DocumentObjectGroupPython] G4_K  # scripted group (container) (typed FeaturePython)
  Dunit = g/cm3
  Dvalue = 0.862
  Group = -> [K_element013]
  conduct = 2
  density = 1
  expand = 3
  formula = K
  name = G4_K
  specific = 4
FEATURE [App::DocumentObjectGroupPython] Ca_element014  label="Ca_element : 007"  # scripted group (container) (typed FeaturePython)
  n = 1
  ref = Ca_element
FEATURE [App::DocumentObjectGroupPython] G4_Ca  # scripted group (container) (typed FeaturePython)
  Dunit = g/cm3
  Dvalue = 1.55
  Group = -> [Ca_element014]
  conduct = 2
  density = 1
  expand = 3
  formula = Ca
  name = G4_Ca
  specific = 4
FEATURE [App::DocumentObjectGroupPython] Sc_element001  label="Sc_element : 1"  # scripted group (container) (typed FeaturePython)
  n = 1
  ref = Sc_element
FEATURE [App::DocumentObjectGroupPython] G4_Sc  # scripted group (container) (typed FeaturePython)
  Dunit = g/cm3
  Dvalue = 2.989
  Group = -> [Sc_element001]
  conduct = 2
  density = 1
  expand = 3
  formula = Sc
  name = G4_Sc
  specific = 4
FEATURE [App::DocumentObjectGroupPython] Ti_element004  label="Ti_element : 002"  # scripted group (container) (typed FeaturePython)
  n = 1
  ref = Ti_element
FEATURE [App::DocumentObjectGroupPython] G4_Ti  # scripted group (container) (typed FeaturePython)
  Dunit = g/cm3
  Dvalue = 4.54
  Group = -> [Ti_element004]
  conduct = 2
  density = 1
  expand = 3
  formula = Ti
  name = G4_Ti
  specific = 4
FEATURE [App::DocumentObjectGroupPython] V_element001  label="V_element : 1"  # scripted group (container) (typed FeaturePython)
  n = 1
  ref = V_element
FEATURE [App::DocumentObjectGroupPython] G4_V  # scripted group (container) (typed FeaturePython)
  Dunit = g/cm3
  Dvalue = 6.11
  Group = -> [V_element001]
  conduct = 2
  density = 1
  expand = 3
  formula = V
  name = G4_V
  specific = 4
FEATURE [App::DocumentObjectGroupPython] Cr_element001  label="Cr_element : 1"  # scripted group (container) (typed FeaturePython)
  n = 1
  ref = Cr_element
FEATURE [App::DocumentObjectGroupPython] G4_Cr  # scripted group (container) (typed FeaturePython)
  Dunit = g/cm3
  Dvalue = 7.18
  Group = -> [Cr_element001]
  conduct = 2
  density = 1
  expand = 3
  formula = Cr
  name = G4_Cr
  specific = 4
FEATURE [App::DocumentObjectGroupPython] Mn_element001  label="Mn_element : 1"  # scripted group (container) (typed FeaturePython)
  n = 1
  ref = Mn_element
FEATURE [App::DocumentObjectGroupPython] G4_Mn  # scripted group (container) (typed FeaturePython)
  Dunit = g/cm3
  Dvalue = 7.44
  Group = -> [Mn_element001]
  conduct = 2
  density = 1
  expand = 3
  formula = Mn
  name = G4_Mn
  specific = 4
FEATURE [App::DocumentObjectGroupPython] Fe_element007  label="Fe_element : 004"  # scripted group (container) (typed FeaturePython)
  n = 1
  ref = Fe_element
FEATURE [App::DocumentObjectGroupPython] G4_Fe  # scripted group (container) (typed FeaturePython)
  Dunit = g/cm3
  Dvalue = 7.874
  Group = -> [Fe_element007]
  conduct = 2
  density = 1
  expand = 3
  formula = Fe
  name = G4_Fe
  specific = 4
FEATURE [App::DocumentObjectGroupPython] Co_element001  label="Co_element : 1"  # scripted group (container) (typed FeaturePython)
  n = 1
  ref = Co_element
FEATURE [App::DocumentObjectGroupPython] G4_Co  # scripted group (container) (typed FeaturePython)
  Dunit = g/cm3
  Dvalue = 8.9
  Group = -> [Co_element001]
  conduct = 2
  density = 1
  expand = 3
  formula = Co
  name = G4_Co
  specific = 4
FEATURE [App::DocumentObjectGroupPython] Ni_element001  label="Ni_element : 1"  # scripted group (container) (typed FeaturePython)
  n = 1
  ref = Ni_element
FEATURE [App::DocumentObjectGroupPython] G4_Ni  # scripted group (container) (typed FeaturePython)
  Dunit = g/cm3
  Dvalue = 8.902
  Group = -> [Ni_element001]
  conduct = 2
  density = 1
  expand = 3
  formula = Ni
  name = G4_Ni
  specific = 4
FEATURE [App::DocumentObjectGroupPython] Cu_element001  label="Cu_element : 1"  # scripted group (container) (typed FeaturePython)
  n = 1
  ref = Cu_element
FEATURE [App::DocumentObjectGroupPython] G4_Cu  # scripted group (container) (typed FeaturePython)
  Dunit = g/cm3
  Dvalue = 8.96
  Group = -> [Cu_element001]
  conduct = 2
  density = 1
  expand = 3
  formula = Cu
  name = G4_Cu
  specific = 4
FEATURE [App::DocumentObjectGroupPython] Zn_element001  label="Zn_element : 1"  # scripted group (container) (typed FeaturePython)
  n = 1
  ref = Zn_element
FEATURE [App::DocumentObjectGroupPython] G4_Zn  # scripted group (container) (typed FeaturePython)
  Dunit = g/cm3
  Dvalue = 7.133
  Group = -> [Zn_element001]
  conduct = 2
  density = 1
  expand = 3
  formula = Zn
  name = G4_Zn
  specific = 4
FEATURE [App::DocumentObjectGroupPython] Ga_element002  label="Ga_element : 002"  # scripted group (container) (typed FeaturePython)
  n = 1
  ref = Ga_element
FEATURE [App::DocumentObjectGroupPython] G4_Ga  # scripted group (container) (typed FeaturePython)
  Dunit = g/cm3
  Dvalue = 5.904
  Group = -> [Ga_element002]
  conduct = 2
  density = 1
  expand = 3
  formula = Ga
  name = G4_Ga
  specific = 4
FEATURE [App::DocumentObjectGroupPython] Ge_element002  label="Ge_element : 1"  # scripted group (container) (typed FeaturePython)
  n = 1
  ref = Ge_element
FEATURE [App::DocumentObjectGroupPython] G4_Ge  # scripted group (container) (typed FeaturePython)
  Dunit = g/cm3
  Dvalue = 5.323
  Group = -> [Ge_element002]
  conduct = 2
  density = 1
  expand = 3
  formula = Ge
  name = G4_Ge
  specific = 4
FEATURE [App::DocumentObjectGroupPython] As_element003  label="As_element : 002"  # scripted group (container) (typed FeaturePython)
  n = 1
  ref = As_element
FEATURE [App::DocumentObjectGroupPython] G4_As  # scripted group (container) (typed FeaturePython)
  Dunit = g/cm3
  Dvalue = 5.73
  Group = -> [As_element003]
  conduct = 2
  density = 1
  expand = 3
  formula = As
  name = G4_As
  specific = 4
FEATURE [App::DocumentObjectGroupPython] Se_element001  label="Se_element : 1"  # scripted group (container) (typed FeaturePython)
  n = 1
  ref = Se_element
FEATURE [App::DocumentObjectGroupPython] G4_Se  # scripted group (container) (typed FeaturePython)
  Dunit = g/cm3
  Dvalue = 4.5
  Group = -> [Se_element001]
  conduct = 2
  density = 1
  expand = 3
  formula = Se
  name = G4_Se
  specific = 4
FEATURE [App::DocumentObjectGroupPython] Br_element007  label="Br_element : 004"  # scripted group (container) (typed FeaturePython)
  n = 1
  ref = Br_element
FEATURE [App::DocumentObjectGroupPython] G4_Br  # scripted group (container) (typed FeaturePython)
  Dunit = g/cm3
  Dvalue = 0.0070721
  Group = -> [Br_element007]
  conduct = 2
  density = 1
  expand = 3
  formula = Br
  name = G4_Br
  specific = 4
FEATURE [App::DocumentObjectGroupPython] Kr_element001  label="Kr_element : 1"  # scripted group (container) (typed FeaturePython)
  n = 1
  ref = Kr_element
FEATURE [App::DocumentObjectGroupPython] G4_Kr  # scripted group (container) (typed FeaturePython)
  Dunit = g/cm3
  Dvalue = 0.00347832
  Group = -> [Kr_element001]
  conduct = 2
  density = 1
  expand = 3
  formula = Kr
  name = G4_Kr
  specific = 4
FEATURE [App::DocumentObjectGroupPython] Rb_element001  label="Rb_element : 1"  # scripted group (container) (typed FeaturePython)
  n = 1
  ref = Rb_element
FEATURE [App::DocumentObjectGroupPython] G4_Rb  # scripted group (container) (typed FeaturePython)
  Dunit = g/cm3
  Dvalue = 1.532
  Group = -> [Rb_element001]
  conduct = 2
  density = 1
  expand = 3
  formula = Rb
  name = G4_Rb
  specific = 4
FEATURE [App::DocumentObjectGroupPython] Sr_element001  label="Sr_element : 1"  # scripted group (container) (typed FeaturePython)
  n = 1
  ref = Sr_element
FEATURE [App::DocumentObjectGroupPython] G4_Sr  # scripted group (container) (typed FeaturePython)
  Dunit = g/cm3
  Dvalue = 2.54
  Group = -> [Sr_element001]
  conduct = 2
  density = 1
  expand = 3
  formula = Sr
  name = G4_Sr
  specific = 4
FEATURE [App::DocumentObjectGroupPython] Y_element001  label="Y_element : 1"  # scripted group (container) (typed FeaturePython)
  n = 1
  ref = Y_element
FEATURE [App::DocumentObjectGroupPython] G4_Y  # scripted group (container) (typed FeaturePython)
  Dunit = g/cm3
  Dvalue = 4.469
  Group = -> [Y_element001]
  conduct = 2
  density = 1
  expand = 3
  formula = Y
  name = G4_Y
  specific = 4
FEATURE [App::DocumentObjectGroupPython] Zr_element001  label="Zr_element : 1"  # scripted group (container) (typed FeaturePython)
  n = 1
  ref = Zr_element
FEATURE [App::DocumentObjectGroupPython] G4_Zr  # scripted group (container) (typed FeaturePython)
  Dunit = g/cm3
  Dvalue = 6.506
  Group = -> [Zr_element001]
  conduct = 2
  density = 1
  expand = 3
  formula = Zr
  name = G4_Zr
  specific = 4
FEATURE [App::DocumentObjectGroupPython] Nb_element001  label="Nb_element : 1"  # scripted group (container) (typed FeaturePython)
  n = 1
  ref = Nb_element
FEATURE [App::DocumentObjectGroupPython] G4_Nb  # scripted group (container) (typed FeaturePython)
  Dunit = g/cm3
  Dvalue = 8.57
  Group = -> [Nb_element001]
  conduct = 2
  density = 1
  expand = 3
  formula = Nb
  name = G4_Nb
  specific = 4
FEATURE [App::DocumentObjectGroupPython] Mo_element001  label="Mo_element : 1"  # scripted group (container) (typed FeaturePython)
  n = 1
  ref = Mo_element
FEATURE [App::DocumentObjectGroupPython] G4_Mo  # scripted group (container) (typed FeaturePython)
  Dunit = g/cm3
  Dvalue = 10.22
  Group = -> [Mo_element001]
  conduct = 2
  density = 1
  expand = 3
  formula = Mo
  name = G4_Mo
  specific = 4
FEATURE [App::DocumentObjectGroupPython] Tc_element001  label="Tc_element : 1"  # scripted group (container) (typed FeaturePython)
  n = 1
  ref = Tc_element
FEATURE [App::DocumentObjectGroupPython] G4_Tc  # scripted group (container) (typed FeaturePython)
  Dunit = g/cm3
  Dvalue = 11.5
  Group = -> [Tc_element001]
  conduct = 2
  density = 1
  expand = 3
  formula = Tc
  name = G4_Tc
  specific = 4
FEATURE [App::DocumentObjectGroupPython] Ru_element001  label="Ru_element : 1"  # scripted group (container) (typed FeaturePython)
  n = 1
  ref = Ru_element
FEATURE [App::DocumentObjectGroupPython] G4_Ru  # scripted group (container) (typed FeaturePython)
  Dunit = g/cm3
  Dvalue = 12.41
  Group = -> [Ru_element001]
  conduct = 2
  density = 1
  expand = 3
  formula = Ru
  name = G4_Ru
  specific = 4
FEATURE [App::DocumentObjectGroupPython] Rh_element001  label="Rh_element : 1"  # scripted group (container) (typed FeaturePython)
  n = 1
  ref = Rh_element
FEATURE [App::DocumentObjectGroupPython] G4_Rh  # scripted group (container) (typed FeaturePython)
  Dunit = g/cm3
  Dvalue = 12.41
  Group = -> [Rh_element001]
  conduct = 2
  density = 1
  expand = 3
  formula = Rh
  name = G4_Rh
  specific = 4
FEATURE [App::DocumentObjectGroupPython] Pd_element001  label="Pd_element : 1"  # scripted group (container) (typed FeaturePython)
  n = 1
  ref = Pd_element
FEATURE [App::DocumentObjectGroupPython] G4_Pd  # scripted group (container) (typed FeaturePython)
  Dunit = g/cm3
  Dvalue = 12.02
  Group = -> [Pd_element001]
  conduct = 2
  density = 1
  expand = 3
  formula = Pd
  name = G4_Pd
  specific = 4
FEATURE [App::DocumentObjectGroupPython] Ag_element006  label="Ag_element : 004"  # scripted group (container) (typed FeaturePython)
  n = 1
  ref = Ag_element
FEATURE [App::DocumentObjectGroupPython] G4_Ag  # scripted group (container) (typed FeaturePython)
  Dunit = g/cm3
  Dvalue = 10.5
  Group = -> [Ag_element006]
  conduct = 2
  density = 1
  expand = 3
  formula = Ag
  name = G4_Ag
  specific = 4
FEATURE [App::DocumentObjectGroupPython] Cd_element003  label="Cd_element : 003"  # scripted group (container) (typed FeaturePython)
  n = 1
  ref = Cd_element
FEATURE [App::DocumentObjectGroupPython] G4_Cd  # scripted group (container) (typed FeaturePython)
  Dunit = g/cm3
  Dvalue = 8.65
  Group = -> [Cd_element003]
  conduct = 2
  density = 1
  expand = 3
  formula = Cd
  name = G4_Cd
  specific = 4
FEATURE [App::DocumentObjectGroupPython] In_element001  label="In_element : 1"  # scripted group (container) (typed FeaturePython)
  n = 1
  ref = In_element
FEATURE [App::DocumentObjectGroupPython] G4_In  # scripted group (container) (typed FeaturePython)
  Dunit = g/cm3
  Dvalue = 7.31
  Group = -> [In_element001]
  conduct = 2
  density = 1
  expand = 3
  formula = In
  name = G4_In
  specific = 4
FEATURE [App::DocumentObjectGroupPython] Sn_element001  label="Sn_element : 1"  # scripted group (container) (typed FeaturePython)
  n = 1
  ref = Sn_element
FEATURE [App::DocumentObjectGroupPython] G4_Sn  # scripted group (container) (typed FeaturePython)
  Dunit = g/cm3
  Dvalue = 7.31
  Group = -> [Sn_element001]
  conduct = 2
  density = 1
  expand = 3
  formula = Sn
  name = G4_Sn
  specific = 4
FEATURE [App::DocumentObjectGroupPython] Sb_element001  label="Sb_element : 1"  # scripted group (container) (typed FeaturePython)
  n = 1
  ref = Sb_element
FEATURE [App::DocumentObjectGroupPython] G4_Sb  # scripted group (container) (typed FeaturePython)
  Dunit = g/cm3
  Dvalue = 6.691
  Group = -> [Sb_element001]
  conduct = 2
  density = 1
  expand = 3
  formula = Sb
  name = G4_Sb
  specific = 4
FEATURE [App::DocumentObjectGroupPython] Te_element002  label="Te_element : 002"  # scripted group (container) (typed FeaturePython)
  n = 1
  ref = Te_element
FEATURE [App::DocumentObjectGroupPython] G4_Te  # scripted group (container) (typed FeaturePython)
  Dunit = g/cm3
  Dvalue = 6.24
  Group = -> [Te_element002]
  conduct = 2
  density = 1
  expand = 3
  formula = Te
  name = G4_Te
  specific = 4
FEATURE [App::DocumentObjectGroupPython] I_element010  label="I_element : 006"  # scripted group (container) (typed FeaturePython)
  n = 1
  ref = I_element
FEATURE [App::DocumentObjectGroupPython] G4_I  # scripted group (container) (typed FeaturePython)
  Dunit = g/cm3
  Dvalue = 4.93
  Group = -> [I_element010]
  conduct = 2
  density = 1
  expand = 3
  formula = I
  name = G4_I
  specific = 4
FEATURE [App::DocumentObjectGroupPython] Xe_element001  label="Xe_element : 1"  # scripted group (container) (typed FeaturePython)
  n = 1
  ref = Xe_element
FEATURE [App::DocumentObjectGroupPython] G4_Xe  # scripted group (container) (typed FeaturePython)
  Dunit = g/cm3
  Dvalue = 0.00548536
  Group = -> [Xe_element001]
  conduct = 2
  density = 1
  expand = 3
  formula = Xe
  name = G4_Xe
  specific = 4
FEATURE [App::DocumentObjectGroupPython] Cs_element003  label="Cs_element : 003"  # scripted group (container) (typed FeaturePython)
  n = 1
  ref = Cs_element
FEATURE [App::DocumentObjectGroupPython] G4_Cs  # scripted group (container) (typed FeaturePython)
  Dunit = g/cm3
  Dvalue = 1.873
  Group = -> [Cs_element003]
  conduct = 2
  density = 1
  expand = 3
  formula = Cs
  name = G4_Cs
  specific = 4
FEATURE [App::DocumentObjectGroupPython] Ba_element003  label="Ba_element : 003"  # scripted group (container) (typed FeaturePython)
  n = 1
  ref = Ba_element
FEATURE [App::DocumentObjectGroupPython] G4_Ba  # scripted group (container) (typed FeaturePython)
  Dunit = g/cm3
  Dvalue = 3.5
  Group = -> [Ba_element003]
  conduct = 2
  density = 1
  expand = 3
  formula = Ba
  name = G4_Ba
  specific = 4
FEATURE [App::DocumentObjectGroupPython] La_element003  label="La_element : 003"  # scripted group (container) (typed FeaturePython)
  n = 1
  ref = La_element
FEATURE [App::DocumentObjectGroupPython] G4_La  # scripted group (container) (typed FeaturePython)
  Dunit = g/cm3
  Dvalue = 6.154
  Group = -> [La_element003]
  conduct = 2
  density = 1
  expand = 3
  formula = La
  name = G4_La
  specific = 4
FEATURE [App::DocumentObjectGroupPython] Ce_element002  label="Ce_element : 1"  # scripted group (container) (typed FeaturePython)
  n = 1
  ref = Ce_element
FEATURE [App::DocumentObjectGroupPython] G4_Ce  # scripted group (container) (typed FeaturePython)
  Dunit = g/cm3
  Dvalue = 6.657
  Group = -> [Ce_element002]
  conduct = 2
  density = 1
  expand = 3
  formula = Ce
  name = G4_Ce
  specific = 4
FEATURE [App::DocumentObjectGroupPython] Pr_element001  label="Pr_element : 1"  # scripted group (container) (typed FeaturePython)
  n = 1
  ref = Pr_element
FEATURE [App::DocumentObjectGroupPython] G4_Pr  # scripted group (container) (typed FeaturePython)
  Dunit = g/cm3
  Dvalue = 6.71
  Group = -> [Pr_element001]
  conduct = 2
  density = 1
  expand = 3
  formula = Pr
  name = G4_Pr
  specific = 4
FEATURE [App::DocumentObjectGroupPython] Nd_element001  label="Nd_element : 1"  # scripted group (container) (typed FeaturePython)
  n = 1
  ref = Nd_element
FEATURE [App::DocumentObjectGroupPython] G4_Nd  # scripted group (container) (typed FeaturePython)
  Dunit = g/cm3
  Dvalue = 6.9
  Group = -> [Nd_element001]
  conduct = 2
  density = 1
  expand = 3
  formula = Nd
  name = G4_Nd
  specific = 4
FEATURE [App::DocumentObjectGroupPython] Pm_element001  label="Pm_element : 1"  # scripted group (container) (typed FeaturePython)
  n = 1
  ref = Pm_element
FEATURE [App::DocumentObjectGroupPython] G4_Pm  # scripted group (container) (typed FeaturePython)
  Dunit = g/cm3
  Dvalue = 7.22
  Group = -> [Pm_element001]
  conduct = 2
  density = 1
  expand = 3
  formula = Pm
  name = G4_Pm
  specific = 4
FEATURE [App::DocumentObjectGroupPython] Sm_element001  label="Sm_element : 1"  # scripted group (container) (typed FeaturePython)
  n = 1
  ref = Sm_element
FEATURE [App::DocumentObjectGroupPython] G4_Sm  # scripted group (container) (typed FeaturePython)
  Dunit = g/cm3
  Dvalue = 7.46
  Group = -> [Sm_element001]
  conduct = 2
  density = 1
  expand = 3
  formula = Sm
  name = G4_Sm
  specific = 4
FEATURE [App::DocumentObjectGroupPython] Eu_element001  label="Eu_element : 1"  # scripted group (container) (typed FeaturePython)
  n = 1
  ref = Eu_element
FEATURE [App::DocumentObjectGroupPython] G4_Eu  # scripted group (container) (typed FeaturePython)
  Dunit = g/cm3
  Dvalue = 5.243
  Group = -> [Eu_element001]
  conduct = 2
  density = 1
  expand = 3
  formula = Eu
  name = G4_Eu
  specific = 4
FEATURE [App::DocumentObjectGroupPython] Gd_element002  label="Gd_element : 1"  # scripted group (container) (typed FeaturePython)
  n = 1
  ref = Gd_element
FEATURE [App::DocumentObjectGroupPython] G4_Gd  # scripted group (container) (typed FeaturePython)
  Dunit = g/cm3
  Dvalue = 7.9004
  Group = -> [Gd_element002]
  conduct = 2
  density = 1
  expand = 3
  formula = Gd
  name = G4_Gd
  specific = 4
FEATURE [App::DocumentObjectGroupPython] Tb_element001  label="Tb_element : 1"  # scripted group (container) (typed FeaturePython)
  n = 1
  ref = Tb_element
FEATURE [App::DocumentObjectGroupPython] G4_Tb  # scripted group (container) (typed FeaturePython)
  Dunit = g/cm3
  Dvalue = 8.229
  Group = -> [Tb_element001]
  conduct = 2
  density = 1
  expand = 3
  formula = Tb
  name = G4_Tb
  specific = 4
FEATURE [App::DocumentObjectGroupPython] Dy_element001  label="Dy_element : 1"  # scripted group (container) (typed FeaturePython)
  n = 1
  ref = Dy_element
FEATURE [App::DocumentObjectGroupPython] G4_Dy  # scripted group (container) (typed FeaturePython)
  Dunit = g/cm3
  Dvalue = 8.55
  Group = -> [Dy_element001]
  conduct = 2
  density = 1
  expand = 3
  formula = Dy
  name = G4_Dy
  specific = 4
FEATURE [App::DocumentObjectGroupPython] Ho_element001  label="Ho_element : 1"  # scripted group (container) (typed FeaturePython)
  n = 1
  ref = Ho_element
FEATURE [App::DocumentObjectGroupPython] G4_Ho  # scripted group (container) (typed FeaturePython)
  Dunit = g/cm3
  Dvalue = 8.795
  Group = -> [Ho_element001]
  conduct = 2
  density = 1
  expand = 3
  formula = Ho
  name = G4_Ho
  specific = 4
FEATURE [App::DocumentObjectGroupPython] Er_element001  label="Er_element : 1"  # scripted group (container) (typed FeaturePython)
  n = 1
  ref = Er_element
FEATURE [App::DocumentObjectGroupPython] G4_Er  # scripted group (container) (typed FeaturePython)
  Dunit = g/cm3
  Dvalue = 9.066
  Group = -> [Er_element001]
  conduct = 2
  density = 1
  expand = 3
  formula = Er
  name = G4_Er
  specific = 4
FEATURE [App::DocumentObjectGroupPython] Tm_element001  label="Tm_element : 1"  # scripted group (container) (typed FeaturePython)
  n = 1
  ref = Tm_element
FEATURE [App::DocumentObjectGroupPython] G4_Tm  # scripted group (container) (typed FeaturePython)
  Dunit = g/cm3
  Dvalue = 9.321
  Group = -> [Tm_element001]
  conduct = 2
  density = 1
  expand = 3
  formula = Tm
  name = G4_Tm
  specific = 4
FEATURE [App::DocumentObjectGroupPython] Yb_element001  label="Yb_element : 1"  # scripted group (container) (typed FeaturePython)
  n = 1
  ref = Yb_element
FEATURE [App::DocumentObjectGroupPython] G4_Yb  # scripted group (container) (typed FeaturePython)
  Dunit = g/cm3
  Dvalue = 6.73
  Group = -> [Yb_element001]
  conduct = 2
  density = 1
  expand = 3
  formula = Yb
  name = G4_Yb
  specific = 4
FEATURE [App::DocumentObjectGroupPython] Lu_element001  label="Lu_element : 1"  # scripted group (container) (typed FeaturePython)
  n = 1
  ref = Lu_element
FEATURE [App::DocumentObjectGroupPython] G4_Lu  # scripted group (container) (typed FeaturePython)
  Dunit = g/cm3
  Dvalue = 9.84
  Group = -> [Lu_element001]
  conduct = 2
  density = 1
  expand = 3
  formula = Lu
  name = G4_Lu
  specific = 4
FEATURE [App::DocumentObjectGroupPython] Hf_element001  label="Hf_element : 1"  # scripted group (container) (typed FeaturePython)
  n = 1
  ref = Hf_element
FEATURE [App::DocumentObjectGroupPython] G4_Hf  # scripted group (container) (typed FeaturePython)
  Dunit = g/cm3
  Dvalue = 13.31
  Group = -> [Hf_element001]
  conduct = 2
  density = 1
  expand = 3
  formula = Hf
  name = G4_Hf
  specific = 4
FEATURE [App::DocumentObjectGroupPython] Ta_element001  label="Ta_element : 1"  # scripted group (container) (typed FeaturePython)
  n = 1
  ref = Ta_element
FEATURE [App::DocumentObjectGroupPython] G4_Ta  # scripted group (container) (typed FeaturePython)
  Dunit = g/cm3
  Dvalue = 16.654
  Group = -> [Ta_element001]
  conduct = 2
  density = 1
  expand = 3
  formula = Ta
  name = G4_Ta
  specific = 4
FEATURE [App::DocumentObjectGroupPython] W_element004  label="W_element : 004"  # scripted group (container) (typed FeaturePython)
  n = 1
  ref = W_element
FEATURE [App::DocumentObjectGroupPython] G4_W  # scripted group (container) (typed FeaturePython)
  Dunit = g/cm3
  Dvalue = 19.3
  Group = -> [W_element004]
  conduct = 2
  density = 1
  expand = 3
  formula = W
  name = G4_W
  specific = 4
FEATURE [App::DocumentObjectGroupPython] Re_element001  label="Re_element : 1"  # scripted group (container) (typed FeaturePython)
  n = 1
  ref = Re_element
FEATURE [App::DocumentObjectGroupPython] G4_Re  # scripted group (container) (typed FeaturePython)
  Dunit = g/cm3
  Dvalue = 21.02
  Group = -> [Re_element001]
  conduct = 2
  density = 1
  expand = 3
  formula = Re
  name = G4_Re
  specific = 4
FEATURE [App::DocumentObjectGroupPython] Os_element001  label="Os_element : 1"  # scripted group (container) (typed FeaturePython)
  n = 1
  ref = Os_element
FEATURE [App::DocumentObjectGroupPython] G4_Os  # scripted group (container) (typed FeaturePython)
  Dunit = g/cm3
  Dvalue = 22.57
  Group = -> [Os_element001]
  conduct = 2
  density = 1
  expand = 3
  formula = Os
  name = G4_Os
  specific = 4
FEATURE [App::DocumentObjectGroupPython] Ir_element001  label="Ir_element : 1"  # scripted group (container) (typed FeaturePython)
  n = 1
  ref = Ir_element
FEATURE [App::DocumentObjectGroupPython] G4_Ir  # scripted group (container) (typed FeaturePython)
  Dunit = g/cm3
  Dvalue = 22.42
  Group = -> [Ir_element001]
  conduct = 2
  density = 1
  expand = 3
  formula = Ir
  name = G4_Ir
  specific = 4
FEATURE [App::DocumentObjectGroupPython] Pt_element001  label="Pt_element : 1"  # scripted group (container) (typed FeaturePython)
  n = 1
  ref = Pt_element
FEATURE [App::DocumentObjectGroupPython] G4_Pt  # scripted group (container) (typed FeaturePython)
  Dunit = g/cm3
  Dvalue = 21.45
  Group = -> [Pt_element001]
  conduct = 2
  density = 1
  expand = 3
  formula = Pt
  name = G4_Pt
  specific = 4
FEATURE [App::DocumentObjectGroupPython] Au_element001  label="Au_element : 1"  # scripted group (container) (typed FeaturePython)
  n = 1
  ref = Au_element
FEATURE [App::DocumentObjectGroupPython] G4_Au  # scripted group (container) (typed FeaturePython)
  Dunit = g/cm3
  Dvalue = 19.32
  Group = -> [Au_element001]
  conduct = 2
  density = 1
  expand = 3
  formula = Au
  name = G4_Au
  specific = 4
FEATURE [App::DocumentObjectGroupPython] Hg_element002  label="Hg_element : 002"  # scripted group (container) (typed FeaturePython)
  n = 1
  ref = Hg_element
FEATURE [App::DocumentObjectGroupPython] G4_Hg  # scripted group (container) (typed FeaturePython)
  Dunit = g/cm3
  Dvalue = 13.546
  Group = -> [Hg_element002]
  conduct = 2
  density = 1
  expand = 3
  formula = Hg
  name = G4_Hg
  specific = 4
FEATURE [App::DocumentObjectGroupPython] Tl_element002  label="Tl_element : 002"  # scripted group (container) (typed FeaturePython)
  n = 1
  ref = Tl_element
FEATURE [App::DocumentObjectGroupPython] G4_Tl  # scripted group (container) (typed FeaturePython)
  Dunit = g/cm3
  Dvalue = 11.72
  Group = -> [Tl_element002]
  conduct = 2
  density = 1
  expand = 3
  formula = Tl
  name = G4_Tl
  specific = 4
FEATURE [App::DocumentObjectGroupPython] Pb_element003  label="Pb_element : 1"  # scripted group (container) (typed FeaturePython)
  n = 1
  ref = Pb_element
FEATURE [App::DocumentObjectGroupPython] G4_Pb  # scripted group (container) (typed FeaturePython)
  Dunit = g/cm3
  Dvalue = 11.35
  Group = -> [Pb_element003]
  conduct = 2
  density = 1
  expand = 3
  formula = Pb
  name = G4_Pb
  specific = 4
FEATURE [App::DocumentObjectGroupPython] Bi_element002  label="Bi_element : 1"  # scripted group (container) (typed FeaturePython)
  n = 1
  ref = Bi_element
FEATURE [App::DocumentObjectGroupPython] G4_Bi  # scripted group (container) (typed FeaturePython)
  Dunit = g/cm3
  Dvalue = 9.747
  Group = -> [Bi_element002]
  conduct = 2
  density = 1
  expand = 3
  formula = Bi
  name = G4_Bi
  specific = 4
FEATURE [App::DocumentObjectGroupPython] Po_element001  label="Po_element : 1"  # scripted group (container) (typed FeaturePython)
  n = 1
  ref = Po_element
FEATURE [App::DocumentObjectGroupPython] G4_Po  # scripted group (container) (typed FeaturePython)
  Dunit = g/cm3
  Dvalue = 9.32
  Group = -> [Po_element001]
  conduct = 2
  density = 1
  expand = 3
  formula = Po
  name = G4_Po
  specific = 4
FEATURE [App::DocumentObjectGroupPython] At_element001  label="At_element : 1"  # scripted group (container) (typed FeaturePython)
  n = 1
  ref = At_element
FEATURE [App::DocumentObjectGroupPython] G4_At  # scripted group (container) (typed FeaturePython)
  Dunit = g/cm3
  Dvalue = 9.32
  Group = -> [At_element001]
  conduct = 2
  density = 1
  expand = 3
  formula = At
  name = G4_At
  specific = 4
FEATURE [App::DocumentObjectGroupPython] Rn_element001  label="Rn_element : 1"  # scripted group (container) (typed FeaturePython)
  n = 1
  ref = Rn_element
FEATURE [App::DocumentObjectGroupPython] G4_Rn  # scripted group (container) (typed FeaturePython)
  Dunit = g/cm3
  Dvalue = 0.00900662
  Group = -> [Rn_element001]
  conduct = 2
  density = 1
  expand = 3
  formula = Rn
  name = G4_Rn
  specific = 4
FEATURE [App::DocumentObjectGroupPython] Fr_element001  label="Fr_element : 1"  # scripted group (container) (typed FeaturePython)
  n = 1
  ref = Fr_element
FEATURE [App::DocumentObjectGroupPython] G4_Fr  # scripted group (container) (typed FeaturePython)
  Dunit = g/cm3
  Dvalue = 1
  Group = -> [Fr_element001]
  conduct = 2
  density = 1
  expand = 3
  formula = Fr
  name = G4_Fr
  specific = 4
FEATURE [App::DocumentObjectGroupPython] Ra_element001  label="Ra_element : 1"  # scripted group (container) (typed FeaturePython)
  n = 1
  ref = Ra_element
FEATURE [App::DocumentObjectGroupPython] G4_Ra  # scripted group (container) (typed FeaturePython)
  Dunit = g/cm3
  Dvalue = 5
  Group = -> [Ra_element001]
  conduct = 2
  density = 1
  expand = 3
  formula = Ra
  name = G4_Ra
  specific = 4
FEATURE [App::DocumentObjectGroupPython] Ac_element001  label="Ac_element : 1"  # scripted group (container) (typed FeaturePython)
  n = 1
  ref = Ac_element
FEATURE [App::DocumentObjectGroupPython] G4_Ac  # scripted group (container) (typed FeaturePython)
  Dunit = g/cm3
  Dvalue = 10.07
  Group = -> [Ac_element001]
  conduct = 2
  density = 1
  expand = 3
  formula = Ac
  name = G4_Ac
  specific = 4
FEATURE [App::DocumentObjectGroupPython] Th_element001  label="Th_element : 1"  # scripted group (container) (typed FeaturePython)
  n = 1
  ref = Th_element
FEATURE [App::DocumentObjectGroupPython] G4_Th  # scripted group (container) (typed FeaturePython)
  Dunit = g/cm3
  Dvalue = 11.72
  Group = -> [Th_element001]
  conduct = 2
  density = 1
  expand = 3
  formula = Th
  name = G4_Th
  specific = 4
FEATURE [App::DocumentObjectGroupPython] Pa_element001  label="Pa_element : 1"  # scripted group (container) (typed FeaturePython)
  n = 1
  ref = Pa_element
FEATURE [App::DocumentObjectGroupPython] G4_Pa  # scripted group (container) (typed FeaturePython)
  Dunit = g/cm3
  Dvalue = 15.37
  Group = -> [Pa_element001]
  conduct = 2
  density = 1
  expand = 3
  formula = Pa
  name = G4_Pa
  specific = 4
FEATURE [App::DocumentObjectGroupPython] U_element004  label="U_element : 004"  # scripted group (container) (typed FeaturePython)
  n = 1
  ref = U_element
FEATURE [App::DocumentObjectGroupPython] G4_U  # scripted group (container) (typed FeaturePython)
  Dunit = g/cm3
  Dvalue = 18.95
  Group = -> [U_element004]
  conduct = 2
  density = 1
  expand = 3
  formula = U
  name = G4_U
  specific = 4
FEATURE [App::DocumentObjectGroupPython] Np_element001  label="Np_element : 1"  # scripted group (container) (typed FeaturePython)
  n = 1
  ref = Np_element
FEATURE [App::DocumentObjectGroupPython] G4_Np  # scripted group (container) (typed FeaturePython)
  Dunit = g/cm3
  Dvalue = 20.25
  Group = -> [Np_element001]
  conduct = 2
  density = 1
  expand = 3
  formula = Np
  name = G4_Np
  specific = 4
FEATURE [App::DocumentObjectGroupPython] Pu_element002  label="Pu_element : 002"  # scripted group (container) (typed FeaturePython)
  n = 1
  ref = Pu_element
FEATURE [App::DocumentObjectGroupPython] G4_Pu  # scripted group (container) (typed FeaturePython)
  Dunit = g/cm3
  Dvalue = 19.84
  Group = -> [Pu_element002]
  conduct = 2
  density = 1
  expand = 3
  formula = Pu
  name = G4_Pu
  specific = 4
FEATURE [App::DocumentObjectGroupPython] Am_element001  label="Am_element : 1"  # scripted group (container) (typed FeaturePython)
  n = 1
  ref = Am_element
FEATURE [App::DocumentObjectGroupPython] G4_Am  # scripted group (container) (typed FeaturePython)
  Dunit = g/cm3
  Dvalue = 13.67
  Group = -> [Am_element001]
  conduct = 2
  density = 1
  expand = 3
  formula = Am
  name = G4_Am
  specific = 4
FEATURE [App::DocumentObjectGroupPython] Cm_element001  label="Cm_element : 1"  # scripted group (container) (typed FeaturePython)
  n = 1
  ref = Cm_element
FEATURE [App::DocumentObjectGroupPython] G4_Cm  # scripted group (container) (typed FeaturePython)
  Dunit = g/cm3
  Dvalue = 13.51
  Group = -> [Cm_element001]
  conduct = 2
  density = 1
  expand = 3
  formula = Cm
  name = G4_Cm
  specific = 4
FEATURE [App::DocumentObjectGroupPython] Bk_element001  label="Bk_element : 1"  # scripted group (container) (typed FeaturePython)
  n = 1
  ref = Bk_element
FEATURE [App::DocumentObjectGroupPython] G4_Bk  # scripted group (container) (typed FeaturePython)
  Dunit = g/cm3
  Dvalue = 14
  Group = -> [Bk_element001]
  conduct = 2
  density = 1
  expand = 3
  formula = Bk
  name = G4_Bk
  specific = 4
FEATURE [App::DocumentObjectGroupPython] Cf_element001  label="Cf_element : 1"  # scripted group (container) (typed FeaturePython)
  n = 1
  ref = Cf_element
FEATURE [App::DocumentObjectGroupPython] G4_Cf  # scripted group (container) (typed FeaturePython)
  Dunit = g/cm3
  Dvalue = 10
  Group = -> [Cf_element001]
  conduct = 2
  density = 1
  expand = 3
  formula = Cf
  name = G4_Cf
  specific = 4
FEATURE [App::DocumentObjectGroupPython] Element  # scripted group (container) (typed FeaturePython)
  Group = -> [G4_H,G4_He,G4_Li,G4_Be,G4_B,G4_C,G4_N,G4_O,G4_F,G4_Ne,G4_Na,G4_Mg,G4_Al,G4_Si,G4_P,G4_S,G4_Cl,G4_Ar,G4_K,G4_Ca,G4_Sc,G4_Ti,G4_V,G4_Cr,G4_Mn,G4_Fe,G4_Co,G4_Ni,G4_Cu,G4_Zn,G4_Ga,G4_Ge,G4_As,G4_Se,G4_Br,G4_Kr,G4_Rb,G4_Sr,G4_Y,G4_Zr,G4_Nb,G4_Mo,G4_Tc,G4_Ru,G4_Rh,G4_Pd,G4_Ag,G4_Cd,G4_In,G4_Sn,G4_Sb,G4_Te,G4_I,G4_Xe,G4_Cs,G4_Ba,G4_La,G4_Ce,G4_Pr,G4_Nd,G4_Pm,G4_Sm,G4_Eu,G4_Gd,G4_Tb,G4_Dy,G4_Ho,G4_Er,+30 more]
FEATURE [App::DocumentObjectGroupPython] H_element114  label="H_element : 063"  # scripted group (container) (typed FeaturePython)
  n = 2
  ref = H_element
FEATURE [App::DocumentObjectGroupPython] G4_lH2  # scripted group (container) (typed FeaturePython)
  Dunit = g/cm3
  Dvalue = 0.0708
  Group = -> [H_element114]
  conduct = 2
  density = 1
  expand = 3
  formula = G4_lH2
  name = G4_lH2
  specific = 4
FEATURE [App::DocumentObjectGroupPython] N_element049  label="N_element : 022"  # scripted group (container) (typed FeaturePython)
  n = 2
  ref = N_element
FEATURE [App::DocumentObjectGroupPython] G4_lN2  # scripted group (container) (typed FeaturePython)
  Dunit = g/cm3
  Dvalue = 0.807
  Group = -> [N_element049]
  conduct = 2
  density = 1
  expand = 3
  formula = G4_lN2
  name = G4_lN2
  specific = 4
FEATURE [App::DocumentObjectGroupPython] O_element106  label="O_element : 060"  # scripted group (container) (typed FeaturePython)
  n = 2
  ref = O_element
FEATURE [App::DocumentObjectGroupPython] G4_lO2  # scripted group (container) (typed FeaturePython)
  Dunit = g/cm3
  Dvalue = 1.141
  Group = -> [O_element106]
  conduct = 2
  density = 1
  expand = 3
  formula = G4_lO2
  name = G4_lO2
  specific = 4
FEATURE [App::DocumentObjectGroupPython] Ar  label="Ar : 1"  # scripted group (container) (typed FeaturePython)
  n = 1
  ref = Ar
FEATURE [App::DocumentObjectGroupPython] G4_lAr  # scripted group (container) (typed FeaturePython)
  Dunit = g/cm3
  Dvalue = 1.396
  Group = -> [Ar]
  conduct = 2
  density = 1
  expand = 3
  formula = G4_lAr
  name = G4_lAr
  specific = 4
FEATURE [App::DocumentObjectGroupPython] Br  label="Br : 1"  # scripted group (container) (typed FeaturePython)
  n = 1
  ref = Br
FEATURE [App::DocumentObjectGroupPython] G4_lBr  # scripted group (container) (typed FeaturePython)
  Dunit = g/cm3
  Dvalue = 3.1028
  Group = -> [Br]
  conduct = 2
  density = 1
  expand = 3
  formula = G4_lBr
  name = G4_lBr
  specific = 4
FEATURE [App::DocumentObjectGroupPython] Kr  label="Kr : 1"  # scripted group (container) (typed FeaturePython)
  n = 1
  ref = Kr
FEATURE [App::DocumentObjectGroupPython] G4_lKr  # scripted group (container) (typed FeaturePython)
  Dunit = g/cm3
  Dvalue = 2.418
  Group = -> [Kr]
  conduct = 2
  density = 1
  expand = 3
  formula = G4_lKr
  name = G4_lKr
  specific = 4
FEATURE [App::DocumentObjectGroupPython] Xe  label="Xe : 1"  # scripted group (container) (typed FeaturePython)
  n = 1
  ref = Xe
FEATURE [App::DocumentObjectGroupPython] G4_lXe  # scripted group (container) (typed FeaturePython)
  Dunit = g/cm3
  Dvalue = 2.953
  Group = -> [Xe]
  conduct = 2
  density = 1
  expand = 3
  formula = G4_lXe
  name = G4_lXe
  specific = 4
FEATURE [App::DocumentObjectGroupPython] O_element107  label="O_element : 061"  # scripted group (container) (typed FeaturePython)
  n = 4
  ref = O_element
FEATURE [App::DocumentObjectGroupPython] Pb_element004  label="Pb_element : 002"  # scripted group (container) (typed FeaturePython)
  n = 1
  ref = Pb_element
FEATURE [App::DocumentObjectGroupPython] W_element005  label="W_element : 005"  # scripted group (container) (typed FeaturePython)
  n = 1
  ref = W_element
FEATURE [App::DocumentObjectGroupPython] G4_PbWO4  # scripted group (container) (typed FeaturePython)
  Dunit = g/cm3
  Dvalue = 8.28
  Group = -> [O_element107,Pb_element004,W_element005]
  conduct = 2
  density = 1
  expand = 3
  formula = G4_PbWO4
  name = G4_PbWO4
  specific = 4
FEATURE [App::DocumentObjectGroupPython] alactic  label="alactic : 1"  # scripted group (container) (typed FeaturePython)
  n = 1
  ref = alactic
FEATURE [App::DocumentObjectGroupPython] G4_Galactic  # scripted group (container) (typed FeaturePython)
  Dunit = g/cm3
  Dvalue = 0
  Group = -> [alactic]
  conduct = 2
  density = 1
  expand = 3
  formula = G4_Galactic
  name = G4_Galactic
  specific = 4
FEATURE [App::DocumentObjectGroupPython] RAPHITE_POROUS  label="RAPHITE_POROUS : 1"  # scripted group (container) (typed FeaturePython)
  n = 1
  ref = RAPHITE_POROUS
FEATURE [App::DocumentObjectGroupPython] G4_GRAPHITE_POROUS  # scripted group (container) (typed FeaturePython)
  Dunit = g/cm3
  Dvalue = 1.7
  Group = -> [RAPHITE_POROUS]
  conduct = 2
  density = 1
  expand = 3
  formula = G4_GRAPHITE_POROUS
  name = G4_GRAPHITE_POROUS
  specific = 4
FEATURE [App::DocumentObjectGroupPython] H_element115  label="H_element : 0.150"  # scripted group (container) (typed FeaturePython)
  n = 0.080538
FEATURE [App::DocumentObjectGroupPython] C_element125  label="C_element : 0.600"  # scripted group (container) (typed FeaturePython)
  n = 0.599848
FEATURE [App::DocumentObjectGroupPython] O_element108  label="O_element : 0.320"  # scripted group (container) (typed FeaturePython)
  n = 0.319614
FEATURE [App::DocumentObjectGroupPython] G4_LUCITE  # scripted group (container) (typed FeaturePython)
  Dunit = g/cm3
  Dvalue = 1.19
  Group = -> [H_element115,C_element125,O_element108]
  conduct = 2
  density = 1
  expand = 3
  formula = G4_LUCITE
  name = G4_LUCITE
  specific = 4
FEATURE [App::DocumentObjectGroupPython] Cu_element002  label="Cu_element : 62"  # scripted group (container) (typed FeaturePython)
  n = 62
  ref = Cu_element
FEATURE [App::DocumentObjectGroupPython] Zn_element002  label="Zn_element : 35"  # scripted group (container) (typed FeaturePython)
  n = 35
  ref = Zn_element
FEATURE [App::DocumentObjectGroupPython] Pb_element005  label="Pb_element : 3"  # scripted group (container) (typed FeaturePython)
  n = 3
  ref = Pb_element
FEATURE [App::DocumentObjectGroupPython] G4_BRASS  # scripted group (container) (typed FeaturePython)
  Dunit = g/cm3
  Dvalue = 8.52
  Group = -> [Cu_element002,Zn_element002,Pb_element005]
  conduct = 2
  density = 1
  expand = 3
  formula = G4_BRASS
  name = G4_BRASS
  specific = 4
FEATURE [App::DocumentObjectGroupPython] Cu_element003  label="Cu_element : 89"  # scripted group (container) (typed FeaturePython)
  n = 89
  ref = Cu_element
FEATURE [App::DocumentObjectGroupPython] Zn_element003  label="Zn_element : 9"  # scripted group (container) (typed FeaturePython)
  n = 9
  ref = Zn_element
FEATURE [App::DocumentObjectGroupPython] Pb_element006  label="Pb_element : 2"  # scripted group (container) (typed FeaturePython)
  n = 2
  ref = Pb_element
FEATURE [App::DocumentObjectGroupPython] G4_BRONZE  # scripted group (container) (typed FeaturePython)
  Dunit = g/cm3
  Dvalue = 8.82
  Group = -> [Cu_element003,Zn_element003,Pb_element006]
  conduct = 2
  density = 1
  expand = 3
  formula = G4_BRONZE
  name = G4_BRONZE
  specific = 4
FEATURE [App::DocumentObjectGroupPython] Fe_element008  label="Fe_element : 74"  # scripted group (container) (typed FeaturePython)
  n = 74
  ref = Fe_element
FEATURE [App::DocumentObjectGroupPython] Cr_element002  label="Cr_element : 18"  # scripted group (container) (typed FeaturePython)
  n = 18
  ref = Cr_element
FEATURE [App::DocumentObjectGroupPython] Ni_element002  label="Ni_element : 8"  # scripted group (container) (typed FeaturePython)
  n = 8
  ref = Ni_element
FEATURE [App::DocumentObjectGroupPython] G4_STAINLESS_STEEL  label="G4_STAINLESS-STEEL"  # scripted group (container) (typed FeaturePython)
  Dunit = g/cm3
  Dvalue = 8
  Group = -> [Fe_element008,Cr_element002,Ni_element002]
  conduct = 2
  density = 1
  expand = 3
  formula = G4_STAINLESS-STEEL
  name = G4_STAINLESS-STEEL
  specific = 4
FEATURE [App::DocumentObjectGroupPython] H_element116  label="H_element : 064"  # scripted group (container) (typed FeaturePython)
  n = 18
  ref = H_element
FEATURE [App::DocumentObjectGroupPython] C_element126  label="C_element : 071"  # scripted group (container) (typed FeaturePython)
  n = 12
  ref = C_element
FEATURE [App::DocumentObjectGroupPython] O_element109  label="O_element : 062"  # scripted group (container) (typed FeaturePython)
  n = 7
  ref = O_element
FEATURE [App::DocumentObjectGroupPython] G4_CR39  # scripted group (container) (typed FeaturePython)
  Dunit = g/cm3
  Dvalue = 1.32
  Group = -> [H_element116,C_element126,O_element109]
  conduct = 2
  density = 1
  expand = 3
  formula = G4_CR39
  name = G4_CR39
  specific = 4
FEATURE [App::DocumentObjectGroupPython] H_element117  label="H_element : 38"  # scripted group (container) (typed FeaturePython)
  n = 38
  ref = H_element
FEATURE [App::DocumentObjectGroupPython] C_element127  label="C_element : 072"  # scripted group (container) (typed FeaturePython)
  n = 18
  ref = C_element
FEATURE [App::DocumentObjectGroupPython] O_element110  label="O_element : 063"  # scripted group (container) (typed FeaturePython)
  n = 1
  ref = O_element
FEATURE [App::DocumentObjectGroupPython] G4_OCTADECANOL  # scripted group (container) (typed FeaturePython)
  Dunit = g/cm3
  Dvalue = 0.812
  Group = -> [H_element117,C_element127,O_element110]
  conduct = 2
  density = 1
  expand = 3
  formula = G4_OCTADECANOL
  name = G4_OCTADECANOL
  specific = 4
FEATURE [App::DocumentObjectGroupPython] HEP  # scripted group (container) (typed FeaturePython)
  Group = -> [G4_lH2,G4_lN2,G4_lO2,G4_lAr,G4_lBr,G4_lKr,G4_lXe,G4_PbWO4,G4_Galactic,G4_GRAPHITE_POROUS,G4_LUCITE,G4_BRASS,G4_BRONZE,G4_STAINLESS_STEEL,G4_CR39,G4_OCTADECANOL]
FEATURE [App::DocumentObjectGroupPython] C_element128  label="C_element : 073"  # scripted group (container) (typed FeaturePython)
  n = 14
  ref = C_element
FEATURE [App::DocumentObjectGroupPython] H_element118  label="H_element : 065"  # scripted group (container) (typed FeaturePython)
  n = 10
  ref = H_element
FEATURE [App::DocumentObjectGroupPython] O_element111  label="O_element : 064"  # scripted group (container) (typed FeaturePython)
  n = 2
  ref = O_element
FEATURE [App::DocumentObjectGroupPython] N_element050  label="N_element : 023"  # scripted group (container) (typed FeaturePython)
  n = 2
  ref = N_element
FEATURE [App::DocumentObjectGroupPython] G4_KEVLAR  # scripted group (container) (typed FeaturePython)
  Dunit = g/cm3
  Dvalue = 1.44
  Group = -> [C_element128,H_element118,O_element111,N_element050]
  conduct = 2
  density = 1
  expand = 3
  formula = G4_KEVLAR
  name = G4_KEVLAR
  specific = 4
FEATURE [App::DocumentObjectGroupPython] C_element129  label="C_element : 074"  # scripted group (container) (typed FeaturePython)
  n = 10
  ref = C_element
FEATURE [App::DocumentObjectGroupPython] H_element119  label="H_element : 066"  # scripted group (container) (typed FeaturePython)
  n = 8
  ref = H_element
FEATURE [App::DocumentObjectGroupPython] O_element112  label="O_element : 065"  # scripted group (container) (typed FeaturePython)
  n = 4
  ref = O_element
FEATURE [App::DocumentObjectGroupPython] G4_DACRON  # scripted group (container) (typed FeaturePython)
  Dunit = g/cm3
  Dvalue = 1.4
  Group = -> [C_element129,H_element119,O_element112]
  conduct = 2
  density = 1
  expand = 3
  formula = G4_DACRON
  name = G4_DACRON
  specific = 4
FEATURE [App::DocumentObjectGroupPython] C_element130  label="C_element : 075"  # scripted group (container) (typed FeaturePython)
  n = 4
  ref = C_element
FEATURE [App::DocumentObjectGroupPython] H_element120  label="H_element : 067"  # scripted group (container) (typed FeaturePython)
  n = 5
  ref = H_element
FEATURE [App::DocumentObjectGroupPython] Cl_element030  label="Cl_element : 016"  # scripted group (container) (typed FeaturePython)
  n = 1
  ref = Cl_element
FEATURE [App::DocumentObjectGroupPython] G4_NEOPRENE  # scripted group (container) (typed FeaturePython)
  Dunit = g/cm3
  Dvalue = 1.23
  Group = -> [C_element130,H_element120,Cl_element030]
  conduct = 2
  density = 1
  expand = 3
  formula = G4_NEOPRENE
  name = G4_NEOPRENE
  specific = 4
FEATURE [App::DocumentObjectGroupPython] Space  # scripted group (container) (typed FeaturePython)
  Group = -> [G4_KEVLAR,G4_DACRON,G4_NEOPRENE]
FEATURE [App::DocumentObjectGroupPython] H_element121  label="H_element : 068"  # scripted group (container) (typed FeaturePython)
  n = 5
  ref = H_element
FEATURE [App::DocumentObjectGroupPython] C_element131  label="C_element : 076"  # scripted group (container) (typed FeaturePython)
  n = 4
  ref = C_element
FEATURE [App::DocumentObjectGroupPython] N_element051  label="N_element : 3"  # scripted group (container) (typed FeaturePython)
  n = 3
  ref = N_element
FEATURE [App::DocumentObjectGroupPython] O_element113  label="O_element : 066"  # scripted group (container) (typed FeaturePython)
  n = 1
  ref = O_element
FEATURE [App::DocumentObjectGroupPython] G4_CYTOSINE  # scripted group (container) (typed FeaturePython)
  Dunit = g/cm3
  Dvalue = 1.55
  Group = -> [H_element121,C_element131,N_element051,O_element113]
  conduct = 2
  density = 1
  expand = 3
  formula = G4_CYTOSINE
  name = G4_CYTOSINE
  specific = 4
FEATURE [App::DocumentObjectGroupPython] H_element122  label="H_element : 069"  # scripted group (container) (typed FeaturePython)
  n = 6
  ref = H_element
FEATURE [App::DocumentObjectGroupPython] C_element132  label="C_element : 077"  # scripted group (container) (typed FeaturePython)
  n = 5
  ref = C_element
FEATURE [App::DocumentObjectGroupPython] N_element052  label="N_element : 024"  # scripted group (container) (typed FeaturePython)
  n = 2
  ref = N_element
FEATURE [App::DocumentObjectGroupPython] O_element114  label="O_element : 067"  # scripted group (container) (typed FeaturePython)
  n = 2
  ref = O_element
FEATURE [App::DocumentObjectGroupPython] G4_THYMINE  # scripted group (container) (typed FeaturePython)
  Dunit = g/cm3
  Dvalue = 1.23
  Group = -> [H_element122,C_element132,N_element052,O_element114]
  conduct = 2
  density = 1
  expand = 3
  formula = G4_THYMINE
  name = G4_THYMINE
  specific = 4
FEATURE [App::DocumentObjectGroupPython] H_element123  label="H_element : 070"  # scripted group (container) (typed FeaturePython)
  n = 4
  ref = H_element
FEATURE [App::DocumentObjectGroupPython] C_element133  label="C_element : 078"  # scripted group (container) (typed FeaturePython)
  n = 4
  ref = C_element
FEATURE [App::DocumentObjectGroupPython] N_element053  label="N_element : 025"  # scripted group (container) (typed FeaturePython)
  n = 2
  ref = N_element
FEATURE [App::DocumentObjectGroupPython] O_element115  label="O_element : 068"  # scripted group (container) (typed FeaturePython)
  n = 2
  ref = O_element
FEATURE [App::DocumentObjectGroupPython] G4_URACIL  # scripted group (container) (typed FeaturePython)
  Dunit = g/cm3
  Dvalue = 1.32
  Group = -> [H_element123,C_element133,N_element053,O_element115]
  conduct = 2
  density = 1
  expand = 3
  formula = G4_URACIL
  name = G4_URACIL
  specific = 4
FEATURE [App::DocumentObjectGroupPython] H_element124  label="H_element : 071"  # scripted group (container) (typed FeaturePython)
  n = 4
  ref = H_element
FEATURE [App::DocumentObjectGroupPython] C_element134  label="C_element : 079"  # scripted group (container) (typed FeaturePython)
  n = 5
  ref = C_element
FEATURE [App::DocumentObjectGroupPython] N_element054  label="N_element : 026"  # scripted group (container) (typed FeaturePython)
  n = 5
  ref = N_element
FEATURE [App::DocumentObjectGroupPython] G4_DNA_ADENINE  # scripted group (container) (typed FeaturePython)
  Dunit = g/cm3
  Dvalue = 1
  Group = -> [H_element124,C_element134,N_element054]
  conduct = 2
  density = 1
  expand = 3
  formula = G4_DNA_ADENINE
  name = G4_DNA_ADENINE
  specific = 4
FEATURE [App::DocumentObjectGroupPython] H_element125  label="H_element : 072"  # scripted group (container) (typed FeaturePython)
  n = 4
  ref = H_element
FEATURE [App::DocumentObjectGroupPython] C_element135  label="C_element : 080"  # scripted group (container) (typed FeaturePython)
  n = 5
  ref = C_element
FEATURE [App::DocumentObjectGroupPython] N_element055  label="N_element : 027"  # scripted group (container) (typed FeaturePython)
  n = 5
  ref = N_element
FEATURE [App::DocumentObjectGroupPython] O_element116  label="O_element : 069"  # scripted group (container) (typed FeaturePython)
  n = 1
  ref = O_element
FEATURE [App::DocumentObjectGroupPython] G4_DNA_GUANINE  # scripted group (container) (typed FeaturePython)
  Dunit = g/cm3
  Dvalue = 1
  Group = -> [H_element125,C_element135,N_element055,O_element116]
  conduct = 2
  density = 1
  expand = 3
  formula = G4_DNA_GUANINE
  name = G4_DNA_GUANINE
  specific = 4
FEATURE [App::DocumentObjectGroupPython] H_element126  label="H_element : 073"  # scripted group (container) (typed FeaturePython)
  n = 4
  ref = H_element
FEATURE [App::DocumentObjectGroupPython] C_element136  label="C_element : 081"  # scripted group (container) (typed FeaturePython)
  n = 4
  ref = C_element
FEATURE [App::DocumentObjectGroupPython] N_element056  label="N_element : 028"  # scripted group (container) (typed FeaturePython)
  n = 3
  ref = N_element
FEATURE [App::DocumentObjectGroupPython] O_element117  label="O_element : 070"  # scripted group (container) (typed FeaturePython)
  n = 1
  ref = O_element
FEATURE [App::DocumentObjectGroupPython] G4_DNA_CYTOSINE  # scripted group (container) (typed FeaturePython)
  Dunit = g/cm3
  Dvalue = 1
  Group = -> [H_element126,C_element136,N_element056,O_element117]
  conduct = 2
  density = 1
  expand = 3
  formula = G4_DNA_CYTOSINE
  name = G4_DNA_CYTOSINE
  specific = 4
FEATURE [App::DocumentObjectGroupPython] H_element127  label="H_element : 074"  # scripted group (container) (typed FeaturePython)
  n = 5
  ref = H_element
FEATURE [App::DocumentObjectGroupPython] C_element137  label="C_element : 082"  # scripted group (container) (typed FeaturePython)
  n = 5
  ref = C_element
FEATURE [App::DocumentObjectGroupPython] N_element057  label="N_element : 029"  # scripted group (container) (typed FeaturePython)
  n = 2
  ref = N_element
FEATURE [App::DocumentObjectGroupPython] O_element118  label="O_element : 071"  # scripted group (container) (typed FeaturePython)
  n = 2
  ref = O_element
FEATURE [App::DocumentObjectGroupPython] G4_DNA_THYMINE  # scripted group (container) (typed FeaturePython)
  Dunit = g/cm3
  Dvalue = 1
  Group = -> [H_element127,C_element137,N_element057,O_element118]
  conduct = 2
  density = 1
  expand = 3
  formula = G4_DNA_THYMINE
  name = G4_DNA_THYMINE
  specific = 4
FEATURE [App::DocumentObjectGroupPython] H_element128  label="H_element : 075"  # scripted group (container) (typed FeaturePython)
  n = 3
  ref = H_element
FEATURE [App::DocumentObjectGroupPython] C_element138  label="C_element : 083"  # scripted group (container) (typed FeaturePython)
  n = 4
  ref = C_element
FEATURE [App::DocumentObjectGroupPython] N_element058  label="N_element : 030"  # scripted group (container) (typed FeaturePython)
  n = 2
  ref = N_element
FEATURE [App::DocumentObjectGroupPython] O_element119  label="O_element : 072"  # scripted group (container) (typed FeaturePython)
  n = 2
  ref = O_element
FEATURE [App::DocumentObjectGroupPython] G4_DNA_URACIL  # scripted group (container) (typed FeaturePython)
  Dunit = g/cm3
  Dvalue = 1
  Group = -> [H_element128,C_element138,N_element058,O_element119]
  conduct = 2
  density = 1
  expand = 3
  formula = G4_DNA_URACIL
  name = G4_DNA_URACIL
  specific = 4
FEATURE [App::DocumentObjectGroupPython] H_element129  label="H_element : 076"  # scripted group (container) (typed FeaturePython)
  n = 10
  ref = H_element
FEATURE [App::DocumentObjectGroupPython] C_element139  label="C_element : 084"  # scripted group (container) (typed FeaturePython)
  n = 10
  ref = C_element
FEATURE [App::DocumentObjectGroupPython] N_element059  label="N_element : 031"  # scripted group (container) (typed FeaturePython)
  n = 5
  ref = N_element
FEATURE [App::DocumentObjectGroupPython] O_element120  label="O_element : 073"  # scripted group (container) (typed FeaturePython)
  n = 4
  ref = O_element
FEATURE [App::DocumentObjectGroupPython] G4_DNA_ADENOSINE  # scripted group (container) (typed FeaturePython)
  Dunit = g/cm3
  Dvalue = 1
  Group = -> [H_element129,C_element139,N_element059,O_element120]
  conduct = 2
  density = 1
  expand = 3
  formula = G4_DNA_ADENOSINE
  name = G4_DNA_ADENOSINE
  specific = 4
FEATURE [App::DocumentObjectGroupPython] H_element130  label="H_element : 077"  # scripted group (container) (typed FeaturePython)
  n = 10
  ref = H_element
FEATURE [App::DocumentObjectGroupPython] C_element140  label="C_element : 085"  # scripted group (container) (typed FeaturePython)
  n = 10
  ref = C_element
FEATURE [App::DocumentObjectGroupPython] N_element060  label="N_element : 032"  # scripted group (container) (typed FeaturePython)
  n = 5
  ref = N_element
FEATURE [App::DocumentObjectGroupPython] O_element121  label="O_element : 074"  # scripted group (container) (typed FeaturePython)
  n = 5
  ref = O_element
FEATURE [App::DocumentObjectGroupPython] G4_DNA_GUANOSINE  # scripted group (container) (typed FeaturePython)
  Dunit = g/cm3
  Dvalue = 1
  Group = -> [H_element130,C_element140,N_element060,O_element121]
  conduct = 2
  density = 1
  expand = 3
  formula = G4_DNA_GUANOSINE
  name = G4_DNA_GUANOSINE
  specific = 4
FEATURE [App::DocumentObjectGroupPython] H_element131  label="H_element : 078"  # scripted group (container) (typed FeaturePython)
  n = 10
  ref = H_element
FEATURE [App::DocumentObjectGroupPython] C_element141  label="C_element : 086"  # scripted group (container) (typed FeaturePython)
  n = 9
  ref = C_element
FEATURE [App::DocumentObjectGroupPython] N_element061  label="N_element : 033"  # scripted group (container) (typed FeaturePython)
  n = 3
  ref = N_element
FEATURE [App::DocumentObjectGroupPython] O_element122  label="O_element : 075"  # scripted group (container) (typed FeaturePython)
  n = 5
  ref = O_element
FEATURE [App::DocumentObjectGroupPython] G4_DNA_CYTIDINE  # scripted group (container) (typed FeaturePython)
  Dunit = g/cm3
  Dvalue = 1
  Group = -> [H_element131,C_element141,N_element061,O_element122]
  conduct = 2
  density = 1
  expand = 3
  formula = G4_DNA_CYTIDINE
  name = G4_DNA_CYTIDINE
  specific = 4
FEATURE [App::DocumentObjectGroupPython] H_element132  label="H_element : 079"  # scripted group (container) (typed FeaturePython)
  n = 9
  ref = H_element
FEATURE [App::DocumentObjectGroupPython] C_element142  label="C_element : 087"  # scripted group (container) (typed FeaturePython)
  n = 9
  ref = C_element
FEATURE [App::DocumentObjectGroupPython] N_element062  label="N_element : 034"  # scripted group (container) (typed FeaturePython)
  n = 2
  ref = N_element
FEATURE [App::DocumentObjectGroupPython] O_element123  label="O_element : 076"  # scripted group (container) (typed FeaturePython)
  n = 6
  ref = O_element
FEATURE [App::DocumentObjectGroupPython] G4_DNA_URIDINE  # scripted group (container) (typed FeaturePython)
  Dunit = g/cm3
  Dvalue = 1
  Group = -> [H_element132,C_element142,N_element062,O_element123]
  conduct = 2
  density = 1
  expand = 3
  formula = G4_DNA_URIDINE
  name = G4_DNA_URIDINE
  specific = 4
FEATURE [App::DocumentObjectGroupPython] H_element133  label="H_element : 080"  # scripted group (container) (typed FeaturePython)
  n = 11
  ref = H_element
FEATURE [App::DocumentObjectGroupPython] C_element143  label="C_element : 088"  # scripted group (container) (typed FeaturePython)
  n = 10
  ref = C_element
FEATURE [App::DocumentObjectGroupPython] N_element063  label="N_element : 035"  # scripted group (container) (typed FeaturePython)
  n = 2
  ref = N_element
FEATURE [App::DocumentObjectGroupPython] O_element124  label="O_element : 077"  # scripted group (container) (typed FeaturePython)
  n = 6
  ref = O_element
FEATURE [App::DocumentObjectGroupPython] G4_DNA_METHYLURIDINE  # scripted group (container) (typed FeaturePython)
  Dunit = g/cm3
  Dvalue = 1
  Group = -> [H_element133,C_element143,N_element063,O_element124]
  conduct = 2
  density = 1
  expand = 3
  formula = G4_DNA_METHYLURIDINE
  name = G4_DNA_METHYLURIDINE
  specific = 4
FEATURE [App::DocumentObjectGroupPython] P_element014  label="P_element : 003"  # scripted group (container) (typed FeaturePython)
  n = 1
  ref = P_element
FEATURE [App::DocumentObjectGroupPython] O_element125  label="O_element : 078"  # scripted group (container) (typed FeaturePython)
  n = 3
  ref = O_element
FEATURE [App::DocumentObjectGroupPython] G4_DNA_MONOPHOSPHATE  # scripted group (container) (typed FeaturePython)
  Dunit = g/cm3
  Dvalue = 1
  Group = -> [P_element014,O_element125]
  conduct = 2
  density = 1
  expand = 3
  formula = G4_DNA_MONOPHOSPHATE
  name = G4_DNA_MONOPHOSPHATE
  specific = 4
FEATURE [App::DocumentObjectGroupPython] H_element134  label="H_element : 081"  # scripted group (container) (typed FeaturePython)
  n = 10
  ref = H_element
FEATURE [App::DocumentObjectGroupPython] C_element144  label="C_element : 089"  # scripted group (container) (typed FeaturePython)
  n = 10
  ref = C_element
FEATURE [App::DocumentObjectGroupPython] N_element064  label="N_element : 036"  # scripted group (container) (typed FeaturePython)
  n = 5
  ref = N_element
FEATURE [App::DocumentObjectGroupPython] O_element126  label="O_element : 079"  # scripted group (container) (typed FeaturePython)
  n = 7
  ref = O_element
FEATURE [App::DocumentObjectGroupPython] P_element015  label="P_element : 004"  # scripted group (container) (typed FeaturePython)
  n = 1
  ref = P_element
FEATURE [App::DocumentObjectGroupPython] G4_DNA_A  # scripted group (container) (typed FeaturePython)
  Dunit = g/cm3
  Dvalue = 1
  Group = -> [H_element134,C_element144,N_element064,O_element126,P_element015]
  conduct = 2
  density = 1
  expand = 3
  formula = G4_DNA_A
  name = G4_DNA_A
  specific = 4
FEATURE [App::DocumentObjectGroupPython] H_element135  label="H_element : 082"  # scripted group (container) (typed FeaturePython)
  n = 10
  ref = H_element
FEATURE [App::DocumentObjectGroupPython] C_element145  label="C_element : 090"  # scripted group (container) (typed FeaturePython)
  n = 10
  ref = C_element
FEATURE [App::DocumentObjectGroupPython] N_element065  label="N_element : 037"  # scripted group (container) (typed FeaturePython)
  n = 5
  ref = N_element
FEATURE [App::DocumentObjectGroupPython] O_element127  label="O_element : 8"  # scripted group (container) (typed FeaturePython)
  n = 8
  ref = O_element
FEATURE [App::DocumentObjectGroupPython] P_element016  label="P_element : 005"  # scripted group (container) (typed FeaturePython)
  n = 1
  ref = P_element
FEATURE [App::DocumentObjectGroupPython] G4_DNA_G  # scripted group (container) (typed FeaturePython)
  Dunit = g/cm3
  Dvalue = 1
  Group = -> [H_element135,C_element145,N_element065,O_element127,P_element016]
  conduct = 2
  density = 1
  expand = 3
  formula = G4_DNA_G
  name = G4_DNA_G
  specific = 4
FEATURE [App::DocumentObjectGroupPython] H_element136  label="H_element : 083"  # scripted group (container) (typed FeaturePython)
  n = 10
  ref = H_element
FEATURE [App::DocumentObjectGroupPython] C_element146  label="C_element : 091"  # scripted group (container) (typed FeaturePython)
  n = 9
  ref = C_element
FEATURE [App::DocumentObjectGroupPython] N_element066  label="N_element : 038"  # scripted group (container) (typed FeaturePython)
  n = 3
  ref = N_element
FEATURE [App::DocumentObjectGroupPython] O_element128  label="O_element : 080"  # scripted group (container) (typed FeaturePython)
  n = 8
  ref = O_element
FEATURE [App::DocumentObjectGroupPython] P_element017  label="P_element : 006"  # scripted group (container) (typed FeaturePython)
  n = 1
  ref = P_element
FEATURE [App::DocumentObjectGroupPython] G4_DNA_C  # scripted group (container) (typed FeaturePython)
  Dunit = g/cm3
  Dvalue = 1
  Group = -> [H_element136,C_element146,N_element066,O_element128,P_element017]
  conduct = 2
  density = 1
  expand = 3
  formula = G4_DNA_C
  name = G4_DNA_C
  specific = 4
FEATURE [App::DocumentObjectGroupPython] H_element137  label="H_element : 084"  # scripted group (container) (typed FeaturePython)
  n = 9
  ref = H_element
FEATURE [App::DocumentObjectGroupPython] C_element147  label="C_element : 092"  # scripted group (container) (typed FeaturePython)
  n = 9
  ref = C_element
FEATURE [App::DocumentObjectGroupPython] N_element067  label="N_element : 039"  # scripted group (container) (typed FeaturePython)
  n = 2
  ref = N_element
FEATURE [App::DocumentObjectGroupPython] O_element129  label="O_element : 9"  # scripted group (container) (typed FeaturePython)
  n = 9
  ref = O_element
FEATURE [App::DocumentObjectGroupPython] P_element018  label="P_element : 007"  # scripted group (container) (typed FeaturePython)
  n = 1
  ref = P_element
FEATURE [App::DocumentObjectGroupPython] G4_DNA_U  # scripted group (container) (typed FeaturePython)
  Dunit = g/cm3
  Dvalue = 1
  Group = -> [H_element137,C_element147,N_element067,O_element129,P_element018]
  conduct = 2
  density = 1
  expand = 3
  formula = G4_DNA_U
  name = G4_DNA_U
  specific = 4
FEATURE [App::DocumentObjectGroupPython] H_element138  label="H_element : 085"  # scripted group (container) (typed FeaturePython)
  n = 11
  ref = H_element
FEATURE [App::DocumentObjectGroupPython] C_element148  label="C_element : 093"  # scripted group (container) (typed FeaturePython)
  n = 10
  ref = C_element
FEATURE [App::DocumentObjectGroupPython] N_element068  label="N_element : 040"  # scripted group (container) (typed FeaturePython)
  n = 2
  ref = N_element
FEATURE [App::DocumentObjectGroupPython] O_element130  label="O_element : 081"  # scripted group (container) (typed FeaturePython)
  n = 9
  ref = O_element
FEATURE [App::DocumentObjectGroupPython] P_element019  label="P_element : 008"  # scripted group (container) (typed FeaturePython)
  n = 1
  ref = P_element
FEATURE [App::DocumentObjectGroupPython] G4_DNA_MU  # scripted group (container) (typed FeaturePython)
  Dunit = g/cm3
  Dvalue = 1
  Group = -> [H_element138,C_element148,N_element068,O_element130,P_element019]
  conduct = 2
  density = 1
  expand = 3
  formula = G4_DNA_MU
  name = G4_DNA_MU
  specific = 4
FEATURE [App::DocumentObjectGroupPython] BioChemical  # scripted group (container) (typed FeaturePython)
  Group = -> [G4_CYTOSINE,G4_THYMINE,G4_URACIL,G4_DNA_ADENINE,G4_DNA_GUANINE,G4_DNA_CYTOSINE,G4_DNA_THYMINE,G4_DNA_URACIL,G4_DNA_ADENOSINE,G4_DNA_GUANOSINE,G4_DNA_CYTIDINE,G4_DNA_URIDINE,G4_DNA_METHYLURIDINE,G4_DNA_MONOPHOSPHATE,G4_DNA_A,G4_DNA_G,G4_DNA_C,G4_DNA_U,G4_DNA_MU]
FEATURE [App::DocumentObjectGroupPython] G4Materials  # scripted group (container) (typed FeaturePython)
  Group = -> [NIST,Element,HEP,Space,BioChemical]
  version = 1
FEATURE [App::DocumentObjectGroupPython] Geant4  # scripted group (container) (typed FeaturePython)
  Group = -> [G4Isotopes,G4Elements,G4Materials]
FEATURE [App::DocumentObjectGroupPython] Materials  # scripted group (container) (typed FeaturePython)
  Group = -> [Geant4]
FEATURE [Part::FeaturePython] GDMLBox_WorldBox  # WARN: FeaturePython — macro-defined, semantics opaque (R4)
  lunit = 2
  material = 5
  x = 200
  y = 200
  z = 200
FEATURE [Part::FeaturePython] GDMLSphere_Sphere  # WARN: FeaturePython — macro-defined, semantics opaque (R4)
  Placement = pos=(20,0,0) rot=(0,0,1;0rad)
  aunit = 0
  deltaphi = 2.02
  deltatheta = 2.02
  lunit = 2
  material = 18
  rmax = 20
  rmin = 10
  startphi = 0
  starttheta = 0
FEATURE [Part::FeaturePython] GDMLTorus_Torus  # WARN: FeaturePython — macro-defined, semantics opaque (R4)
  aunit = deg
  deltaphi = 360
  lunit = 2
  material = 5
  rmax = 5
  rmin = 0
  rtor = 10
  startphi = 10
FEATURE [Part::MultiFuse] Fusion
  Placement = pos=(30,0,0) rot=(0,0,1;0rad)
  Shapes = -> [GDMLSphere_Sphere,GDMLTorus_Torus]
  material = 18
FEATURE [Part::FeaturePython] Array  # Draft array (typed FeaturePython)
  Angle = 360
  ArrayType = 1
  Axis = (0,0,1)
  Base = -> Fusion
  Center = (0,0,0)
  Fuse = false
  IntervalAxis = (0,0,0)
  IntervalX = (50,0,0)
  IntervalY = (0,50,0)
  IntervalZ = (0,0,50)
  NumberCircles = 3
  NumberPolar = 5
  NumberX = 2
  NumberY = 2
  NumberZ = 1
  RadialDistance = 50
  Symmetry = 1
  TangentialDistance = 25
FEATURE [Part::FeaturePython] Clone  label="Array001"  # Draft clone (typed FeaturePython)
  AttacherType = Attacher::AttachEngine3D
  Fuse = false
  Objects = -> [Array]
  Scale = (1.5,1,1)
FEATURE [App::Part] Part
  Group = -> [Clone]
  Origin = -> Origin001
FEATURE [App::Part] worldVOL
  Group = -> [GDMLBox_WorldBox,Part]
  Origin = -> Origin
